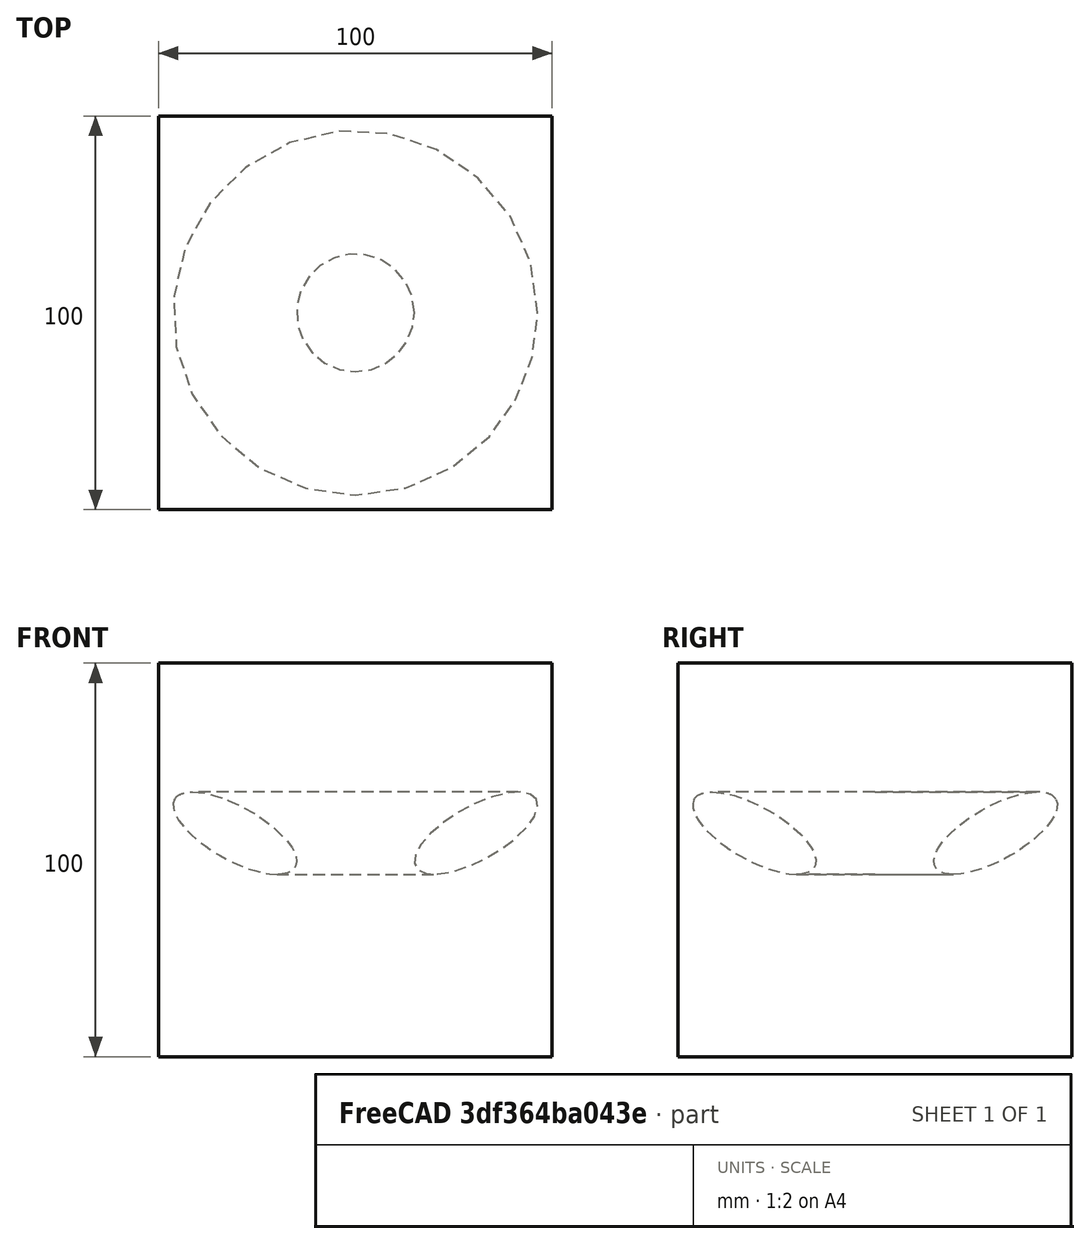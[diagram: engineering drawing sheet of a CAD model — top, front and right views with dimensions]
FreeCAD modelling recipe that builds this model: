
FCSTD DOCUMENT  (FreeCAD 0.21R33694 (Git))
Label: revolveSingleEdge
License: All rights reserved
LicenseURL: http://en.wikipedia.org/wiki/All_rights_reserved
objects: App::DocumentObjectGroupPython×1248, App::Part×2, Part::FeaturePython×1, Sketcher::SketchObject×1, Part::Revolution×1
note: 3 computed .brp shape members not serialized (recipe doc carries the construction recipe); baked Part::Feature solids carry a one-line shape summary decoded from their .brp

FEATURE [App::DocumentObjectGroupPython] HALFPI  # scripted group (container) (typed FeaturePython)
  name = HALFPI
  value = pi/2.
FEATURE [App::DocumentObjectGroupPython] PI  # scripted group (container) (typed FeaturePython)
  name = PI
  value = 1.*pi
FEATURE [App::DocumentObjectGroupPython] TWOPI  # scripted group (container) (typed FeaturePython)
  name = TWOPI
  value = 2.*pi
FEATURE [App::DocumentObjectGroupPython] Constants  # scripted group (container) (typed FeaturePython)
  Group = -> [HALFPI,PI,TWOPI]
FEATURE [App::DocumentObjectGroupPython] Variables  # scripted group (container) (typed FeaturePython)
FEATURE [App::DocumentObjectGroupPython] Quantities  # scripted group (container) (typed FeaturePython)
FEATURE [App::DocumentObjectGroupPython] Isotopes  # scripted group (container) (typed FeaturePython)
FEATURE [App::DocumentObjectGroupPython] Elements  # scripted group (container) (typed FeaturePython)
FEATURE [App::DocumentObjectGroupPython] G4Isotopes  # scripted group (container) (typed FeaturePython)
FEATURE [App::DocumentObjectGroupPython] H_element  # scripted group (container) (typed FeaturePython)
  Z = 1
  atom_value = 1.008
  formula = H
  name = H_element
FEATURE [App::DocumentObjectGroupPython] He_element  # scripted group (container) (typed FeaturePython)
  Z = 2
  atom_value = 4.0026
  formula = He
  name = He_element
FEATURE [App::DocumentObjectGroupPython] Li_element  # scripted group (container) (typed FeaturePython)
  Z = 3
  atom_value = 6.94
  formula = Li
  name = Li_element
FEATURE [App::DocumentObjectGroupPython] Be_element  # scripted group (container) (typed FeaturePython)
  Z = 4
  atom_value = 9.01218
  formula = Be
  name = Be_element
FEATURE [App::DocumentObjectGroupPython] B_element  # scripted group (container) (typed FeaturePython)
  Z = 5
  atom_value = 10.81
  formula = B
  name = B_element
FEATURE [App::DocumentObjectGroupPython] C_element  # scripted group (container) (typed FeaturePython)
  Z = 6
  atom_value = 12.011
  formula = C
  name = C_element
FEATURE [App::DocumentObjectGroupPython] N_element  # scripted group (container) (typed FeaturePython)
  Z = 7
  atom_value = 14.007
  formula = N
  name = N_element
FEATURE [App::DocumentObjectGroupPython] O_element  # scripted group (container) (typed FeaturePython)
  Z = 8
  atom_value = 15.999
  formula = O
  name = O_element
FEATURE [App::DocumentObjectGroupPython] F_element  # scripted group (container) (typed FeaturePython)
  Z = 9
  atom_value = 18.9984
  formula = F
  name = F_element
FEATURE [App::DocumentObjectGroupPython] Ne_element  # scripted group (container) (typed FeaturePython)
  Z = 10
  atom_value = 20.1797
  formula = Ne
  name = Ne_element
FEATURE [App::DocumentObjectGroupPython] Na_element  # scripted group (container) (typed FeaturePython)
  Z = 11
  atom_value = 22.9898
  formula = Na
  name = Na_element
FEATURE [App::DocumentObjectGroupPython] Mg_element  # scripted group (container) (typed FeaturePython)
  Z = 12
  atom_value = 24.305
  formula = Mg
  name = Mg_element
FEATURE [App::DocumentObjectGroupPython] Al_element  # scripted group (container) (typed FeaturePython)
  Z = 13
  atom_value = 26.9815
  formula = Al
  name = Al_element
FEATURE [App::DocumentObjectGroupPython] Si_element  # scripted group (container) (typed FeaturePython)
  Z = 14
  atom_value = 28.085
  formula = Si
  name = Si_element
FEATURE [App::DocumentObjectGroupPython] P_element  # scripted group (container) (typed FeaturePython)
  Z = 15
  atom_value = 30.9738
  formula = P
  name = P_element
FEATURE [App::DocumentObjectGroupPython] S_element  # scripted group (container) (typed FeaturePython)
  Z = 16
  atom_value = 32.06
  formula = S
  name = S_element
FEATURE [App::DocumentObjectGroupPython] Cl_element  # scripted group (container) (typed FeaturePython)
  Z = 17
  atom_value = 35.45
  formula = Cl
  name = Cl_element
FEATURE [App::DocumentObjectGroupPython] Ar_element  # scripted group (container) (typed FeaturePython)
  Z = 18
  atom_value = 39.95
  formula = Ar
  name = Ar_element
FEATURE [App::DocumentObjectGroupPython] K_element  # scripted group (container) (typed FeaturePython)
  Z = 19
  atom_value = 39.0983
  formula = K
  name = K_element
FEATURE [App::DocumentObjectGroupPython] Ca_element  # scripted group (container) (typed FeaturePython)
  Z = 20
  atom_value = 40.078
  formula = Ca
  name = Ca_element
FEATURE [App::DocumentObjectGroupPython] Sc_element  # scripted group (container) (typed FeaturePython)
  Z = 21
  atom_value = 44.9559
  formula = Sc
  name = Sc_element
FEATURE [App::DocumentObjectGroupPython] Ti_element  # scripted group (container) (typed FeaturePython)
  Z = 22
  atom_value = 47.867
  formula = Ti
  name = Ti_element
FEATURE [App::DocumentObjectGroupPython] V_element  # scripted group (container) (typed FeaturePython)
  Z = 23
  atom_value = 50.9415
  formula = V
  name = V_element
FEATURE [App::DocumentObjectGroupPython] Cr_element  # scripted group (container) (typed FeaturePython)
  Z = 24
  atom_value = 51.9961
  formula = Cr
  name = Cr_element
FEATURE [App::DocumentObjectGroupPython] Mn_element  # scripted group (container) (typed FeaturePython)
  Z = 25
  atom_value = 54.938
  formula = Mn
  name = Mn_element
FEATURE [App::DocumentObjectGroupPython] Fe_element  # scripted group (container) (typed FeaturePython)
  Z = 26
  atom_value = 55.845
  formula = Fe
  name = Fe_element
FEATURE [App::DocumentObjectGroupPython] Co_element  # scripted group (container) (typed FeaturePython)
  Z = 27
  atom_value = 58.9332
  formula = Co
  name = Co_element
FEATURE [App::DocumentObjectGroupPython] Ni_element  # scripted group (container) (typed FeaturePython)
  Z = 28
  atom_value = 58.6934
  formula = Ni
  name = Ni_element
FEATURE [App::DocumentObjectGroupPython] Cu_element  # scripted group (container) (typed FeaturePython)
  Z = 29
  atom_value = 63.546
  formula = Cu
  name = Cu_element
FEATURE [App::DocumentObjectGroupPython] Zn_element  # scripted group (container) (typed FeaturePython)
  Z = 30
  atom_value = 65.38
  formula = Zn
  name = Zn_element
FEATURE [App::DocumentObjectGroupPython] Ga_element  # scripted group (container) (typed FeaturePython)
  Z = 31
  atom_value = 69.723
  formula = Ga
  name = Ga_element
FEATURE [App::DocumentObjectGroupPython] Ge_element  # scripted group (container) (typed FeaturePython)
  Z = 32
  atom_value = 72.63
  formula = Ge
  name = Ge_element
FEATURE [App::DocumentObjectGroupPython] As_element  # scripted group (container) (typed FeaturePython)
  Z = 33
  atom_value = 74.9216
  formula = As
  name = As_element
FEATURE [App::DocumentObjectGroupPython] Se_element  # scripted group (container) (typed FeaturePython)
  Z = 34
  atom_value = 78.971
  formula = Se
  name = Se_element
FEATURE [App::DocumentObjectGroupPython] Br_element  # scripted group (container) (typed FeaturePython)
  Z = 35
  atom_value = 79.904
  formula = Br
  name = Br_element
FEATURE [App::DocumentObjectGroupPython] Kr_element  # scripted group (container) (typed FeaturePython)
  Z = 36
  atom_value = 83.798
  formula = Kr
  name = Kr_element
FEATURE [App::DocumentObjectGroupPython] Rb_element  # scripted group (container) (typed FeaturePython)
  Z = 37
  atom_value = 85.4678
  formula = Rb
  name = Rb_element
FEATURE [App::DocumentObjectGroupPython] Sr_element  # scripted group (container) (typed FeaturePython)
  Z = 38
  atom_value = 87.62
  formula = Sr
  name = Sr_element
FEATURE [App::DocumentObjectGroupPython] Y_element  # scripted group (container) (typed FeaturePython)
  Z = 39
  atom_value = 88.9058
  formula = Y
  name = Y_element
FEATURE [App::DocumentObjectGroupPython] Zr_element  # scripted group (container) (typed FeaturePython)
  Z = 40
  atom_value = 91.224
  formula = Zr
  name = Zr_element
FEATURE [App::DocumentObjectGroupPython] Nb_element  # scripted group (container) (typed FeaturePython)
  Z = 41
  atom_value = 92.9064
  formula = Nb
  name = Nb_element
FEATURE [App::DocumentObjectGroupPython] Mo_element  # scripted group (container) (typed FeaturePython)
  Z = 42
  atom_value = 95.95
  formula = Mo
  name = Mo_element
FEATURE [App::DocumentObjectGroupPython] Tc_element  # scripted group (container) (typed FeaturePython)
  Z = 43
  atom_value = 97
  formula = Tc
  name = Tc_element
FEATURE [App::DocumentObjectGroupPython] Ru_element  # scripted group (container) (typed FeaturePython)
  Z = 44
  atom_value = 101.07
  formula = Ru
  name = Ru_element
FEATURE [App::DocumentObjectGroupPython] Rh_element  # scripted group (container) (typed FeaturePython)
  Z = 45
  atom_value = 102.905
  formula = Rh
  name = Rh_element
FEATURE [App::DocumentObjectGroupPython] Pd_element  # scripted group (container) (typed FeaturePython)
  Z = 46
  atom_value = 106.42
  formula = Pd
  name = Pd_element
FEATURE [App::DocumentObjectGroupPython] Ag_element  # scripted group (container) (typed FeaturePython)
  Z = 47
  atom_value = 107.868
  formula = Ag
  name = Ag_element
FEATURE [App::DocumentObjectGroupPython] Cd_element  # scripted group (container) (typed FeaturePython)
  Z = 48
  atom_value = 112.414
  formula = Cd
  name = Cd_element
FEATURE [App::DocumentObjectGroupPython] In_element  # scripted group (container) (typed FeaturePython)
  Z = 49
  atom_value = 114.818
  formula = In
  name = In_element
FEATURE [App::DocumentObjectGroupPython] Sn_element  # scripted group (container) (typed FeaturePython)
  Z = 50
  atom_value = 118.71
  formula = Sn
  name = Sn_element
FEATURE [App::DocumentObjectGroupPython] Sb_element  # scripted group (container) (typed FeaturePython)
  Z = 51
  atom_value = 121.76
  formula = Sb
  name = Sb_element
FEATURE [App::DocumentObjectGroupPython] Te_element  # scripted group (container) (typed FeaturePython)
  Z = 52
  atom_value = 127.6
  formula = Te
  name = Te_element
FEATURE [App::DocumentObjectGroupPython] I_element  # scripted group (container) (typed FeaturePython)
  Z = 53
  atom_value = 126.904
  formula = I
  name = I_element
FEATURE [App::DocumentObjectGroupPython] Xe_element  # scripted group (container) (typed FeaturePython)
  Z = 54
  atom_value = 131.293
  formula = Xe
  name = Xe_element
FEATURE [App::DocumentObjectGroupPython] Cs_element  # scripted group (container) (typed FeaturePython)
  Z = 55
  atom_value = 132.905
  formula = Cs
  name = Cs_element
FEATURE [App::DocumentObjectGroupPython] Ba_element  # scripted group (container) (typed FeaturePython)
  Z = 56
  atom_value = 137.327
  formula = Ba
  name = Ba_element
FEATURE [App::DocumentObjectGroupPython] La_element  # scripted group (container) (typed FeaturePython)
  Z = 57
  atom_value = 138.905
  formula = La
  name = La_element
FEATURE [App::DocumentObjectGroupPython] Ce_element  # scripted group (container) (typed FeaturePython)
  Z = 58
  atom_value = 140.116
  formula = Ce
  name = Ce_element
FEATURE [App::DocumentObjectGroupPython] Pr_element  # scripted group (container) (typed FeaturePython)
  Z = 59
  atom_value = 140.908
  formula = Pr
  name = Pr_element
FEATURE [App::DocumentObjectGroupPython] Nd_element  # scripted group (container) (typed FeaturePython)
  Z = 60
  atom_value = 144.242
  formula = Nd
  name = Nd_element
FEATURE [App::DocumentObjectGroupPython] Pm_element  # scripted group (container) (typed FeaturePython)
  Z = 61
  atom_value = 145
  formula = Pm
  name = Pm_element
FEATURE [App::DocumentObjectGroupPython] Sm_element  # scripted group (container) (typed FeaturePython)
  Z = 62
  atom_value = 150.36
  formula = Sm
  name = Sm_element
FEATURE [App::DocumentObjectGroupPython] Eu_element  # scripted group (container) (typed FeaturePython)
  Z = 63
  atom_value = 151.964
  formula = Eu
  name = Eu_element
FEATURE [App::DocumentObjectGroupPython] Gd_element  # scripted group (container) (typed FeaturePython)
  Z = 64
  atom_value = 157.25
  formula = Gd
  name = Gd_element
FEATURE [App::DocumentObjectGroupPython] Tb_element  # scripted group (container) (typed FeaturePython)
  Z = 65
  atom_value = 158.925
  formula = Tb
  name = Tb_element
FEATURE [App::DocumentObjectGroupPython] Dy_element  # scripted group (container) (typed FeaturePython)
  Z = 66
  atom_value = 162.5
  formula = Dy
  name = Dy_element
FEATURE [App::DocumentObjectGroupPython] Ho_element  # scripted group (container) (typed FeaturePython)
  Z = 67
  atom_value = 164.93
  formula = Ho
  name = Ho_element
FEATURE [App::DocumentObjectGroupPython] Er_element  # scripted group (container) (typed FeaturePython)
  Z = 68
  atom_value = 167.259
  formula = Er
  name = Er_element
FEATURE [App::DocumentObjectGroupPython] Tm_element  # scripted group (container) (typed FeaturePython)
  Z = 69
  atom_value = 168.934
  formula = Tm
  name = Tm_element
FEATURE [App::DocumentObjectGroupPython] Yb_element  # scripted group (container) (typed FeaturePython)
  Z = 70
  atom_value = 173.045
  formula = Yb
  name = Yb_element
FEATURE [App::DocumentObjectGroupPython] Lu_element  # scripted group (container) (typed FeaturePython)
  Z = 71
  atom_value = 174.967
  formula = Lu
  name = Lu_element
FEATURE [App::DocumentObjectGroupPython] Hf_element  # scripted group (container) (typed FeaturePython)
  Z = 72
  atom_value = 178.49
  formula = Hf
  name = Hf_element
FEATURE [App::DocumentObjectGroupPython] Ta_element  # scripted group (container) (typed FeaturePython)
  Z = 73
  atom_value = 180.948
  formula = Ta
  name = Ta_element
FEATURE [App::DocumentObjectGroupPython] W_element  # scripted group (container) (typed FeaturePython)
  Z = 74
  atom_value = 183.84
  formula = W
  name = W_element
FEATURE [App::DocumentObjectGroupPython] Re_element  # scripted group (container) (typed FeaturePython)
  Z = 75
  atom_value = 186.207
  formula = Re
  name = Re_element
FEATURE [App::DocumentObjectGroupPython] Os_element  # scripted group (container) (typed FeaturePython)
  Z = 76
  atom_value = 190.23
  formula = Os
  name = Os_element
FEATURE [App::DocumentObjectGroupPython] Ir_element  # scripted group (container) (typed FeaturePython)
  Z = 77
  atom_value = 192.217
  formula = Ir
  name = Ir_element
FEATURE [App::DocumentObjectGroupPython] Pt_element  # scripted group (container) (typed FeaturePython)
  Z = 78
  atom_value = 195.084
  formula = Pt
  name = Pt_element
FEATURE [App::DocumentObjectGroupPython] Au_element  # scripted group (container) (typed FeaturePython)
  Z = 79
  atom_value = 196.967
  formula = Au
  name = Au_element
FEATURE [App::DocumentObjectGroupPython] Hg_element  # scripted group (container) (typed FeaturePython)
  Z = 80
  atom_value = 200.592
  formula = Hg
  name = Hg_element
FEATURE [App::DocumentObjectGroupPython] Tl_element  # scripted group (container) (typed FeaturePython)
  Z = 81
  atom_value = 204.38
  formula = Tl
  name = Tl_element
FEATURE [App::DocumentObjectGroupPython] Pb_element  # scripted group (container) (typed FeaturePython)
  Z = 82
  atom_value = 207.2
  formula = Pb
  name = Pb_element
FEATURE [App::DocumentObjectGroupPython] Bi_element  # scripted group (container) (typed FeaturePython)
  Z = 83
  atom_value = 208.98
  formula = Bi
  name = Bi_element
FEATURE [App::DocumentObjectGroupPython] Po_element  # scripted group (container) (typed FeaturePython)
  Z = 84
  atom_value = 209
  formula = Po
  name = Po_element
FEATURE [App::DocumentObjectGroupPython] At_element  # scripted group (container) (typed FeaturePython)
  Z = 85
  atom_value = 210
  formula = At
  name = At_element
FEATURE [App::DocumentObjectGroupPython] Rn_element  # scripted group (container) (typed FeaturePython)
  Z = 86
  atom_value = 222
  formula = Rn
  name = Rn_element
FEATURE [App::DocumentObjectGroupPython] Fr_element  # scripted group (container) (typed FeaturePython)
  Z = 87
  atom_value = 223
  formula = Fr
  name = Fr_element
FEATURE [App::DocumentObjectGroupPython] Ra_element  # scripted group (container) (typed FeaturePython)
  Z = 88
  atom_value = 226
  formula = Ra
  name = Ra_element
FEATURE [App::DocumentObjectGroupPython] Ac_element  # scripted group (container) (typed FeaturePython)
  Z = 89
  atom_value = 227
  formula = Ac
  name = Ac_element
FEATURE [App::DocumentObjectGroupPython] Th_element  # scripted group (container) (typed FeaturePython)
  Z = 90
  atom_value = 232.038
  formula = Th
  name = Th_element
FEATURE [App::DocumentObjectGroupPython] Pa_element  # scripted group (container) (typed FeaturePython)
  Z = 91
  atom_value = 231.036
  formula = Pa
  name = Pa_element
FEATURE [App::DocumentObjectGroupPython] U_element  # scripted group (container) (typed FeaturePython)
  Z = 92
  atom_value = 238.029
  formula = U
  name = U_element
FEATURE [App::DocumentObjectGroupPython] Np_element  # scripted group (container) (typed FeaturePython)
  Z = 93
  atom_value = 237
  formula = Np
  name = Np_element
FEATURE [App::DocumentObjectGroupPython] Pu_element  # scripted group (container) (typed FeaturePython)
  Z = 94
  atom_value = 244
  formula = Pu
  name = Pu_element
FEATURE [App::DocumentObjectGroupPython] Am_element  # scripted group (container) (typed FeaturePython)
  Z = 95
  atom_value = 243
  formula = Am
  name = Am_element
FEATURE [App::DocumentObjectGroupPython] Cm_element  # scripted group (container) (typed FeaturePython)
  Z = 96
  atom_value = 247
  formula = Cm
  name = Cm_element
FEATURE [App::DocumentObjectGroupPython] Bk_element  # scripted group (container) (typed FeaturePython)
  Z = 97
  atom_value = 247
  formula = Bk
  name = Bk_element
FEATURE [App::DocumentObjectGroupPython] Cf_element  # scripted group (container) (typed FeaturePython)
  Z = 98
  atom_value = 251
  formula = Cf
  name = Cf_element
FEATURE [App::DocumentObjectGroupPython] G4Elements  # scripted group (container) (typed FeaturePython)
  Group = -> [H_element,He_element,Li_element,Be_element,B_element,C_element,N_element,O_element,F_element,Ne_element,Na_element,Mg_element,Al_element,Si_element,P_element,S_element,Cl_element,Ar_element,K_element,Ca_element,Sc_element,Ti_element,V_element,Cr_element,Mn_element,Fe_element,Co_element,Ni_element,Cu_element,Zn_element,Ga_element,Ge_element,As_element,Se_element,Br_element,Kr_element,Rb_element,+61 more]
FEATURE [App::DocumentObjectGroupPython] H_element001  label="H_element : 0.101"  # scripted group (container) (typed FeaturePython)
  n = 0.101327
FEATURE [App::DocumentObjectGroupPython] C_element001  label="C_element : 0.775"  # scripted group (container) (typed FeaturePython)
  n = 0.7755
FEATURE [App::DocumentObjectGroupPython] N_element001  label="N_element : 0.035"  # scripted group (container) (typed FeaturePython)
  n = 0.035057
FEATURE [App::DocumentObjectGroupPython] O_element001  label="O_element : 0.052"  # scripted group (container) (typed FeaturePython)
  n = 0.0523159
FEATURE [App::DocumentObjectGroupPython] F_element001  label="F_element : 0.017"  # scripted group (container) (typed FeaturePython)
  n = 0.017422
FEATURE [App::DocumentObjectGroupPython] Ca_element001  label="Ca_element : 0.018"  # scripted group (container) (typed FeaturePython)
  n = 0.018378
FEATURE [App::DocumentObjectGroupPython] G4_A_150_TISSUE  label="G4_A-150_TISSUE"  # scripted group (container) (typed FeaturePython)
  Dunit = g/cm3
  Dvalue = 1.127
  Group = -> [H_element001,C_element001,N_element001,O_element001,F_element001,Ca_element001]
  conduct = 2
  density = 1
  expand = 3
  formula = G4_A-150_TISSUE
  name = G4_A-150_TISSUE
  specific = 4
FEATURE [App::DocumentObjectGroupPython] C_element002  label="C_element : 3"  # scripted group (container) (typed FeaturePython)
  n = 3
  ref = C_element
FEATURE [App::DocumentObjectGroupPython] H_element002  label="H_element : 6"  # scripted group (container) (typed FeaturePython)
  n = 6
  ref = H_element
FEATURE [App::DocumentObjectGroupPython] O_element002  label="O_element : 1"  # scripted group (container) (typed FeaturePython)
  n = 1
  ref = O_element
FEATURE [App::DocumentObjectGroupPython] G4_ACETONE  # scripted group (container) (typed FeaturePython)
  Dunit = g/cm3
  Dvalue = 0.7899
  Group = -> [C_element002,H_element002,O_element002]
  conduct = 2
  density = 1
  expand = 3
  formula = G4_ACETONE
  name = G4_ACETONE
  specific = 4
FEATURE [App::DocumentObjectGroupPython] C_element003  label="C_element : 2"  # scripted group (container) (typed FeaturePython)
  n = 2
  ref = C_element
FEATURE [App::DocumentObjectGroupPython] H_element003  label="H_element : 2"  # scripted group (container) (typed FeaturePython)
  n = 2
  ref = H_element
FEATURE [App::DocumentObjectGroupPython] G4_ACETYLENE  # scripted group (container) (typed FeaturePython)
  Dunit = g/cm3
  Dvalue = 0.0010967
  Group = -> [C_element003,H_element003]
  conduct = 2
  density = 1
  expand = 3
  formula = G4_ACETYLENE
  name = G4_ACETYLENE
  specific = 4
FEATURE [App::DocumentObjectGroupPython] C_element004  label="C_element : 5"  # scripted group (container) (typed FeaturePython)
  n = 5
  ref = C_element
FEATURE [App::DocumentObjectGroupPython] H_element004  label="H_element : 5"  # scripted group (container) (typed FeaturePython)
  n = 5
  ref = H_element
FEATURE [App::DocumentObjectGroupPython] N_element002  label="N_element : 5"  # scripted group (container) (typed FeaturePython)
  n = 5
  ref = N_element
FEATURE [App::DocumentObjectGroupPython] G4_ADENINE  # scripted group (container) (typed FeaturePython)
  Dunit = g/cm3
  Dvalue = 1.6
  Group = -> [C_element004,H_element004,N_element002]
  conduct = 2
  density = 1
  expand = 3
  formula = G4_ADENINE
  name = G4_ADENINE
  specific = 4
FEATURE [App::DocumentObjectGroupPython] H_element005  label="H_element : 0.114"  # scripted group (container) (typed FeaturePython)
  n = 0.114
FEATURE [App::DocumentObjectGroupPython] C_element005  label="C_element : 0.598"  # scripted group (container) (typed FeaturePython)
  n = 0.598
FEATURE [App::DocumentObjectGroupPython] N_element003  label="N_element : 0.007"  # scripted group (container) (typed FeaturePython)
  n = 0.007
FEATURE [App::DocumentObjectGroupPython] O_element003  label="O_element : 0.278"  # scripted group (container) (typed FeaturePython)
  n = 0.278
FEATURE [App::DocumentObjectGroupPython] Na_element001  label="Na_element : 0.001"  # scripted group (container) (typed FeaturePython)
  n = 0.001
FEATURE [App::DocumentObjectGroupPython] S_element001  label="S_element : 0.001"  # scripted group (container) (typed FeaturePython)
  n = 0.001
FEATURE [App::DocumentObjectGroupPython] Cl_element001  label="Cl_element : 0.001"  # scripted group (container) (typed FeaturePython)
  n = 0.001
FEATURE [App::DocumentObjectGroupPython] G4_ADIPOSE_TISSUE_ICRP  # scripted group (container) (typed FeaturePython)
  Dunit = g/cm3
  Dvalue = 0.95
  Group = -> [H_element005,C_element005,N_element003,O_element003,Na_element001,S_element001,Cl_element001]
  conduct = 2
  density = 1
  expand = 3
  formula = G4_ADIPOSE_TISSUE_ICRP
  name = G4_ADIPOSE_TISSUE_ICRP
  specific = 4
FEATURE [App::DocumentObjectGroupPython] C_element006  label="C_element : 0.000"  # scripted group (container) (typed FeaturePython)
  n = 0.000124
FEATURE [App::DocumentObjectGroupPython] N_element004  label="N_element : 0.755"  # scripted group (container) (typed FeaturePython)
  n = 0.755268
FEATURE [App::DocumentObjectGroupPython] O_element004  label="O_element : 0.232"  # scripted group (container) (typed FeaturePython)
  n = 0.231781
FEATURE [App::DocumentObjectGroupPython] Ar_element001  label="Ar_element : 0.013"  # scripted group (container) (typed FeaturePython)
  n = 0.012827
FEATURE [App::DocumentObjectGroupPython] G4_AIR  # scripted group (container) (typed FeaturePython)
  Dunit = g/cm3
  Dvalue = 0.00120479
  Group = -> [C_element006,N_element004,O_element004,Ar_element001]
  conduct = 2
  density = 1
  expand = 3
  formula = G4_AIR
  name = G4_AIR
  specific = 4
FEATURE [App::DocumentObjectGroupPython] C_element007  label="C_element : 006"  # scripted group (container) (typed FeaturePython)
  n = 3
  ref = C_element
FEATURE [App::DocumentObjectGroupPython] H_element006  label="H_element : 7"  # scripted group (container) (typed FeaturePython)
  n = 7
  ref = H_element
FEATURE [App::DocumentObjectGroupPython] N_element005  label="N_element : 1"  # scripted group (container) (typed FeaturePython)
  n = 1
  ref = N_element
FEATURE [App::DocumentObjectGroupPython] O_element005  label="O_element : 2"  # scripted group (container) (typed FeaturePython)
  n = 2
  ref = O_element
FEATURE [App::DocumentObjectGroupPython] G4_ALANINE  # scripted group (container) (typed FeaturePython)
  Dunit = g/cm3
  Dvalue = 1.42
  Group = -> [C_element007,H_element006,N_element005,O_element005]
  conduct = 2
  density = 1
  expand = 3
  formula = G4_ALANINE
  name = G4_ALANINE
  specific = 4
FEATURE [App::DocumentObjectGroupPython] Al_element001  label="Al_element : 2"  # scripted group (container) (typed FeaturePython)
  n = 2
  ref = Al_element
FEATURE [App::DocumentObjectGroupPython] O_element006  label="O_element : 3"  # scripted group (container) (typed FeaturePython)
  n = 3
  ref = O_element
FEATURE [App::DocumentObjectGroupPython] G4_ALUMINUM_OXIDE  # scripted group (container) (typed FeaturePython)
  Dunit = g/cm3
  Dvalue = 3.97
  Group = -> [Al_element001,O_element006]
  conduct = 2
  density = 1
  expand = 3
  formula = G4_ALUMINUM_OXIDE
  name = G4_ALUMINUM_OXIDE
  specific = 4
FEATURE [App::DocumentObjectGroupPython] H_element007  label="H_element : 0.106"  # scripted group (container) (typed FeaturePython)
  n = 0.10593
FEATURE [App::DocumentObjectGroupPython] C_element008  label="C_element : 0.789"  # scripted group (container) (typed FeaturePython)
  n = 0.788974
FEATURE [App::DocumentObjectGroupPython] O_element007  label="O_element : 0.105"  # scripted group (container) (typed FeaturePython)
  n = 0.105096
FEATURE [App::DocumentObjectGroupPython] G4_AMBER  # scripted group (container) (typed FeaturePython)
  Dunit = g/cm3
  Dvalue = 1.1
  Group = -> [H_element007,C_element008,O_element007]
  conduct = 2
  density = 1
  expand = 3
  formula = G4_AMBER
  name = G4_AMBER
  specific = 4
FEATURE [App::DocumentObjectGroupPython] N_element006  label="N_element : 006"  # scripted group (container) (typed FeaturePython)
  n = 1
  ref = N_element
FEATURE [App::DocumentObjectGroupPython] H_element008  label="H_element : 3"  # scripted group (container) (typed FeaturePython)
  n = 3
  ref = H_element
FEATURE [App::DocumentObjectGroupPython] G4_AMMONIA  # scripted group (container) (typed FeaturePython)
  Dunit = g/cm3
  Dvalue = 0.000826019
  Group = -> [N_element006,H_element008]
  conduct = 2
  density = 1
  expand = 3
  formula = G4_AMMONIA
  name = G4_AMMONIA
  specific = 4
FEATURE [App::DocumentObjectGroupPython] C_element009  label="C_element : 6"  # scripted group (container) (typed FeaturePython)
  n = 6
  ref = C_element
FEATURE [App::DocumentObjectGroupPython] H_element009  label="H_element : 008"  # scripted group (container) (typed FeaturePython)
  n = 7
  ref = H_element
FEATURE [App::DocumentObjectGroupPython] N_element007  label="N_element : 007"  # scripted group (container) (typed FeaturePython)
  n = 1
  ref = N_element
FEATURE [App::DocumentObjectGroupPython] G4_ANILINE  # scripted group (container) (typed FeaturePython)
  Dunit = g/cm3
  Dvalue = 1.0235
  Group = -> [C_element009,H_element009,N_element007]
  conduct = 2
  density = 1
  expand = 3
  formula = G4_ANILINE
  name = G4_ANILINE
  specific = 4
FEATURE [App::DocumentObjectGroupPython] C_element010  label="C_element : 14"  # scripted group (container) (typed FeaturePython)
  n = 14
  ref = C_element
FEATURE [App::DocumentObjectGroupPython] H_element010  label="H_element : 10"  # scripted group (container) (typed FeaturePython)
  n = 10
  ref = H_element
FEATURE [App::DocumentObjectGroupPython] G4_ANTHRACENE  # scripted group (container) (typed FeaturePython)
  Dunit = g/cm3
  Dvalue = 1.283
  Group = -> [C_element010,H_element010]
  conduct = 2
  density = 1
  expand = 3
  formula = G4_ANTHRACENE
  name = G4_ANTHRACENE
  specific = 4
FEATURE [App::DocumentObjectGroupPython] H_element011  label="H_element : 0.065"  # scripted group (container) (typed FeaturePython)
  n = 0.0654709
FEATURE [App::DocumentObjectGroupPython] C_element011  label="C_element : 0.537"  # scripted group (container) (typed FeaturePython)
  n = 0.536944
FEATURE [App::DocumentObjectGroupPython] N_element008  label="N_element : 0.021"  # scripted group (container) (typed FeaturePython)
  n = 0.0215
FEATURE [App::DocumentObjectGroupPython] O_element008  label="O_element : 0.032"  # scripted group (container) (typed FeaturePython)
  n = 0.032085
FEATURE [App::DocumentObjectGroupPython] F_element002  label="F_element : 0.167"  # scripted group (container) (typed FeaturePython)
  n = 0.167411
FEATURE [App::DocumentObjectGroupPython] Ca_element002  label="Ca_element : 0.177"  # scripted group (container) (typed FeaturePython)
  n = 0.176589
FEATURE [App::DocumentObjectGroupPython] G4_B_100_BONE  label="G4_B-100_BONE"  # scripted group (container) (typed FeaturePython)
  Dunit = g/cm3
  Dvalue = 1.45
  Group = -> [H_element011,C_element011,N_element008,O_element008,F_element002,Ca_element002]
  conduct = 2
  density = 1
  expand = 3
  formula = G4_B-100_BONE
  name = G4_B-100_BONE
  specific = 4
FEATURE [App::DocumentObjectGroupPython] H_element012  label="H_element : 0.057"  # scripted group (container) (typed FeaturePython)
  n = 0.057441
FEATURE [App::DocumentObjectGroupPython] C_element012  label="C_element : 0.790"  # scripted group (container) (typed FeaturePython)
  n = 0.774591
FEATURE [App::DocumentObjectGroupPython] O_element009  label="O_element : 0.168"  # scripted group (container) (typed FeaturePython)
  n = 0.167968
FEATURE [App::DocumentObjectGroupPython] G4_BAKELITE  # scripted group (container) (typed FeaturePython)
  Dunit = g/cm3
  Dvalue = 1.25
  Group = -> [H_element012,C_element012,O_element009]
  conduct = 2
  density = 1
  expand = 3
  formula = G4_BAKELITE
  name = G4_BAKELITE
  specific = 4
FEATURE [App::DocumentObjectGroupPython] Ba_element001  label="Ba_element : 1"  # scripted group (container) (typed FeaturePython)
  n = 1
  ref = Ba_element
FEATURE [App::DocumentObjectGroupPython] F_element003  label="F_element : 2"  # scripted group (container) (typed FeaturePython)
  n = 2
  ref = F_element
FEATURE [App::DocumentObjectGroupPython] G4_BARIUM_FLUORIDE  # scripted group (container) (typed FeaturePython)
  Dunit = g/cm3
  Dvalue = 4.89
  Group = -> [Ba_element001,F_element003]
  conduct = 2
  density = 1
  expand = 3
  formula = G4_BARIUM_FLUORIDE
  name = G4_BARIUM_FLUORIDE
  specific = 4
FEATURE [App::DocumentObjectGroupPython] Ba_element002  label="Ba_element : 002"  # scripted group (container) (typed FeaturePython)
  n = 1
  ref = Ba_element
FEATURE [App::DocumentObjectGroupPython] S_element002  label="S_element : 1"  # scripted group (container) (typed FeaturePython)
  n = 1
  ref = S_element
FEATURE [App::DocumentObjectGroupPython] O_element010  label="O_element : 4"  # scripted group (container) (typed FeaturePython)
  n = 4
  ref = O_element
FEATURE [App::DocumentObjectGroupPython] G4_BARIUM_SULFATE  # scripted group (container) (typed FeaturePython)
  Dunit = g/cm3
  Dvalue = 4.5
  Group = -> [Ba_element002,S_element002,O_element010]
  conduct = 2
  density = 1
  expand = 3
  formula = G4_BARIUM_SULFATE
  name = G4_BARIUM_SULFATE
  specific = 4
FEATURE [App::DocumentObjectGroupPython] C_element013  label="C_element : 007"  # scripted group (container) (typed FeaturePython)
  n = 6
  ref = C_element
FEATURE [App::DocumentObjectGroupPython] H_element013  label="H_element : 009"  # scripted group (container) (typed FeaturePython)
  n = 6
  ref = H_element
FEATURE [App::DocumentObjectGroupPython] G4_BENZENE  # scripted group (container) (typed FeaturePython)
  Dunit = g/cm3
  Dvalue = 0.87865
  Group = -> [C_element013,H_element013]
  conduct = 2
  density = 1
  expand = 3
  formula = G4_BENZENE
  name = G4_BENZENE
  specific = 4
FEATURE [App::DocumentObjectGroupPython] Be_element001  label="Be_element : 1"  # scripted group (container) (typed FeaturePython)
  n = 1
  ref = Be_element
FEATURE [App::DocumentObjectGroupPython] O_element011  label="O_element : 005"  # scripted group (container) (typed FeaturePython)
  n = 1
  ref = O_element
FEATURE [App::DocumentObjectGroupPython] G4_BERYLLIUM_OXIDE  # scripted group (container) (typed FeaturePython)
  Dunit = g/cm3
  Dvalue = 3.01
  Group = -> [Be_element001,O_element011]
  conduct = 2
  density = 1
  expand = 3
  formula = G4_BERYLLIUM_OXIDE
  name = G4_BERYLLIUM_OXIDE
  specific = 4
FEATURE [App::DocumentObjectGroupPython] Bi_element001  label="Bi_element : 4"  # scripted group (container) (typed FeaturePython)
  n = 4
  ref = Bi_element
FEATURE [App::DocumentObjectGroupPython] Ge_element001  label="Ge_element : 3"  # scripted group (container) (typed FeaturePython)
  n = 3
  ref = Ge_element
FEATURE [App::DocumentObjectGroupPython] O_element012  label="O_element : 12"  # scripted group (container) (typed FeaturePython)
  n = 12
  ref = O_element
FEATURE [App::DocumentObjectGroupPython] G4_BGO  # scripted group (container) (typed FeaturePython)
  Dunit = g/cm3
  Dvalue = 7.13
  Group = -> [Bi_element001,Ge_element001,O_element012]
  conduct = 2
  density = 1
  expand = 3
  formula = G4_BGO
  name = G4_BGO
  specific = 4
FEATURE [App::DocumentObjectGroupPython] H_element014  label="H_element : 0.102"  # scripted group (container) (typed FeaturePython)
  n = 0.102
FEATURE [App::DocumentObjectGroupPython] C_element014  label="C_element : 0.110"  # scripted group (container) (typed FeaturePython)
  n = 0.11
FEATURE [App::DocumentObjectGroupPython] N_element009  label="N_element : 0.033"  # scripted group (container) (typed FeaturePython)
  n = 0.033
FEATURE [App::DocumentObjectGroupPython] O_element013  label="O_element : 0.745"  # scripted group (container) (typed FeaturePython)
  n = 0.745
FEATURE [App::DocumentObjectGroupPython] Na_element002  label="Na_element : 0.002"  # scripted group (container) (typed FeaturePython)
  n = 0.001
FEATURE [App::DocumentObjectGroupPython] P_element001  label="P_element : 0.001"  # scripted group (container) (typed FeaturePython)
  n = 0.001
FEATURE [App::DocumentObjectGroupPython] S_element003  label="S_element : 0.002"  # scripted group (container) (typed FeaturePython)
  n = 0.002
FEATURE [App::DocumentObjectGroupPython] Cl_element002  label="Cl_element : 0.003"  # scripted group (container) (typed FeaturePython)
  n = 0.003
FEATURE [App::DocumentObjectGroupPython] K_element001  label="K_element : 0.002"  # scripted group (container) (typed FeaturePython)
  n = 0.002
FEATURE [App::DocumentObjectGroupPython] Fe_element001  label="Fe_element : 0.001"  # scripted group (container) (typed FeaturePython)
  n = 0.001
FEATURE [App::DocumentObjectGroupPython] G4_BLOOD_ICRP  # scripted group (container) (typed FeaturePython)
  Dunit = g/cm3
  Dvalue = 1.06
  Group = -> [H_element014,C_element014,N_element009,O_element013,Na_element002,P_element001,S_element003,Cl_element002,K_element001,Fe_element001]
  conduct = 2
  density = 1
  expand = 3
  formula = G4_BLOOD_ICRP
  name = G4_BLOOD_ICRP
  specific = 4
FEATURE [App::DocumentObjectGroupPython] H_element015  label="H_element : 0.064"  # scripted group (container) (typed FeaturePython)
  n = 0.064
FEATURE [App::DocumentObjectGroupPython] C_element015  label="C_element : 0.278"  # scripted group (container) (typed FeaturePython)
  n = 0.278
FEATURE [App::DocumentObjectGroupPython] N_element010  label="N_element : 0.027"  # scripted group (container) (typed FeaturePython)
  n = 0.027
FEATURE [App::DocumentObjectGroupPython] O_element014  label="O_element : 0.410"  # scripted group (container) (typed FeaturePython)
  n = 0.41
FEATURE [App::DocumentObjectGroupPython] Mg_element001  label="Mg_element : 0.002"  # scripted group (container) (typed FeaturePython)
  n = 0.002
FEATURE [App::DocumentObjectGroupPython] P_element002  label="P_element : 0.070"  # scripted group (container) (typed FeaturePython)
  n = 0.07
FEATURE [App::DocumentObjectGroupPython] S_element004  label="S_element : 0.003"  # scripted group (container) (typed FeaturePython)
  n = 0.002
FEATURE [App::DocumentObjectGroupPython] Ca_element003  label="Ca_element : 0.147"  # scripted group (container) (typed FeaturePython)
  n = 0.147
FEATURE [App::DocumentObjectGroupPython] G4_BONE_COMPACT_ICRU  # scripted group (container) (typed FeaturePython)
  Dunit = g/cm3
  Dvalue = 1.85
  Group = -> [H_element015,C_element015,N_element010,O_element014,Mg_element001,P_element002,S_element004,Ca_element003]
  conduct = 2
  density = 1
  expand = 3
  formula = G4_BONE_COMPACT_ICRU
  name = G4_BONE_COMPACT_ICRU
  specific = 4
FEATURE [App::DocumentObjectGroupPython] H_element016  label="H_element : 0.034"  # scripted group (container) (typed FeaturePython)
  n = 0.034
FEATURE [App::DocumentObjectGroupPython] C_element016  label="C_element : 0.155"  # scripted group (container) (typed FeaturePython)
  n = 0.155
FEATURE [App::DocumentObjectGroupPython] N_element011  label="N_element : 0.042"  # scripted group (container) (typed FeaturePython)
  n = 0.042
FEATURE [App::DocumentObjectGroupPython] O_element015  label="O_element : 0.435"  # scripted group (container) (typed FeaturePython)
  n = 0.435
FEATURE [App::DocumentObjectGroupPython] Na_element003  label="Na_element : 0.003"  # scripted group (container) (typed FeaturePython)
  n = 0.001
FEATURE [App::DocumentObjectGroupPython] Mg_element002  label="Mg_element : 0.003"  # scripted group (container) (typed FeaturePython)
  n = 0.002
FEATURE [App::DocumentObjectGroupPython] P_element003  label="P_element : 0.103"  # scripted group (container) (typed FeaturePython)
  n = 0.103
FEATURE [App::DocumentObjectGroupPython] S_element005  label="S_element : 0.004"  # scripted group (container) (typed FeaturePython)
  n = 0.003
FEATURE [App::DocumentObjectGroupPython] Ca_element004  label="Ca_element : 0.225"  # scripted group (container) (typed FeaturePython)
  n = 0.225
FEATURE [App::DocumentObjectGroupPython] G4_BONE_CORTICAL_ICRP  # scripted group (container) (typed FeaturePython)
  Dunit = g/cm3
  Dvalue = 1.92
  Group = -> [H_element016,C_element016,N_element011,O_element015,Na_element003,Mg_element002,P_element003,S_element005,Ca_element004]
  conduct = 2
  density = 1
  expand = 3
  formula = G4_BONE_CORTICAL_ICRP
  name = G4_BONE_CORTICAL_ICRP
  specific = 4
FEATURE [App::DocumentObjectGroupPython] B_element001  label="B_element : 4"  # scripted group (container) (typed FeaturePython)
  n = 4
  ref = B_element
FEATURE [App::DocumentObjectGroupPython] C_element017  label="C_element : 1"  # scripted group (container) (typed FeaturePython)
  n = 1
  ref = C_element
FEATURE [App::DocumentObjectGroupPython] G4_BORON_CARBIDE  # scripted group (container) (typed FeaturePython)
  Dunit = g/cm3
  Dvalue = 2.52
  Group = -> [B_element001,C_element017]
  conduct = 2
  density = 1
  expand = 3
  formula = G4_BORON_CARBIDE
  name = G4_BORON_CARBIDE
  specific = 4
FEATURE [App::DocumentObjectGroupPython] B_element002  label="B_element : 2"  # scripted group (container) (typed FeaturePython)
  n = 2
  ref = B_element
FEATURE [App::DocumentObjectGroupPython] O_element016  label="O_element : 006"  # scripted group (container) (typed FeaturePython)
  n = 3
  ref = O_element
FEATURE [App::DocumentObjectGroupPython] G4_BORON_OXIDE  # scripted group (container) (typed FeaturePython)
  Dunit = g/cm3
  Dvalue = 1.812
  Group = -> [B_element002,O_element016]
  conduct = 2
  density = 1
  expand = 3
  formula = G4_BORON_OXIDE
  name = G4_BORON_OXIDE
  specific = 4
FEATURE [App::DocumentObjectGroupPython] H_element017  label="H_element : 0.107"  # scripted group (container) (typed FeaturePython)
  n = 0.107
FEATURE [App::DocumentObjectGroupPython] C_element018  label="C_element : 0.145"  # scripted group (container) (typed FeaturePython)
  n = 0.145
FEATURE [App::DocumentObjectGroupPython] N_element012  label="N_element : 0.022"  # scripted group (container) (typed FeaturePython)
  n = 0.022
FEATURE [App::DocumentObjectGroupPython] O_element017  label="O_element : 0.712"  # scripted group (container) (typed FeaturePython)
  n = 0.712
FEATURE [App::DocumentObjectGroupPython] Na_element004  label="Na_element : 0.004"  # scripted group (container) (typed FeaturePython)
  n = 0.002
FEATURE [App::DocumentObjectGroupPython] P_element004  label="P_element : 0.004"  # scripted group (container) (typed FeaturePython)
  n = 0.004
FEATURE [App::DocumentObjectGroupPython] S_element006  label="S_element : 0.005"  # scripted group (container) (typed FeaturePython)
  n = 0.002
FEATURE [App::DocumentObjectGroupPython] Cl_element003  label="Cl_element : 0.004"  # scripted group (container) (typed FeaturePython)
  n = 0.003
FEATURE [App::DocumentObjectGroupPython] K_element002  label="K_element : 0.003"  # scripted group (container) (typed FeaturePython)
  n = 0.003
FEATURE [App::DocumentObjectGroupPython] G4_BRAIN_ICRP  # scripted group (container) (typed FeaturePython)
  Dunit = g/cm3
  Dvalue = 1.04
  Group = -> [H_element017,C_element018,N_element012,O_element017,Na_element004,P_element004,S_element006,Cl_element003,K_element002]
  conduct = 2
  density = 1
  expand = 3
  formula = G4_BRAIN_ICRP
  name = G4_BRAIN_ICRP
  specific = 4
FEATURE [App::DocumentObjectGroupPython] C_element019  label="C_element : 4"  # scripted group (container) (typed FeaturePython)
  n = 4
  ref = C_element
FEATURE [App::DocumentObjectGroupPython] H_element018  label="H_element : 010"  # scripted group (container) (typed FeaturePython)
  n = 10
  ref = H_element
FEATURE [App::DocumentObjectGroupPython] G4_BUTANE  # scripted group (container) (typed FeaturePython)
  Dunit = g/cm3
  Dvalue = 0.00249343
  Group = -> [C_element019,H_element018]
  conduct = 2
  density = 1
  expand = 3
  formula = G4_BUTANE
  name = G4_BUTANE
  specific = 4
FEATURE [App::DocumentObjectGroupPython] C_element020  label="C_element : 008"  # scripted group (container) (typed FeaturePython)
  n = 4
  ref = C_element
FEATURE [App::DocumentObjectGroupPython] H_element019  label="H_element : 011"  # scripted group (container) (typed FeaturePython)
  n = 10
  ref = H_element
FEATURE [App::DocumentObjectGroupPython] O_element018  label="O_element : 007"  # scripted group (container) (typed FeaturePython)
  n = 1
  ref = O_element
FEATURE [App::DocumentObjectGroupPython] G4_N_BUTYL_ALCOHOL  label="G4_N-BUTYL_ALCOHOL"  # scripted group (container) (typed FeaturePython)
  Dunit = g/cm3
  Dvalue = 0.8098
  Group = -> [C_element020,H_element019,O_element018]
  conduct = 2
  density = 1
  expand = 3
  formula = G4_N-BUTYL_ALCOHOL
  name = G4_N-BUTYL_ALCOHOL
  specific = 4
FEATURE [App::DocumentObjectGroupPython] H_element020  label="H_element : 0.025"  # scripted group (container) (typed FeaturePython)
  n = 0.02468
FEATURE [App::DocumentObjectGroupPython] C_element021  label="C_element : 0.502"  # scripted group (container) (typed FeaturePython)
  n = 0.501611
FEATURE [App::DocumentObjectGroupPython] O_element019  label="O_element : 0.005"  # scripted group (container) (typed FeaturePython)
  n = 0.004527
FEATURE [App::DocumentObjectGroupPython] F_element004  label="F_element : 0.465"  # scripted group (container) (typed FeaturePython)
  n = 0.465209
FEATURE [App::DocumentObjectGroupPython] Si_element001  label="Si_element : 0.004"  # scripted group (container) (typed FeaturePython)
  n = 0.003973
FEATURE [App::DocumentObjectGroupPython] G4_C_552  label="G4_C-552"  # scripted group (container) (typed FeaturePython)
  Dunit = g/cm3
  Dvalue = 1.76
  Group = -> [H_element020,C_element021,O_element019,F_element004,Si_element001]
  conduct = 2
  density = 1
  expand = 3
  formula = G4_C-552
  name = G4_C-552
  specific = 4
FEATURE [App::DocumentObjectGroupPython] Cd_element001  label="Cd_element : 1"  # scripted group (container) (typed FeaturePython)
  n = 1
  ref = Cd_element
FEATURE [App::DocumentObjectGroupPython] Te_element001  label="Te_element : 1"  # scripted group (container) (typed FeaturePython)
  n = 1
  ref = Te_element
FEATURE [App::DocumentObjectGroupPython] G4_CADMIUM_TELLURIDE  # scripted group (container) (typed FeaturePython)
  Dunit = g/cm3
  Dvalue = 6.2
  Group = -> [Cd_element001,Te_element001]
  conduct = 2
  density = 1
  expand = 3
  formula = G4_CADMIUM_TELLURIDE
  name = G4_CADMIUM_TELLURIDE
  specific = 4
FEATURE [App::DocumentObjectGroupPython] Cd_element002  label="Cd_element : 002"  # scripted group (container) (typed FeaturePython)
  n = 1
  ref = Cd_element
FEATURE [App::DocumentObjectGroupPython] W_element001  label="W_element : 1"  # scripted group (container) (typed FeaturePython)
  n = 1
  ref = W_element
FEATURE [App::DocumentObjectGroupPython] O_element020  label="O_element : 008"  # scripted group (container) (typed FeaturePython)
  n = 4
  ref = O_element
FEATURE [App::DocumentObjectGroupPython] G4_CADMIUM_TUNGSTATE  # scripted group (container) (typed FeaturePython)
  Dunit = g/cm3
  Dvalue = 7.9
  Group = -> [Cd_element002,W_element001,O_element020]
  conduct = 2
  density = 1
  expand = 3
  formula = G4_CADMIUM_TUNGSTATE
  name = G4_CADMIUM_TUNGSTATE
  specific = 4
FEATURE [App::DocumentObjectGroupPython] Ca_element005  label="Ca_element : 1"  # scripted group (container) (typed FeaturePython)
  n = 1
  ref = Ca_element
FEATURE [App::DocumentObjectGroupPython] C_element022  label="C_element : 009"  # scripted group (container) (typed FeaturePython)
  n = 1
  ref = C_element
FEATURE [App::DocumentObjectGroupPython] O_element021  label="O_element : 009"  # scripted group (container) (typed FeaturePython)
  n = 3
  ref = O_element
FEATURE [App::DocumentObjectGroupPython] G4_CALCIUM_CARBONATE  # scripted group (container) (typed FeaturePython)
  Dunit = g/cm3
  Dvalue = 2.8
  Group = -> [Ca_element005,C_element022,O_element021]
  conduct = 2
  density = 1
  expand = 3
  formula = G4_CALCIUM_CARBONATE
  name = G4_CALCIUM_CARBONATE
  specific = 4
FEATURE [App::DocumentObjectGroupPython] Ca_element006  label="Ca_element : 002"  # scripted group (container) (typed FeaturePython)
  n = 1
  ref = Ca_element
FEATURE [App::DocumentObjectGroupPython] F_element005  label="F_element : 003"  # scripted group (container) (typed FeaturePython)
  n = 2
  ref = F_element
FEATURE [App::DocumentObjectGroupPython] G4_CALCIUM_FLUORIDE  # scripted group (container) (typed FeaturePython)
  Dunit = g/cm3
  Dvalue = 3.18
  Group = -> [Ca_element006,F_element005]
  conduct = 2
  density = 1
  expand = 3
  formula = G4_CALCIUM_FLUORIDE
  name = G4_CALCIUM_FLUORIDE
  specific = 4
FEATURE [App::DocumentObjectGroupPython] Ca_element007  label="Ca_element : 003"  # scripted group (container) (typed FeaturePython)
  n = 1
  ref = Ca_element
FEATURE [App::DocumentObjectGroupPython] O_element022  label="O_element : 010"  # scripted group (container) (typed FeaturePython)
  n = 1
  ref = O_element
FEATURE [App::DocumentObjectGroupPython] G4_CALCIUM_OXIDE  # scripted group (container) (typed FeaturePython)
  Dunit = g/cm3
  Dvalue = 3.3
  Group = -> [Ca_element007,O_element022]
  conduct = 2
  density = 1
  expand = 3
  formula = G4_CALCIUM_OXIDE
  name = G4_CALCIUM_OXIDE
  specific = 4
FEATURE [App::DocumentObjectGroupPython] Ca_element008  label="Ca_element : 004"  # scripted group (container) (typed FeaturePython)
  n = 1
  ref = Ca_element
FEATURE [App::DocumentObjectGroupPython] S_element007  label="S_element : 002"  # scripted group (container) (typed FeaturePython)
  n = 1
  ref = S_element
FEATURE [App::DocumentObjectGroupPython] O_element023  label="O_element : 011"  # scripted group (container) (typed FeaturePython)
  n = 4
  ref = O_element
FEATURE [App::DocumentObjectGroupPython] G4_CALCIUM_SULFATE  # scripted group (container) (typed FeaturePython)
  Dunit = g/cm3
  Dvalue = 2.96
  Group = -> [Ca_element008,S_element007,O_element023]
  conduct = 2
  density = 1
  expand = 3
  formula = G4_CALCIUM_SULFATE
  name = G4_CALCIUM_SULFATE
  specific = 4
FEATURE [App::DocumentObjectGroupPython] Ca_element009  label="Ca_element : 005"  # scripted group (container) (typed FeaturePython)
  n = 1
  ref = Ca_element
FEATURE [App::DocumentObjectGroupPython] W_element002  label="W_element : 002"  # scripted group (container) (typed FeaturePython)
  n = 1
  ref = W_element
FEATURE [App::DocumentObjectGroupPython] O_element024  label="O_element : 012"  # scripted group (container) (typed FeaturePython)
  n = 4
  ref = O_element
FEATURE [App::DocumentObjectGroupPython] G4_CALCIUM_TUNGSTATE  # scripted group (container) (typed FeaturePython)
  Dunit = g/cm3
  Dvalue = 6.062
  Group = -> [Ca_element009,W_element002,O_element024]
  conduct = 2
  density = 1
  expand = 3
  formula = G4_CALCIUM_TUNGSTATE
  name = G4_CALCIUM_TUNGSTATE
  specific = 4
FEATURE [App::DocumentObjectGroupPython] C_element023  label="C_element : 010"  # scripted group (container) (typed FeaturePython)
  n = 1
  ref = C_element
FEATURE [App::DocumentObjectGroupPython] O_element025  label="O_element : 013"  # scripted group (container) (typed FeaturePython)
  n = 2
  ref = O_element
FEATURE [App::DocumentObjectGroupPython] G4_CARBON_DIOXIDE  # scripted group (container) (typed FeaturePython)
  Dunit = g/cm3
  Dvalue = 0.00184212
  Group = -> [C_element023,O_element025]
  conduct = 2
  density = 1
  expand = 3
  formula = G4_CARBON_DIOXIDE
  name = G4_CARBON_DIOXIDE
  specific = 4
FEATURE [App::DocumentObjectGroupPython] C_element024  label="C_element : 011"  # scripted group (container) (typed FeaturePython)
  n = 1
  ref = C_element
FEATURE [App::DocumentObjectGroupPython] Cl_element004  label="Cl_element : 4"  # scripted group (container) (typed FeaturePython)
  n = 4
  ref = Cl_element
FEATURE [App::DocumentObjectGroupPython] G4_CARBON_TETRACHLORIDE  # scripted group (container) (typed FeaturePython)
  Dunit = g/cm3
  Dvalue = 1.594
  Group = -> [C_element024,Cl_element004]
  conduct = 2
  density = 1
  expand = 3
  formula = G4_CARBON_TETRACHLORIDE
  name = G4_CARBON_TETRACHLORIDE
  specific = 4
FEATURE [App::DocumentObjectGroupPython] C_element025  label="C_element : 012"  # scripted group (container) (typed FeaturePython)
  n = 6
  ref = C_element
FEATURE [App::DocumentObjectGroupPython] H_element021  label="H_element : 012"  # scripted group (container) (typed FeaturePython)
  n = 10
  ref = H_element
FEATURE [App::DocumentObjectGroupPython] O_element026  label="O_element : 5"  # scripted group (container) (typed FeaturePython)
  n = 5
  ref = O_element
FEATURE [App::DocumentObjectGroupPython] G4_CELLULOSE_CELLOPHANE  # scripted group (container) (typed FeaturePython)
  Dunit = g/cm3
  Dvalue = 1.42
  Group = -> [C_element025,H_element021,O_element026]
  conduct = 2
  density = 1
  expand = 3
  formula = G4_CELLULOSE_CELLOPHANE
  name = G4_CELLULOSE_CELLOPHANE
  specific = 4
FEATURE [App::DocumentObjectGroupPython] H_element022  label="H_element : 0.067"  # scripted group (container) (typed FeaturePython)
  n = 0.067125
FEATURE [App::DocumentObjectGroupPython] C_element026  label="C_element : 0.545"  # scripted group (container) (typed FeaturePython)
  n = 0.545403
FEATURE [App::DocumentObjectGroupPython] O_element027  label="O_element : 0.387"  # scripted group (container) (typed FeaturePython)
  n = 0.387472
FEATURE [App::DocumentObjectGroupPython] G4_CELLULOSE_BUTYRATE  # scripted group (container) (typed FeaturePython)
  Dunit = g/cm3
  Dvalue = 1.2
  Group = -> [H_element022,C_element026,O_element027]
  conduct = 2
  density = 1
  expand = 3
  formula = G4_CELLULOSE_BUTYRATE
  name = G4_CELLULOSE_BUTYRATE
  specific = 4
FEATURE [App::DocumentObjectGroupPython] H_element023  label="H_element : 0.029"  # scripted group (container) (typed FeaturePython)
  n = 0.029216
FEATURE [App::DocumentObjectGroupPython] C_element027  label="C_element : 0.271"  # scripted group (container) (typed FeaturePython)
  n = 0.271296
FEATURE [App::DocumentObjectGroupPython] N_element013  label="N_element : 0.121"  # scripted group (container) (typed FeaturePython)
  n = 0.121276
FEATURE [App::DocumentObjectGroupPython] O_element028  label="O_element : 0.578"  # scripted group (container) (typed FeaturePython)
  n = 0.578212
FEATURE [App::DocumentObjectGroupPython] G4_CELLULOSE_NITRATE  # scripted group (container) (typed FeaturePython)
  Dunit = g/cm3
  Dvalue = 1.49
  Group = -> [H_element023,C_element027,N_element013,O_element028]
  conduct = 2
  density = 1
  expand = 3
  formula = G4_CELLULOSE_NITRATE
  name = G4_CELLULOSE_NITRATE
  specific = 4
FEATURE [App::DocumentObjectGroupPython] H_element024  label="H_element : 0.108"  # scripted group (container) (typed FeaturePython)
  n = 0.107596
FEATURE [App::DocumentObjectGroupPython] N_element014  label="N_element : 0.001"  # scripted group (container) (typed FeaturePython)
  n = 0.0008
FEATURE [App::DocumentObjectGroupPython] O_element029  label="O_element : 0.875"  # scripted group (container) (typed FeaturePython)
  n = 0.874976
FEATURE [App::DocumentObjectGroupPython] S_element008  label="S_element : 0.015"  # scripted group (container) (typed FeaturePython)
  n = 0.014627
FEATURE [App::DocumentObjectGroupPython] Ce_element001  label="Ce_element : 0.002"  # scripted group (container) (typed FeaturePython)
  n = 0.002001
FEATURE [App::DocumentObjectGroupPython] G4_CERIC_SULFATE  # scripted group (container) (typed FeaturePython)
  Dunit = g/cm3
  Dvalue = 1.03
  Group = -> [H_element024,N_element014,O_element029,S_element008,Ce_element001]
  conduct = 2
  density = 1
  expand = 3
  formula = G4_CERIC_SULFATE
  name = G4_CERIC_SULFATE
  specific = 4
FEATURE [App::DocumentObjectGroupPython] Cs_element001  label="Cs_element : 1"  # scripted group (container) (typed FeaturePython)
  n = 1
  ref = Cs_element
FEATURE [App::DocumentObjectGroupPython] F_element006  label="F_element : 1"  # scripted group (container) (typed FeaturePython)
  n = 1
  ref = F_element
FEATURE [App::DocumentObjectGroupPython] G4_CESIUM_FLUORIDE  # scripted group (container) (typed FeaturePython)
  Dunit = g/cm3
  Dvalue = 4.115
  Group = -> [Cs_element001,F_element006]
  conduct = 2
  density = 1
  expand = 3
  formula = G4_CESIUM_FLUORIDE
  name = G4_CESIUM_FLUORIDE
  specific = 4
FEATURE [App::DocumentObjectGroupPython] Cs_element002  label="Cs_element : 002"  # scripted group (container) (typed FeaturePython)
  n = 1
  ref = Cs_element
FEATURE [App::DocumentObjectGroupPython] I_element001  label="I_element : 1"  # scripted group (container) (typed FeaturePython)
  n = 1
  ref = I_element
FEATURE [App::DocumentObjectGroupPython] G4_CESIUM_IODIDE  # scripted group (container) (typed FeaturePython)
  Dunit = g/cm3
  Dvalue = 4.51
  Group = -> [Cs_element002,I_element001]
  conduct = 2
  density = 1
  expand = 3
  formula = G4_CESIUM_IODIDE
  name = G4_CESIUM_IODIDE
  specific = 4
FEATURE [App::DocumentObjectGroupPython] C_element028  label="C_element : 013"  # scripted group (container) (typed FeaturePython)
  n = 6
  ref = C_element
FEATURE [App::DocumentObjectGroupPython] H_element025  label="H_element : 013"  # scripted group (container) (typed FeaturePython)
  n = 5
  ref = H_element
FEATURE [App::DocumentObjectGroupPython] Cl_element005  label="Cl_element : 1"  # scripted group (container) (typed FeaturePython)
  n = 1
  ref = Cl_element
FEATURE [App::DocumentObjectGroupPython] G4_CHLOROBENZENE  # scripted group (container) (typed FeaturePython)
  Dunit = g/cm3
  Dvalue = 1.1058
  Group = -> [C_element028,H_element025,Cl_element005]
  conduct = 2
  density = 1
  expand = 3
  formula = G4_CHLOROBENZENE
  name = G4_CHLOROBENZENE
  specific = 4
FEATURE [App::DocumentObjectGroupPython] C_element029  label="C_element : 014"  # scripted group (container) (typed FeaturePython)
  n = 1
  ref = C_element
FEATURE [App::DocumentObjectGroupPython] H_element026  label="H_element : 1"  # scripted group (container) (typed FeaturePython)
  n = 1
  ref = H_element
FEATURE [App::DocumentObjectGroupPython] Cl_element006  label="Cl_element : 3"  # scripted group (container) (typed FeaturePython)
  n = 3
  ref = Cl_element
FEATURE [App::DocumentObjectGroupPython] G4_CHLOROFORM  # scripted group (container) (typed FeaturePython)
  Dunit = g/cm3
  Dvalue = 1.4832
  Group = -> [C_element029,H_element026,Cl_element006]
  conduct = 2
  density = 1
  expand = 3
  formula = G4_CHLOROFORM
  name = G4_CHLOROFORM
  specific = 4
FEATURE [App::DocumentObjectGroupPython] H_element027  label="H_element : 0.010"  # scripted group (container) (typed FeaturePython)
  n = 0.01
FEATURE [App::DocumentObjectGroupPython] C_element030  label="C_element : 0.001"  # scripted group (container) (typed FeaturePython)
  n = 0.001
FEATURE [App::DocumentObjectGroupPython] O_element030  label="O_element : 0.529"  # scripted group (container) (typed FeaturePython)
  n = 0.529107
FEATURE [App::DocumentObjectGroupPython] Na_element005  label="Na_element : 0.016"  # scripted group (container) (typed FeaturePython)
  n = 0.016
FEATURE [App::DocumentObjectGroupPython] Mg_element003  label="Mg_element : 0.004"  # scripted group (container) (typed FeaturePython)
  n = 0.002
FEATURE [App::DocumentObjectGroupPython] Al_element002  label="Al_element : 0.034"  # scripted group (container) (typed FeaturePython)
  n = 0.033872
FEATURE [App::DocumentObjectGroupPython] Si_element002  label="Si_element : 0.337"  # scripted group (container) (typed FeaturePython)
  n = 0.337021
FEATURE [App::DocumentObjectGroupPython] K_element003  label="K_element : 0.013"  # scripted group (container) (typed FeaturePython)
  n = 0.013
FEATURE [App::DocumentObjectGroupPython] Ca_element010  label="Ca_element : 0.044"  # scripted group (container) (typed FeaturePython)
  n = 0.044
FEATURE [App::DocumentObjectGroupPython] Fe_element002  label="Fe_element : 0.014"  # scripted group (container) (typed FeaturePython)
  n = 0.014
FEATURE [App::DocumentObjectGroupPython] G4_CONCRETE  # scripted group (container) (typed FeaturePython)
  Dunit = g/cm3
  Dvalue = 2.3
  Group = -> [H_element027,C_element030,O_element030,Na_element005,Mg_element003,Al_element002,Si_element002,K_element003,Ca_element010,Fe_element002]
  conduct = 2
  density = 1
  expand = 3
  formula = G4_CONCRETE
  name = G4_CONCRETE
  specific = 4
FEATURE [App::DocumentObjectGroupPython] C_element031  label="C_element : 015"  # scripted group (container) (typed FeaturePython)
  n = 6
  ref = C_element
FEATURE [App::DocumentObjectGroupPython] H_element028  label="H_element : 12"  # scripted group (container) (typed FeaturePython)
  n = 12
  ref = H_element
FEATURE [App::DocumentObjectGroupPython] G4_CYCLOHEXANE  # scripted group (container) (typed FeaturePython)
  Dunit = g/cm3
  Dvalue = 0.779
  Group = -> [C_element031,H_element028]
  conduct = 2
  density = 1
  expand = 3
  formula = G4_CYCLOHEXANE
  name = G4_CYCLOHEXANE
  specific = 4
FEATURE [App::DocumentObjectGroupPython] C_element032  label="C_element : 016"  # scripted group (container) (typed FeaturePython)
  n = 6
  ref = C_element
FEATURE [App::DocumentObjectGroupPython] H_element029  label="H_element : 4"  # scripted group (container) (typed FeaturePython)
  n = 4
  ref = H_element
FEATURE [App::DocumentObjectGroupPython] Cl_element007  label="Cl_element : 2"  # scripted group (container) (typed FeaturePython)
  n = 2
  ref = Cl_element
FEATURE [App::DocumentObjectGroupPython] G4_1_2_DICHLOROBENZENE  label="G4_1.2-DICHLOROBENZENE"  # scripted group (container) (typed FeaturePython)
  Dunit = g/cm3
  Dvalue = 1.3048
  Group = -> [C_element032,H_element029,Cl_element007]
  conduct = 2
  density = 1
  expand = 3
  formula = G4_1.2-DICHLOROBENZENE
  name = G4_1.2-DICHLOROBENZENE
  specific = 4
FEATURE [App::DocumentObjectGroupPython] C_element033  label="C_element : 017"  # scripted group (container) (typed FeaturePython)
  n = 4
  ref = C_element
FEATURE [App::DocumentObjectGroupPython] H_element030  label="H_element : 8"  # scripted group (container) (typed FeaturePython)
  n = 8
  ref = H_element
FEATURE [App::DocumentObjectGroupPython] O_element031  label="O_element : 014"  # scripted group (container) (typed FeaturePython)
  n = 1
  ref = O_element
FEATURE [App::DocumentObjectGroupPython] Cl_element008  label="Cl_element : 005"  # scripted group (container) (typed FeaturePython)
  n = 2
  ref = Cl_element
FEATURE [App::DocumentObjectGroupPython] G4_DICHLORODIETHYL_ETHER  # scripted group (container) (typed FeaturePython)
  Dunit = g/cm3
  Dvalue = 1.2199
  Group = -> [C_element033,H_element030,O_element031,Cl_element008]
  conduct = 2
  density = 1
  expand = 3
  formula = G4_DICHLORODIETHYL_ETHER
  name = G4_DICHLORODIETHYL_ETHER
  specific = 4
FEATURE [App::DocumentObjectGroupPython] C_element034  label="C_element : 018"  # scripted group (container) (typed FeaturePython)
  n = 2
  ref = C_element
FEATURE [App::DocumentObjectGroupPython] H_element031  label="H_element : 014"  # scripted group (container) (typed FeaturePython)
  n = 4
  ref = H_element
FEATURE [App::DocumentObjectGroupPython] Cl_element009  label="Cl_element : 006"  # scripted group (container) (typed FeaturePython)
  n = 2
  ref = Cl_element
FEATURE [App::DocumentObjectGroupPython] G4_1_2_DICHLOROETHANE  label="G4_1.2-DICHLOROETHANE"  # scripted group (container) (typed FeaturePython)
  Dunit = g/cm3
  Dvalue = 1.2351
  Group = -> [C_element034,H_element031,Cl_element009]
  conduct = 2
  density = 1
  expand = 3
  formula = G4_1.2-DICHLOROETHANE
  name = G4_1.2-DICHLOROETHANE
  specific = 4
FEATURE [App::DocumentObjectGroupPython] C_element035  label="C_element : 019"  # scripted group (container) (typed FeaturePython)
  n = 4
  ref = C_element
FEATURE [App::DocumentObjectGroupPython] H_element032  label="H_element : 015"  # scripted group (container) (typed FeaturePython)
  n = 10
  ref = H_element
FEATURE [App::DocumentObjectGroupPython] O_element032  label="O_element : 015"  # scripted group (container) (typed FeaturePython)
  n = 1
  ref = O_element
FEATURE [App::DocumentObjectGroupPython] G4_DIETHYL_ETHER  # scripted group (container) (typed FeaturePython)
  Dunit = g/cm3
  Dvalue = 0.71378
  Group = -> [C_element035,H_element032,O_element032]
  conduct = 2
  density = 1
  expand = 3
  formula = G4_DIETHYL_ETHER
  name = G4_DIETHYL_ETHER
  specific = 4
FEATURE [App::DocumentObjectGroupPython] C_element036  label="C_element : 020"  # scripted group (container) (typed FeaturePython)
  n = 3
  ref = C_element
FEATURE [App::DocumentObjectGroupPython] H_element033  label="H_element : 016"  # scripted group (container) (typed FeaturePython)
  n = 7
  ref = H_element
FEATURE [App::DocumentObjectGroupPython] N_element015  label="N_element : 008"  # scripted group (container) (typed FeaturePython)
  n = 1
  ref = N_element
FEATURE [App::DocumentObjectGroupPython] O_element033  label="O_element : 016"  # scripted group (container) (typed FeaturePython)
  n = 1
  ref = O_element
FEATURE [App::DocumentObjectGroupPython] G4_N_N_DIMETHYL_FORMAMIDE  label="G4_N.N-DIMETHYL_FORMAMIDE"  # scripted group (container) (typed FeaturePython)
  Dunit = g/cm3
  Dvalue = 0.9487
  Group = -> [C_element036,H_element033,N_element015,O_element033]
  conduct = 2
  density = 1
  expand = 3
  formula = G4_N.N-DIMETHYL_FORMAMIDE
  name = G4_N.N-DIMETHYL_FORMAMIDE
  specific = 4
FEATURE [App::DocumentObjectGroupPython] C_element037  label="C_element : 021"  # scripted group (container) (typed FeaturePython)
  n = 2
  ref = C_element
FEATURE [App::DocumentObjectGroupPython] H_element034  label="H_element : 017"  # scripted group (container) (typed FeaturePython)
  n = 6
  ref = H_element
FEATURE [App::DocumentObjectGroupPython] O_element034  label="O_element : 017"  # scripted group (container) (typed FeaturePython)
  n = 1
  ref = O_element
FEATURE [App::DocumentObjectGroupPython] S_element009  label="S_element : 003"  # scripted group (container) (typed FeaturePython)
  n = 1
  ref = S_element
FEATURE [App::DocumentObjectGroupPython] G4_DIMETHYL_SULFOXIDE  # scripted group (container) (typed FeaturePython)
  Dunit = g/cm3
  Dvalue = 1.1014
  Group = -> [C_element037,H_element034,O_element034,S_element009]
  conduct = 2
  density = 1
  expand = 3
  formula = G4_DIMETHYL_SULFOXIDE
  name = G4_DIMETHYL_SULFOXIDE
  specific = 4
FEATURE [App::DocumentObjectGroupPython] C_element038  label="C_element : 022"  # scripted group (container) (typed FeaturePython)
  n = 2
  ref = C_element
FEATURE [App::DocumentObjectGroupPython] H_element035  label="H_element : 018"  # scripted group (container) (typed FeaturePython)
  n = 6
  ref = H_element
FEATURE [App::DocumentObjectGroupPython] G4_ETHANE  # scripted group (container) (typed FeaturePython)
  Dunit = g/cm3
  Dvalue = 0.00125324
  Group = -> [C_element038,H_element035]
  conduct = 2
  density = 1
  expand = 3
  formula = G4_ETHANE
  name = G4_ETHANE
  specific = 4
FEATURE [App::DocumentObjectGroupPython] C_element039  label="C_element : 023"  # scripted group (container) (typed FeaturePython)
  n = 2
  ref = C_element
FEATURE [App::DocumentObjectGroupPython] H_element036  label="H_element : 019"  # scripted group (container) (typed FeaturePython)
  n = 6
  ref = H_element
FEATURE [App::DocumentObjectGroupPython] O_element035  label="O_element : 018"  # scripted group (container) (typed FeaturePython)
  n = 1
  ref = O_element
FEATURE [App::DocumentObjectGroupPython] G4_ETHYL_ALCOHOL  # scripted group (container) (typed FeaturePython)
  Dunit = g/cm3
  Dvalue = 0.7893
  Group = -> [C_element039,H_element036,O_element035]
  conduct = 2
  density = 1
  expand = 3
  formula = G4_ETHYL_ALCOHOL
  name = G4_ETHYL_ALCOHOL
  specific = 4
FEATURE [App::DocumentObjectGroupPython] H_element037  label="H_element : 0.090"  # scripted group (container) (typed FeaturePython)
  n = 0.090027
FEATURE [App::DocumentObjectGroupPython] C_element040  label="C_element : 0.585"  # scripted group (container) (typed FeaturePython)
  n = 0.585182
FEATURE [App::DocumentObjectGroupPython] O_element036  label="O_element : 0.325"  # scripted group (container) (typed FeaturePython)
  n = 0.324791
FEATURE [App::DocumentObjectGroupPython] G4_ETHYL_CELLULOSE  # scripted group (container) (typed FeaturePython)
  Dunit = g/cm3
  Dvalue = 1.13
  Group = -> [H_element037,C_element040,O_element036]
  conduct = 2
  density = 1
  expand = 3
  formula = G4_ETHYL_CELLULOSE
  name = G4_ETHYL_CELLULOSE
  specific = 4
FEATURE [App::DocumentObjectGroupPython] C_element041  label="C_element : 024"  # scripted group (container) (typed FeaturePython)
  n = 2
  ref = C_element
FEATURE [App::DocumentObjectGroupPython] H_element038  label="H_element : 020"  # scripted group (container) (typed FeaturePython)
  n = 4
  ref = H_element
FEATURE [App::DocumentObjectGroupPython] G4_ETHYLENE  # scripted group (container) (typed FeaturePython)
  Dunit = g/cm3
  Dvalue = 0.00117497
  Group = -> [C_element041,H_element038]
  conduct = 2
  density = 1
  expand = 3
  formula = G4_ETHYLENE
  name = G4_ETHYLENE
  specific = 4
FEATURE [App::DocumentObjectGroupPython] H_element039  label="H_element : 0.096"  # scripted group (container) (typed FeaturePython)
  n = 0.096
FEATURE [App::DocumentObjectGroupPython] C_element042  label="C_element : 0.195"  # scripted group (container) (typed FeaturePython)
  n = 0.195
FEATURE [App::DocumentObjectGroupPython] N_element016  label="N_element : 0.057"  # scripted group (container) (typed FeaturePython)
  n = 0.057
FEATURE [App::DocumentObjectGroupPython] O_element037  label="O_element : 0.646"  # scripted group (container) (typed FeaturePython)
  n = 0.646
FEATURE [App::DocumentObjectGroupPython] Na_element006  label="Na_element : 0.017"  # scripted group (container) (typed FeaturePython)
  n = 0.001
FEATURE [App::DocumentObjectGroupPython] P_element005  label="P_element : 0.104"  # scripted group (container) (typed FeaturePython)
  n = 0.001
FEATURE [App::DocumentObjectGroupPython] S_element010  label="S_element : 0.016"  # scripted group (container) (typed FeaturePython)
  n = 0.003
FEATURE [App::DocumentObjectGroupPython] Cl_element010  label="Cl_element : 0.005"  # scripted group (container) (typed FeaturePython)
  n = 0.001
FEATURE [App::DocumentObjectGroupPython] G4_EYE_LENS_ICRP  # scripted group (container) (typed FeaturePython)
  Dunit = g/cm3
  Dvalue = 1.07
  Group = -> [H_element039,C_element042,N_element016,O_element037,Na_element006,P_element005,S_element010,Cl_element010]
  conduct = 2
  density = 1
  expand = 3
  formula = G4_EYE_LENS_ICRP
  name = G4_EYE_LENS_ICRP
  specific = 4
FEATURE [App::DocumentObjectGroupPython] Fe_element003  label="Fe_element : 2"  # scripted group (container) (typed FeaturePython)
  n = 2
  ref = Fe_element
FEATURE [App::DocumentObjectGroupPython] O_element038  label="O_element : 019"  # scripted group (container) (typed FeaturePython)
  n = 3
  ref = O_element
FEATURE [App::DocumentObjectGroupPython] G4_FERRIC_OXIDE  # scripted group (container) (typed FeaturePython)
  Dunit = g/cm3
  Dvalue = 5.2
  Group = -> [Fe_element003,O_element038]
  conduct = 2
  density = 1
  expand = 3
  formula = G4_FERRIC_OXIDE
  name = G4_FERRIC_OXIDE
  specific = 4
FEATURE [App::DocumentObjectGroupPython] Fe_element004  label="Fe_element : 1"  # scripted group (container) (typed FeaturePython)
  n = 1
  ref = Fe_element
FEATURE [App::DocumentObjectGroupPython] B_element003  label="B_element : 1"  # scripted group (container) (typed FeaturePython)
  n = 1
  ref = B_element
FEATURE [App::DocumentObjectGroupPython] G4_FERROBORIDE  # scripted group (container) (typed FeaturePython)
  Dunit = g/cm3
  Dvalue = 7.15
  Group = -> [Fe_element004,B_element003]
  conduct = 2
  density = 1
  expand = 3
  formula = G4_FERROBORIDE
  name = G4_FERROBORIDE
  specific = 4
FEATURE [App::DocumentObjectGroupPython] Fe_element005  label="Fe_element : 003"  # scripted group (container) (typed FeaturePython)
  n = 1
  ref = Fe_element
FEATURE [App::DocumentObjectGroupPython] O_element039  label="O_element : 020"  # scripted group (container) (typed FeaturePython)
  n = 1
  ref = O_element
FEATURE [App::DocumentObjectGroupPython] G4_FERROUS_OXIDE  # scripted group (container) (typed FeaturePython)
  Dunit = g/cm3
  Dvalue = 5.7
  Group = -> [Fe_element005,O_element039]
  conduct = 2
  density = 1
  expand = 3
  formula = G4_FERROUS_OXIDE
  name = G4_FERROUS_OXIDE
  specific = 4
FEATURE [App::DocumentObjectGroupPython] H_element040  label="H_element : 0.115"  # scripted group (container) (typed FeaturePython)
  n = 0.108259
FEATURE [App::DocumentObjectGroupPython] N_element017  label="N_element : 0.000"  # scripted group (container) (typed FeaturePython)
  n = 2.7e-05
FEATURE [App::DocumentObjectGroupPython] O_element040  label="O_element : 0.879"  # scripted group (container) (typed FeaturePython)
  n = 0.878636
FEATURE [App::DocumentObjectGroupPython] Na_element007  label="Na_element : 0.000"  # scripted group (container) (typed FeaturePython)
  n = 2.2e-05
FEATURE [App::DocumentObjectGroupPython] S_element011  label="S_element : 0.013"  # scripted group (container) (typed FeaturePython)
  n = 0.012968
FEATURE [App::DocumentObjectGroupPython] Cl_element011  label="Cl_element : 0.000"  # scripted group (container) (typed FeaturePython)
  n = 3.4e-05
FEATURE [App::DocumentObjectGroupPython] Fe_element006  label="Fe_element : 0.000"  # scripted group (container) (typed FeaturePython)
  n = 5.4e-05
FEATURE [App::DocumentObjectGroupPython] G4_FERROUS_SULFATE  # scripted group (container) (typed FeaturePython)
  Dunit = g/cm3
  Dvalue = 1.024
  Group = -> [H_element040,N_element017,O_element040,Na_element007,S_element011,Cl_element011,Fe_element006]
  conduct = 2
  density = 1
  expand = 3
  formula = G4_FERROUS_SULFATE
  name = G4_FERROUS_SULFATE
  specific = 4
FEATURE [App::DocumentObjectGroupPython] C_element043  label="C_element : 0.099"  # scripted group (container) (typed FeaturePython)
  n = 0.099335
FEATURE [App::DocumentObjectGroupPython] F_element007  label="F_element : 0.314"  # scripted group (container) (typed FeaturePython)
  n = 0.314247
FEATURE [App::DocumentObjectGroupPython] Cl_element012  label="Cl_element : 0.586"  # scripted group (container) (typed FeaturePython)
  n = 0.586418
FEATURE [App::DocumentObjectGroupPython] G4_FREON_12  label="G4_FREON-12"  # scripted group (container) (typed FeaturePython)
  Dunit = g/cm3
  Dvalue = 1.12
  Group = -> [C_element043,F_element007,Cl_element012]
  conduct = 2
  density = 1
  expand = 3
  formula = G4_FREON-12
  name = G4_FREON-12
  specific = 4
FEATURE [App::DocumentObjectGroupPython] C_element044  label="C_element : 0.057"  # scripted group (container) (typed FeaturePython)
  n = 0.057245
FEATURE [App::DocumentObjectGroupPython] F_element008  label="F_element : 0.181"  # scripted group (container) (typed FeaturePython)
  n = 0.181096
FEATURE [App::DocumentObjectGroupPython] Br_element001  label="Br_element : 0.762"  # scripted group (container) (typed FeaturePython)
  n = 0.761659
FEATURE [App::DocumentObjectGroupPython] G4_FREON_12B2  label="G4_FREON-12B2"  # scripted group (container) (typed FeaturePython)
  Dunit = g/cm3
  Dvalue = 1.8
  Group = -> [C_element044,F_element008,Br_element001]
  conduct = 2
  density = 1
  expand = 3
  formula = G4_FREON-12B2
  name = G4_FREON-12B2
  specific = 4
FEATURE [App::DocumentObjectGroupPython] C_element045  label="C_element : 0.115"  # scripted group (container) (typed FeaturePython)
  n = 0.114983
FEATURE [App::DocumentObjectGroupPython] F_element009  label="F_element : 0.546"  # scripted group (container) (typed FeaturePython)
  n = 0.545621
FEATURE [App::DocumentObjectGroupPython] Cl_element013  label="Cl_element : 0.339"  # scripted group (container) (typed FeaturePython)
  n = 0.339396
FEATURE [App::DocumentObjectGroupPython] G4_FREON_13  label="G4_FREON-13"  # scripted group (container) (typed FeaturePython)
  Dunit = g/cm3
  Dvalue = 0.95
  Group = -> [C_element045,F_element009,Cl_element013]
  conduct = 2
  density = 1
  expand = 3
  formula = G4_FREON-13
  name = G4_FREON-13
  specific = 4
FEATURE [App::DocumentObjectGroupPython] C_element046  label="C_element : 025"  # scripted group (container) (typed FeaturePython)
  n = 1
  ref = C_element
FEATURE [App::DocumentObjectGroupPython] F_element010  label="F_element : 3"  # scripted group (container) (typed FeaturePython)
  n = 3
  ref = F_element
FEATURE [App::DocumentObjectGroupPython] Br_element002  label="Br_element : 1"  # scripted group (container) (typed FeaturePython)
  n = 1
  ref = Br_element
FEATURE [App::DocumentObjectGroupPython] G4_FREON_13B1  label="G4_FREON-13B1"  # scripted group (container) (typed FeaturePython)
  Dunit = g/cm3
  Dvalue = 1.5
  Group = -> [C_element046,F_element010,Br_element002]
  conduct = 2
  density = 1
  expand = 3
  formula = G4_FREON-13B1
  name = G4_FREON-13B1
  specific = 4
FEATURE [App::DocumentObjectGroupPython] C_element047  label="C_element : 0.061"  # scripted group (container) (typed FeaturePython)
  n = 0.061309
FEATURE [App::DocumentObjectGroupPython] F_element011  label="F_element : 0.291"  # scripted group (container) (typed FeaturePython)
  n = 0.290924
FEATURE [App::DocumentObjectGroupPython] I_element002  label="I_element : 0.648"  # scripted group (container) (typed FeaturePython)
  n = 0.647767
FEATURE [App::DocumentObjectGroupPython] G4_FREON_13I1  label="G4_FREON-13I1"  # scripted group (container) (typed FeaturePython)
  Dunit = g/cm3
  Dvalue = 1.8
  Group = -> [C_element047,F_element011,I_element002]
  conduct = 2
  density = 1
  expand = 3
  formula = G4_FREON-13I1
  name = G4_FREON-13I1
  specific = 4
FEATURE [App::DocumentObjectGroupPython] Gd_element001  label="Gd_element : 2"  # scripted group (container) (typed FeaturePython)
  n = 2
  ref = Gd_element
FEATURE [App::DocumentObjectGroupPython] O_element041  label="O_element : 021"  # scripted group (container) (typed FeaturePython)
  n = 2
  ref = O_element
FEATURE [App::DocumentObjectGroupPython] S_element012  label="S_element : 004"  # scripted group (container) (typed FeaturePython)
  n = 1
  ref = S_element
FEATURE [App::DocumentObjectGroupPython] G4_GADOLINIUM_OXYSULFIDE  # scripted group (container) (typed FeaturePython)
  Dunit = g/cm3
  Dvalue = 7.44
  Group = -> [Gd_element001,O_element041,S_element012]
  conduct = 2
  density = 1
  expand = 3
  formula = G4_GADOLINIUM_OXYSULFIDE
  name = G4_GADOLINIUM_OXYSULFIDE
  specific = 4
FEATURE [App::DocumentObjectGroupPython] Ga_element001  label="Ga_element : 1"  # scripted group (container) (typed FeaturePython)
  n = 1
  ref = Ga_element
FEATURE [App::DocumentObjectGroupPython] As_element001  label="As_element : 1"  # scripted group (container) (typed FeaturePython)
  n = 1
  ref = As_element
FEATURE [App::DocumentObjectGroupPython] G4_GALLIUM_ARSENIDE  # scripted group (container) (typed FeaturePython)
  Dunit = g/cm3
  Dvalue = 5.31
  Group = -> [Ga_element001,As_element001]
  conduct = 2
  density = 1
  expand = 3
  formula = G4_GALLIUM_ARSENIDE
  name = G4_GALLIUM_ARSENIDE
  specific = 4
FEATURE [App::DocumentObjectGroupPython] H_element041  label="H_element : 0.081"  # scripted group (container) (typed FeaturePython)
  n = 0.08118
FEATURE [App::DocumentObjectGroupPython] C_element048  label="C_element : 0.416"  # scripted group (container) (typed FeaturePython)
  n = 0.41606
FEATURE [App::DocumentObjectGroupPython] N_element018  label="N_element : 0.111"  # scripted group (container) (typed FeaturePython)
  n = 0.11124
FEATURE [App::DocumentObjectGroupPython] O_element042  label="O_element : 0.381"  # scripted group (container) (typed FeaturePython)
  n = 0.38064
FEATURE [App::DocumentObjectGroupPython] S_element013  label="S_element : 0.011"  # scripted group (container) (typed FeaturePython)
  n = 0.01088
FEATURE [App::DocumentObjectGroupPython] G4_GEL_PHOTO_EMULSION  # scripted group (container) (typed FeaturePython)
  Dunit = g/cm3
  Dvalue = 1.2914
  Group = -> [H_element041,C_element048,N_element018,O_element042,S_element013]
  conduct = 2
  density = 1
  expand = 3
  formula = G4_GEL_PHOTO_EMULSION
  name = G4_GEL_PHOTO_EMULSION
  specific = 4
FEATURE [App::DocumentObjectGroupPython] B_element004  label="B_element : 0.040"  # scripted group (container) (typed FeaturePython)
  n = 0.0400639
FEATURE [App::DocumentObjectGroupPython] O_element043  label="O_element : 0.540"  # scripted group (container) (typed FeaturePython)
  n = 0.539561
FEATURE [App::DocumentObjectGroupPython] Na_element008  label="Na_element : 0.028"  # scripted group (container) (typed FeaturePython)
  n = 0.0281909
FEATURE [App::DocumentObjectGroupPython] Al_element003  label="Al_element : 0.012"  # scripted group (container) (typed FeaturePython)
  n = 0.011644
FEATURE [App::DocumentObjectGroupPython] Si_element003  label="Si_element : 0.377"  # scripted group (container) (typed FeaturePython)
  n = 0.377219
FEATURE [App::DocumentObjectGroupPython] K_element004  label="K_element : 0.014"  # scripted group (container) (typed FeaturePython)
  n = 0.00332099
FEATURE [App::DocumentObjectGroupPython] G4_Pyrex_Glass  # scripted group (container) (typed FeaturePython)
  Dunit = g/cm3
  Dvalue = 2.23
  Group = -> [B_element004,O_element043,Na_element008,Al_element003,Si_element003,K_element004]
  conduct = 2
  density = 1
  expand = 3
  formula = G4_Pyrex_Glass
  name = G4_Pyrex_Glass
  specific = 4
FEATURE [App::DocumentObjectGroupPython] O_element044  label="O_element : 0.156"  # scripted group (container) (typed FeaturePython)
  n = 0.156453
FEATURE [App::DocumentObjectGroupPython] Si_element004  label="Si_element : 0.081"  # scripted group (container) (typed FeaturePython)
  n = 0.080866
FEATURE [App::DocumentObjectGroupPython] Ti_element001  label="Ti_element : 0.008"  # scripted group (container) (typed FeaturePython)
  n = 0.008092
FEATURE [App::DocumentObjectGroupPython] As_element002  label="As_element : 0.003"  # scripted group (container) (typed FeaturePython)
  n = 0.002651
FEATURE [App::DocumentObjectGroupPython] Pb_element001  label="Pb_element : 0.752"  # scripted group (container) (typed FeaturePython)
  n = 0.751938
FEATURE [App::DocumentObjectGroupPython] G4_GLASS_LEAD  # scripted group (container) (typed FeaturePython)
  Dunit = g/cm3
  Dvalue = 6.22
  Group = -> [O_element044,Si_element004,Ti_element001,As_element002,Pb_element001]
  conduct = 2
  density = 1
  expand = 3
  formula = G4_GLASS_LEAD
  name = G4_GLASS_LEAD
  specific = 4
FEATURE [App::DocumentObjectGroupPython] O_element045  label="O_element : 0.460"  # scripted group (container) (typed FeaturePython)
  n = 0.4598
FEATURE [App::DocumentObjectGroupPython] Na_element009  label="Na_element : 0.096"  # scripted group (container) (typed FeaturePython)
  n = 0.0964411
FEATURE [App::DocumentObjectGroupPython] Si_element005  label="Si_element : 0.378"  # scripted group (container) (typed FeaturePython)
  n = 0.336553
FEATURE [App::DocumentObjectGroupPython] Ca_element011  label="Ca_element : 0.107"  # scripted group (container) (typed FeaturePython)
  n = 0.107205
FEATURE [App::DocumentObjectGroupPython] G4_GLASS_PLATE  # scripted group (container) (typed FeaturePython)
  Dunit = g/cm3
  Dvalue = 2.4
  Group = -> [O_element045,Na_element009,Si_element005,Ca_element011]
  conduct = 2
  density = 1
  expand = 3
  formula = G4_GLASS_PLATE
  name = G4_GLASS_PLATE
  specific = 4
FEATURE [App::DocumentObjectGroupPython] C_element049  label="C_element : 026"  # scripted group (container) (typed FeaturePython)
  n = 5
  ref = C_element
FEATURE [App::DocumentObjectGroupPython] H_element042  label="H_element : 021"  # scripted group (container) (typed FeaturePython)
  n = 10
  ref = H_element
FEATURE [App::DocumentObjectGroupPython] N_element019  label="N_element : 2"  # scripted group (container) (typed FeaturePython)
  n = 2
  ref = N_element
FEATURE [App::DocumentObjectGroupPython] O_element046  label="O_element : 022"  # scripted group (container) (typed FeaturePython)
  n = 3
  ref = O_element
FEATURE [App::DocumentObjectGroupPython] G4_GLUTAMINE  # scripted group (container) (typed FeaturePython)
  Dunit = g/cm3
  Dvalue = 1.46
  Group = -> [C_element049,H_element042,N_element019,O_element046]
  conduct = 2
  density = 1
  expand = 3
  formula = G4_GLUTAMINE
  name = G4_GLUTAMINE
  specific = 4
FEATURE [App::DocumentObjectGroupPython] C_element050  label="C_element : 027"  # scripted group (container) (typed FeaturePython)
  n = 3
  ref = C_element
FEATURE [App::DocumentObjectGroupPython] H_element043  label="H_element : 022"  # scripted group (container) (typed FeaturePython)
  n = 8
  ref = H_element
FEATURE [App::DocumentObjectGroupPython] O_element047  label="O_element : 023"  # scripted group (container) (typed FeaturePython)
  n = 3
  ref = O_element
FEATURE [App::DocumentObjectGroupPython] G4_GLYCEROL  # scripted group (container) (typed FeaturePython)
  Dunit = g/cm3
  Dvalue = 1.2613
  Group = -> [C_element050,H_element043,O_element047]
  conduct = 2
  density = 1
  expand = 3
  formula = G4_GLYCEROL
  name = G4_GLYCEROL
  specific = 4
FEATURE [App::DocumentObjectGroupPython] C_element051  label="C_element : 028"  # scripted group (container) (typed FeaturePython)
  n = 5
  ref = C_element
FEATURE [App::DocumentObjectGroupPython] H_element044  label="H_element : 023"  # scripted group (container) (typed FeaturePython)
  n = 5
  ref = H_element
FEATURE [App::DocumentObjectGroupPython] N_element020  label="N_element : 009"  # scripted group (container) (typed FeaturePython)
  n = 5
  ref = N_element
FEATURE [App::DocumentObjectGroupPython] O_element048  label="O_element : 024"  # scripted group (container) (typed FeaturePython)
  n = 1
  ref = O_element
FEATURE [App::DocumentObjectGroupPython] G4_GUANINE  # scripted group (container) (typed FeaturePython)
  Dunit = g/cm3
  Dvalue = 2.2
  Group = -> [C_element051,H_element044,N_element020,O_element048]
  conduct = 2
  density = 1
  expand = 3
  formula = G4_GUANINE
  name = G4_GUANINE
  specific = 4
FEATURE [App::DocumentObjectGroupPython] Ca_element012  label="Ca_element : 006"  # scripted group (container) (typed FeaturePython)
  n = 1
  ref = Ca_element
FEATURE [App::DocumentObjectGroupPython] S_element014  label="S_element : 005"  # scripted group (container) (typed FeaturePython)
  n = 1
  ref = S_element
FEATURE [App::DocumentObjectGroupPython] O_element049  label="O_element : 6"  # scripted group (container) (typed FeaturePython)
  n = 6
  ref = O_element
FEATURE [App::DocumentObjectGroupPython] H_element045  label="H_element : 024"  # scripted group (container) (typed FeaturePython)
  n = 4
  ref = H_element
FEATURE [App::DocumentObjectGroupPython] G4_GYPSUM  # scripted group (container) (typed FeaturePython)
  Dunit = g/cm3
  Dvalue = 2.32
  Group = -> [Ca_element012,S_element014,O_element049,H_element045]
  conduct = 2
  density = 1
  expand = 3
  formula = G4_GYPSUM
  name = G4_GYPSUM
  specific = 4
FEATURE [App::DocumentObjectGroupPython] C_element052  label="C_element : 7"  # scripted group (container) (typed FeaturePython)
  n = 7
  ref = C_element
FEATURE [App::DocumentObjectGroupPython] H_element046  label="H_element : 16"  # scripted group (container) (typed FeaturePython)
  n = 16
  ref = H_element
FEATURE [App::DocumentObjectGroupPython] G4_N_HEPTANE  label="G4_N-HEPTANE"  # scripted group (container) (typed FeaturePython)
  Dunit = g/cm3
  Dvalue = 0.68376
  Group = -> [C_element052,H_element046]
  conduct = 2
  density = 1
  expand = 3
  formula = G4_N-HEPTANE
  name = G4_N-HEPTANE
  specific = 4
FEATURE [App::DocumentObjectGroupPython] C_element053  label="C_element : 029"  # scripted group (container) (typed FeaturePython)
  n = 6
  ref = C_element
FEATURE [App::DocumentObjectGroupPython] H_element047  label="H_element : 14"  # scripted group (container) (typed FeaturePython)
  n = 14
  ref = H_element
FEATURE [App::DocumentObjectGroupPython] G4_N_HEXANE  label="G4_N-HEXANE"  # scripted group (container) (typed FeaturePython)
  Dunit = g/cm3
  Dvalue = 0.6603
  Group = -> [C_element053,H_element047]
  conduct = 2
  density = 1
  expand = 3
  formula = G4_N-HEXANE
  name = G4_N-HEXANE
  specific = 4
FEATURE [App::DocumentObjectGroupPython] C_element054  label="C_element : 22"  # scripted group (container) (typed FeaturePython)
  n = 22
  ref = C_element
FEATURE [App::DocumentObjectGroupPython] H_element048  label="H_element : 025"  # scripted group (container) (typed FeaturePython)
  n = 10
  ref = H_element
FEATURE [App::DocumentObjectGroupPython] N_element021  label="N_element : 010"  # scripted group (container) (typed FeaturePython)
  n = 2
  ref = N_element
FEATURE [App::DocumentObjectGroupPython] O_element050  label="O_element : 025"  # scripted group (container) (typed FeaturePython)
  n = 5
  ref = O_element
FEATURE [App::DocumentObjectGroupPython] G4_KAPTON  # scripted group (container) (typed FeaturePython)
  Dunit = g/cm3
  Dvalue = 1.42
  Group = -> [C_element054,H_element048,N_element021,O_element050]
  conduct = 2
  density = 1
  expand = 3
  formula = G4_KAPTON
  name = G4_KAPTON
  specific = 4
FEATURE [App::DocumentObjectGroupPython] La_element001  label="La_element : 1"  # scripted group (container) (typed FeaturePython)
  n = 1
  ref = La_element
FEATURE [App::DocumentObjectGroupPython] Br_element003  label="Br_element : 002"  # scripted group (container) (typed FeaturePython)
  n = 1
  ref = Br_element
FEATURE [App::DocumentObjectGroupPython] O_element051  label="O_element : 026"  # scripted group (container) (typed FeaturePython)
  n = 1
  ref = O_element
FEATURE [App::DocumentObjectGroupPython] G4_LANTHANUM_OXYBROMIDE  # scripted group (container) (typed FeaturePython)
  Dunit = g/cm3
  Dvalue = 6.28
  Group = -> [La_element001,Br_element003,O_element051]
  conduct = 2
  density = 1
  expand = 3
  formula = G4_LANTHANUM_OXYBROMIDE
  name = G4_LANTHANUM_OXYBROMIDE
  specific = 4
FEATURE [App::DocumentObjectGroupPython] La_element002  label="La_element : 2"  # scripted group (container) (typed FeaturePython)
  n = 2
  ref = La_element
FEATURE [App::DocumentObjectGroupPython] O_element052  label="O_element : 027"  # scripted group (container) (typed FeaturePython)
  n = 2
  ref = O_element
FEATURE [App::DocumentObjectGroupPython] S_element015  label="S_element : 006"  # scripted group (container) (typed FeaturePython)
  n = 1
  ref = S_element
FEATURE [App::DocumentObjectGroupPython] G4_LANTHANUM_OXYSULFIDE  # scripted group (container) (typed FeaturePython)
  Dunit = g/cm3
  Dvalue = 5.86
  Group = -> [La_element002,O_element052,S_element015]
  conduct = 2
  density = 1
  expand = 3
  formula = G4_LANTHANUM_OXYSULFIDE
  name = G4_LANTHANUM_OXYSULFIDE
  specific = 4
FEATURE [App::DocumentObjectGroupPython] O_element053  label="O_element : 0.072"  # scripted group (container) (typed FeaturePython)
  n = 0.071682
FEATURE [App::DocumentObjectGroupPython] Pb_element002  label="Pb_element : 0.928"  # scripted group (container) (typed FeaturePython)
  n = 0.928318
FEATURE [App::DocumentObjectGroupPython] G4_LEAD_OXIDE  # scripted group (container) (typed FeaturePython)
  Dunit = g/cm3
  Dvalue = 9.53
  Group = -> [O_element053,Pb_element002]
  conduct = 2
  density = 1
  expand = 3
  formula = G4_LEAD_OXIDE
  name = G4_LEAD_OXIDE
  specific = 4
FEATURE [App::DocumentObjectGroupPython] Li_element001  label="Li_element : 1"  # scripted group (container) (typed FeaturePython)
  n = 1
  ref = Li_element
FEATURE [App::DocumentObjectGroupPython] N_element022  label="N_element : 011"  # scripted group (container) (typed FeaturePython)
  n = 1
  ref = N_element
FEATURE [App::DocumentObjectGroupPython] H_element049  label="H_element : 026"  # scripted group (container) (typed FeaturePython)
  n = 2
  ref = H_element
FEATURE [App::DocumentObjectGroupPython] G4_LITHIUM_AMIDE  # scripted group (container) (typed FeaturePython)
  Dunit = g/cm3
  Dvalue = 1.178
  Group = -> [Li_element001,N_element022,H_element049]
  conduct = 2
  density = 1
  expand = 3
  formula = G4_LITHIUM_AMIDE
  name = G4_LITHIUM_AMIDE
  specific = 4
FEATURE [App::DocumentObjectGroupPython] Li_element002  label="Li_element : 2"  # scripted group (container) (typed FeaturePython)
  n = 2
  ref = Li_element
FEATURE [App::DocumentObjectGroupPython] C_element055  label="C_element : 030"  # scripted group (container) (typed FeaturePython)
  n = 1
  ref = C_element
FEATURE [App::DocumentObjectGroupPython] O_element054  label="O_element : 028"  # scripted group (container) (typed FeaturePython)
  n = 3
  ref = O_element
FEATURE [App::DocumentObjectGroupPython] G4_LITHIUM_CARBONATE  # scripted group (container) (typed FeaturePython)
  Dunit = g/cm3
  Dvalue = 2.11
  Group = -> [Li_element002,C_element055,O_element054]
  conduct = 2
  density = 1
  expand = 3
  formula = G4_LITHIUM_CARBONATE
  name = G4_LITHIUM_CARBONATE
  specific = 4
FEATURE [App::DocumentObjectGroupPython] Li_element003  label="Li_element : 003"  # scripted group (container) (typed FeaturePython)
  n = 1
  ref = Li_element
FEATURE [App::DocumentObjectGroupPython] F_element012  label="F_element : 004"  # scripted group (container) (typed FeaturePython)
  n = 1
  ref = F_element
FEATURE [App::DocumentObjectGroupPython] G4_LITHIUM_FLUORIDE  # scripted group (container) (typed FeaturePython)
  Dunit = g/cm3
  Dvalue = 2.635
  Group = -> [Li_element003,F_element012]
  conduct = 2
  density = 1
  expand = 3
  formula = G4_LITHIUM_FLUORIDE
  name = G4_LITHIUM_FLUORIDE
  specific = 4
FEATURE [App::DocumentObjectGroupPython] Li_element004  label="Li_element : 004"  # scripted group (container) (typed FeaturePython)
  n = 1
  ref = Li_element
FEATURE [App::DocumentObjectGroupPython] H_element050  label="H_element : 027"  # scripted group (container) (typed FeaturePython)
  n = 1
  ref = H_element
FEATURE [App::DocumentObjectGroupPython] G4_LITHIUM_HYDRIDE  # scripted group (container) (typed FeaturePython)
  Dunit = g/cm3
  Dvalue = 0.82
  Group = -> [Li_element004,H_element050]
  conduct = 2
  density = 1
  expand = 3
  formula = G4_LITHIUM_HYDRIDE
  name = G4_LITHIUM_HYDRIDE
  specific = 4
FEATURE [App::DocumentObjectGroupPython] Li_element005  label="Li_element : 005"  # scripted group (container) (typed FeaturePython)
  n = 1
  ref = Li_element
FEATURE [App::DocumentObjectGroupPython] I_element003  label="I_element : 002"  # scripted group (container) (typed FeaturePython)
  n = 1
  ref = I_element
FEATURE [App::DocumentObjectGroupPython] G4_LITHIUM_IODIDE  # scripted group (container) (typed FeaturePython)
  Dunit = g/cm3
  Dvalue = 3.494
  Group = -> [Li_element005,I_element003]
  conduct = 2
  density = 1
  expand = 3
  formula = G4_LITHIUM_IODIDE
  name = G4_LITHIUM_IODIDE
  specific = 4
FEATURE [App::DocumentObjectGroupPython] Li_element006  label="Li_element : 006"  # scripted group (container) (typed FeaturePython)
  n = 2
  ref = Li_element
FEATURE [App::DocumentObjectGroupPython] O_element055  label="O_element : 029"  # scripted group (container) (typed FeaturePython)
  n = 1
  ref = O_element
FEATURE [App::DocumentObjectGroupPython] G4_LITHIUM_OXIDE  # scripted group (container) (typed FeaturePython)
  Dunit = g/cm3
  Dvalue = 2.013
  Group = -> [Li_element006,O_element055]
  conduct = 2
  density = 1
  expand = 3
  formula = G4_LITHIUM_OXIDE
  name = G4_LITHIUM_OXIDE
  specific = 4
FEATURE [App::DocumentObjectGroupPython] Li_element007  label="Li_element : 007"  # scripted group (container) (typed FeaturePython)
  n = 2
  ref = Li_element
FEATURE [App::DocumentObjectGroupPython] B_element005  label="B_element : 005"  # scripted group (container) (typed FeaturePython)
  n = 4
  ref = B_element
FEATURE [App::DocumentObjectGroupPython] O_element056  label="O_element : 7"  # scripted group (container) (typed FeaturePython)
  n = 7
  ref = O_element
FEATURE [App::DocumentObjectGroupPython] G4_LITHIUM_TETRABORATE  # scripted group (container) (typed FeaturePython)
  Dunit = g/cm3
  Dvalue = 2.44
  Group = -> [Li_element007,B_element005,O_element056]
  conduct = 2
  density = 1
  expand = 3
  formula = G4_LITHIUM_TETRABORATE
  name = G4_LITHIUM_TETRABORATE
  specific = 4
FEATURE [App::DocumentObjectGroupPython] H_element051  label="H_element : 0.105"  # scripted group (container) (typed FeaturePython)
  n = 0.105
FEATURE [App::DocumentObjectGroupPython] C_element056  label="C_element : 0.083"  # scripted group (container) (typed FeaturePython)
  n = 0.083
FEATURE [App::DocumentObjectGroupPython] N_element023  label="N_element : 0.023"  # scripted group (container) (typed FeaturePython)
  n = 0.023
FEATURE [App::DocumentObjectGroupPython] O_element057  label="O_element : 0.779"  # scripted group (container) (typed FeaturePython)
  n = 0.779
FEATURE [App::DocumentObjectGroupPython] Na_element010  label="Na_element : 0.097"  # scripted group (container) (typed FeaturePython)
  n = 0.002
FEATURE [App::DocumentObjectGroupPython] P_element006  label="P_element : 0.105"  # scripted group (container) (typed FeaturePython)
  n = 0.001
FEATURE [App::DocumentObjectGroupPython] S_element016  label="S_element : 0.017"  # scripted group (container) (typed FeaturePython)
  n = 0.002
FEATURE [App::DocumentObjectGroupPython] Cl_element014  label="Cl_element : 0.587"  # scripted group (container) (typed FeaturePython)
  n = 0.003
FEATURE [App::DocumentObjectGroupPython] K_element005  label="K_element : 0.015"  # scripted group (container) (typed FeaturePython)
  n = 0.002
FEATURE [App::DocumentObjectGroupPython] G4_LUNG_ICRP  # scripted group (container) (typed FeaturePython)
  Dunit = g/cm3
  Dvalue = 1.04
  Group = -> [H_element051,C_element056,N_element023,O_element057,Na_element010,P_element006,S_element016,Cl_element014,K_element005]
  conduct = 2
  density = 1
  expand = 3
  formula = G4_LUNG_ICRP
  name = G4_LUNG_ICRP
  specific = 4
FEATURE [App::DocumentObjectGroupPython] H_element052  label="H_element : 0.116"  # scripted group (container) (typed FeaturePython)
  n = 0.114318
FEATURE [App::DocumentObjectGroupPython] C_element057  label="C_element : 0.656"  # scripted group (container) (typed FeaturePython)
  n = 0.655824
FEATURE [App::DocumentObjectGroupPython] O_element058  label="O_element : 0.092"  # scripted group (container) (typed FeaturePython)
  n = 0.0921831
FEATURE [App::DocumentObjectGroupPython] Mg_element004  label="Mg_element : 0.135"  # scripted group (container) (typed FeaturePython)
  n = 0.134792
FEATURE [App::DocumentObjectGroupPython] Ca_element013  label="Ca_element : 0.003"  # scripted group (container) (typed FeaturePython)
  n = 0.002883
FEATURE [App::DocumentObjectGroupPython] G4_M3_WAX  # scripted group (container) (typed FeaturePython)
  Dunit = g/cm3
  Dvalue = 1.05
  Group = -> [H_element052,C_element057,O_element058,Mg_element004,Ca_element013]
  conduct = 2
  density = 1
  expand = 3
  formula = G4_M3_WAX
  name = G4_M3_WAX
  specific = 4
FEATURE [App::DocumentObjectGroupPython] Mg_element005  label="Mg_element : 1"  # scripted group (container) (typed FeaturePython)
  n = 1
  ref = Mg_element
FEATURE [App::DocumentObjectGroupPython] C_element058  label="C_element : 031"  # scripted group (container) (typed FeaturePython)
  n = 1
  ref = C_element
FEATURE [App::DocumentObjectGroupPython] O_element059  label="O_element : 030"  # scripted group (container) (typed FeaturePython)
  n = 3
  ref = O_element
FEATURE [App::DocumentObjectGroupPython] G4_MAGNESIUM_CARBONATE  # scripted group (container) (typed FeaturePython)
  Dunit = g/cm3
  Dvalue = 2.958
  Group = -> [Mg_element005,C_element058,O_element059]
  conduct = 2
  density = 1
  expand = 3
  formula = G4_MAGNESIUM_CARBONATE
  name = G4_MAGNESIUM_CARBONATE
  specific = 4
FEATURE [App::DocumentObjectGroupPython] Mg_element006  label="Mg_element : 002"  # scripted group (container) (typed FeaturePython)
  n = 1
  ref = Mg_element
FEATURE [App::DocumentObjectGroupPython] F_element013  label="F_element : 005"  # scripted group (container) (typed FeaturePython)
  n = 2
  ref = F_element
FEATURE [App::DocumentObjectGroupPython] G4_MAGNESIUM_FLUORIDE  # scripted group (container) (typed FeaturePython)
  Dunit = g/cm3
  Dvalue = 3
  Group = -> [Mg_element006,F_element013]
  conduct = 2
  density = 1
  expand = 3
  formula = G4_MAGNESIUM_FLUORIDE
  name = G4_MAGNESIUM_FLUORIDE
  specific = 4
FEATURE [App::DocumentObjectGroupPython] Mg_element007  label="Mg_element : 003"  # scripted group (container) (typed FeaturePython)
  n = 1
  ref = Mg_element
FEATURE [App::DocumentObjectGroupPython] O_element060  label="O_element : 031"  # scripted group (container) (typed FeaturePython)
  n = 1
  ref = O_element
FEATURE [App::DocumentObjectGroupPython] G4_MAGNESIUM_OXIDE  # scripted group (container) (typed FeaturePython)
  Dunit = g/cm3
  Dvalue = 3.58
  Group = -> [Mg_element007,O_element060]
  conduct = 2
  density = 1
  expand = 3
  formula = G4_MAGNESIUM_OXIDE
  name = G4_MAGNESIUM_OXIDE
  specific = 4
FEATURE [App::DocumentObjectGroupPython] Mg_element008  label="Mg_element : 004"  # scripted group (container) (typed FeaturePython)
  n = 1
  ref = Mg_element
FEATURE [App::DocumentObjectGroupPython] B_element006  label="B_element : 006"  # scripted group (container) (typed FeaturePython)
  n = 4
  ref = B_element
FEATURE [App::DocumentObjectGroupPython] O_element061  label="O_element : 032"  # scripted group (container) (typed FeaturePython)
  n = 7
  ref = O_element
FEATURE [App::DocumentObjectGroupPython] G4_MAGNESIUM_TETRABORATE  # scripted group (container) (typed FeaturePython)
  Dunit = g/cm3
  Dvalue = 2.53
  Group = -> [Mg_element008,B_element006,O_element061]
  conduct = 2
  density = 1
  expand = 3
  formula = G4_MAGNESIUM_TETRABORATE
  name = G4_MAGNESIUM_TETRABORATE
  specific = 4
FEATURE [App::DocumentObjectGroupPython] Hg_element001  label="Hg_element : 1"  # scripted group (container) (typed FeaturePython)
  n = 1
  ref = Hg_element
FEATURE [App::DocumentObjectGroupPython] I_element004  label="I_element : 2"  # scripted group (container) (typed FeaturePython)
  n = 2
  ref = I_element
FEATURE [App::DocumentObjectGroupPython] G4_MERCURIC_IODIDE  # scripted group (container) (typed FeaturePython)
  Dunit = g/cm3
  Dvalue = 6.36
  Group = -> [Hg_element001,I_element004]
  conduct = 2
  density = 1
  expand = 3
  formula = G4_MERCURIC_IODIDE
  name = G4_MERCURIC_IODIDE
  specific = 4
FEATURE [App::DocumentObjectGroupPython] C_element059  label="C_element : 032"  # scripted group (container) (typed FeaturePython)
  n = 1
  ref = C_element
FEATURE [App::DocumentObjectGroupPython] H_element053  label="H_element : 028"  # scripted group (container) (typed FeaturePython)
  n = 4
  ref = H_element
FEATURE [App::DocumentObjectGroupPython] G4_METHANE  # scripted group (container) (typed FeaturePython)
  Dunit = g/cm3
  Dvalue = 0.000667151
  Group = -> [C_element059,H_element053]
  conduct = 2
  density = 1
  expand = 3
  formula = G4_METHANE
  name = G4_METHANE
  specific = 4
FEATURE [App::DocumentObjectGroupPython] C_element060  label="C_element : 033"  # scripted group (container) (typed FeaturePython)
  n = 1
  ref = C_element
FEATURE [App::DocumentObjectGroupPython] H_element054  label="H_element : 029"  # scripted group (container) (typed FeaturePython)
  n = 4
  ref = H_element
FEATURE [App::DocumentObjectGroupPython] O_element062  label="O_element : 033"  # scripted group (container) (typed FeaturePython)
  n = 1
  ref = O_element
FEATURE [App::DocumentObjectGroupPython] G4_METHANOL  # scripted group (container) (typed FeaturePython)
  Dunit = g/cm3
  Dvalue = 0.7914
  Group = -> [C_element060,H_element054,O_element062]
  conduct = 2
  density = 1
  expand = 3
  formula = G4_METHANOL
  name = G4_METHANOL
  specific = 4
FEATURE [App::DocumentObjectGroupPython] H_element055  label="H_element : 0.134"  # scripted group (container) (typed FeaturePython)
  n = 0.13404
FEATURE [App::DocumentObjectGroupPython] C_element061  label="C_element : 0.778"  # scripted group (container) (typed FeaturePython)
  n = 0.77796
FEATURE [App::DocumentObjectGroupPython] O_element063  label="O_element : 0.035"  # scripted group (container) (typed FeaturePython)
  n = 0.03502
FEATURE [App::DocumentObjectGroupPython] Mg_element009  label="Mg_element : 0.039"  # scripted group (container) (typed FeaturePython)
  n = 0.038594
FEATURE [App::DocumentObjectGroupPython] Ti_element002  label="Ti_element : 0.014"  # scripted group (container) (typed FeaturePython)
  n = 0.014386
FEATURE [App::DocumentObjectGroupPython] G4_MIX_D_WAX  # scripted group (container) (typed FeaturePython)
  Dunit = g/cm3
  Dvalue = 0.99
  Group = -> [H_element055,C_element061,O_element063,Mg_element009,Ti_element002]
  conduct = 2
  density = 1
  expand = 3
  formula = G4_MIX_D_WAX
  name = G4_MIX_D_WAX
  specific = 4
FEATURE [App::DocumentObjectGroupPython] H_element056  label="H_element : 0.135"  # scripted group (container) (typed FeaturePython)
  n = 0.081192
FEATURE [App::DocumentObjectGroupPython] C_element062  label="C_element : 0.583"  # scripted group (container) (typed FeaturePython)
  n = 0.583442
FEATURE [App::DocumentObjectGroupPython] N_element024  label="N_element : 0.018"  # scripted group (container) (typed FeaturePython)
  n = 0.017798
FEATURE [App::DocumentObjectGroupPython] O_element064  label="O_element : 0.186"  # scripted group (container) (typed FeaturePython)
  n = 0.186381
FEATURE [App::DocumentObjectGroupPython] Mg_element010  label="Mg_element : 0.130"  # scripted group (container) (typed FeaturePython)
  n = 0.130287
FEATURE [App::DocumentObjectGroupPython] Cl_element015  label="Cl_element : 0.588"  # scripted group (container) (typed FeaturePython)
  n = 0.0009
FEATURE [App::DocumentObjectGroupPython] G4_MS20_TISSUE  # scripted group (container) (typed FeaturePython)
  Dunit = g/cm3
  Dvalue = 1
  Group = -> [H_element056,C_element062,N_element024,O_element064,Mg_element010,Cl_element015]
  conduct = 2
  density = 1
  expand = 3
  formula = G4_MS20_TISSUE
  name = G4_MS20_TISSUE
  specific = 4
FEATURE [App::DocumentObjectGroupPython] H_element057  label="H_element : 0.136"  # scripted group (container) (typed FeaturePython)
  n = 0.102
FEATURE [App::DocumentObjectGroupPython] C_element063  label="C_element : 0.143"  # scripted group (container) (typed FeaturePython)
  n = 0.143
FEATURE [App::DocumentObjectGroupPython] N_element025  label="N_element : 0.034"  # scripted group (container) (typed FeaturePython)
  n = 0.034
FEATURE [App::DocumentObjectGroupPython] O_element065  label="O_element : 0.710"  # scripted group (container) (typed FeaturePython)
  n = 0.71
FEATURE [App::DocumentObjectGroupPython] Na_element011  label="Na_element : 0.098"  # scripted group (container) (typed FeaturePython)
  n = 0.001
FEATURE [App::DocumentObjectGroupPython] P_element007  label="P_element : 0.002"  # scripted group (container) (typed FeaturePython)
  n = 0.002
FEATURE [App::DocumentObjectGroupPython] S_element017  label="S_element : 0.018"  # scripted group (container) (typed FeaturePython)
  n = 0.003
FEATURE [App::DocumentObjectGroupPython] Cl_element016  label="Cl_element : 0.589"  # scripted group (container) (typed FeaturePython)
  n = 0.001
FEATURE [App::DocumentObjectGroupPython] K_element006  label="K_element : 0.004"  # scripted group (container) (typed FeaturePython)
  n = 0.004
FEATURE [App::DocumentObjectGroupPython] G4_MUSCLE_SKELETAL_ICRP  # scripted group (container) (typed FeaturePython)
  Dunit = g/cm3
  Dvalue = 1.05
  Group = -> [H_element057,C_element063,N_element025,O_element065,Na_element011,P_element007,S_element017,Cl_element016,K_element006]
  conduct = 2
  density = 1
  expand = 3
  formula = G4_MUSCLE_SKELETAL_ICRP
  name = G4_MUSCLE_SKELETAL_ICRP
  specific = 4
FEATURE [App::DocumentObjectGroupPython] H_element058  label="H_element : 0.137"  # scripted group (container) (typed FeaturePython)
  n = 0.102102
FEATURE [App::DocumentObjectGroupPython] C_element064  label="C_element : 0.123"  # scripted group (container) (typed FeaturePython)
  n = 0.123123
FEATURE [App::DocumentObjectGroupPython] N_element026  label="N_element : 0.756"  # scripted group (container) (typed FeaturePython)
  n = 0.035035
FEATURE [App::DocumentObjectGroupPython] O_element066  label="O_element : 0.730"  # scripted group (container) (typed FeaturePython)
  n = 0.72973
FEATURE [App::DocumentObjectGroupPython] Na_element012  label="Na_element : 0.099"  # scripted group (container) (typed FeaturePython)
  n = 0.001001
FEATURE [App::DocumentObjectGroupPython] P_element008  label="P_element : 0.106"  # scripted group (container) (typed FeaturePython)
  n = 0.002002
FEATURE [App::DocumentObjectGroupPython] S_element018  label="S_element : 0.019"  # scripted group (container) (typed FeaturePython)
  n = 0.004004
FEATURE [App::DocumentObjectGroupPython] K_element007  label="K_element : 0.016"  # scripted group (container) (typed FeaturePython)
  n = 0.003003
FEATURE [App::DocumentObjectGroupPython] G4_MUSCLE_STRIATED_ICRU  # scripted group (container) (typed FeaturePython)
  Dunit = g/cm3
  Dvalue = 1.04
  Group = -> [H_element058,C_element064,N_element026,O_element066,Na_element012,P_element008,S_element018,K_element007]
  conduct = 2
  density = 1
  expand = 3
  formula = G4_MUSCLE_STRIATED_ICRU
  name = G4_MUSCLE_STRIATED_ICRU
  specific = 4
FEATURE [App::DocumentObjectGroupPython] H_element059  label="H_element : 0.098"  # scripted group (container) (typed FeaturePython)
  n = 0.0982341
FEATURE [App::DocumentObjectGroupPython] C_element065  label="C_element : 0.156"  # scripted group (container) (typed FeaturePython)
  n = 0.156214
FEATURE [App::DocumentObjectGroupPython] N_element027  label="N_element : 0.757"  # scripted group (container) (typed FeaturePython)
  n = 0.035451
FEATURE [App::DocumentObjectGroupPython] O_element067  label="O_element : 0.880"  # scripted group (container) (typed FeaturePython)
  n = 0.710101
FEATURE [App::DocumentObjectGroupPython] G4_MUSCLE_WITH_SUCROSE  # scripted group (container) (typed FeaturePython)
  Dunit = g/cm3
  Dvalue = 1.11
  Group = -> [H_element059,C_element065,N_element027,O_element067]
  conduct = 2
  density = 1
  expand = 3
  formula = G4_MUSCLE_WITH_SUCROSE
  name = G4_MUSCLE_WITH_SUCROSE
  specific = 4
FEATURE [App::DocumentObjectGroupPython] H_element060  label="H_element : 0.138"  # scripted group (container) (typed FeaturePython)
  n = 0.101969
FEATURE [App::DocumentObjectGroupPython] C_element066  label="C_element : 0.120"  # scripted group (container) (typed FeaturePython)
  n = 0.120058
FEATURE [App::DocumentObjectGroupPython] N_element028  label="N_element : 0.758"  # scripted group (container) (typed FeaturePython)
  n = 0.035451
FEATURE [App::DocumentObjectGroupPython] O_element068  label="O_element : 0.743"  # scripted group (container) (typed FeaturePython)
  n = 0.742522
FEATURE [App::DocumentObjectGroupPython] G4_MUSCLE_WITHOUT_SUCROSE  # scripted group (container) (typed FeaturePython)
  Dunit = g/cm3
  Dvalue = 1.07
  Group = -> [H_element060,C_element066,N_element028,O_element068]
  conduct = 2
  density = 1
  expand = 3
  formula = G4_MUSCLE_WITHOUT_SUCROSE
  name = G4_MUSCLE_WITHOUT_SUCROSE
  specific = 4
FEATURE [App::DocumentObjectGroupPython] C_element067  label="C_element : 10"  # scripted group (container) (typed FeaturePython)
  n = 10
  ref = C_element
FEATURE [App::DocumentObjectGroupPython] H_element061  label="H_element : 030"  # scripted group (container) (typed FeaturePython)
  n = 8
  ref = H_element
FEATURE [App::DocumentObjectGroupPython] G4_NAPHTHALENE  # scripted group (container) (typed FeaturePython)
  Dunit = g/cm3
  Dvalue = 1.145
  Group = -> [C_element067,H_element061]
  conduct = 2
  density = 1
  expand = 3
  formula = G4_NAPHTHALENE
  name = G4_NAPHTHALENE
  specific = 4
FEATURE [App::DocumentObjectGroupPython] C_element068  label="C_element : 034"  # scripted group (container) (typed FeaturePython)
  n = 6
  ref = C_element
FEATURE [App::DocumentObjectGroupPython] H_element062  label="H_element : 031"  # scripted group (container) (typed FeaturePython)
  n = 5
  ref = H_element
FEATURE [App::DocumentObjectGroupPython] N_element029  label="N_element : 012"  # scripted group (container) (typed FeaturePython)
  n = 1
  ref = N_element
FEATURE [App::DocumentObjectGroupPython] O_element069  label="O_element : 034"  # scripted group (container) (typed FeaturePython)
  n = 2
  ref = O_element
FEATURE [App::DocumentObjectGroupPython] G4_NITROBENZENE  # scripted group (container) (typed FeaturePython)
  Dunit = g/cm3
  Dvalue = 1.19867
  Group = -> [C_element068,H_element062,N_element029,O_element069]
  conduct = 2
  density = 1
  expand = 3
  formula = G4_NITROBENZENE
  name = G4_NITROBENZENE
  specific = 4
FEATURE [App::DocumentObjectGroupPython] N_element030  label="N_element : 013"  # scripted group (container) (typed FeaturePython)
  n = 2
  ref = N_element
FEATURE [App::DocumentObjectGroupPython] O_element070  label="O_element : 035"  # scripted group (container) (typed FeaturePython)
  n = 1
  ref = O_element
FEATURE [App::DocumentObjectGroupPython] G4_NITROUS_OXIDE  # scripted group (container) (typed FeaturePython)
  Dunit = g/cm3
  Dvalue = 0.00183094
  Group = -> [N_element030,O_element070]
  conduct = 2
  density = 1
  expand = 3
  formula = G4_NITROUS_OXIDE
  name = G4_NITROUS_OXIDE
  specific = 4
FEATURE [App::DocumentObjectGroupPython] H_element063  label="H_element : 0.104"  # scripted group (container) (typed FeaturePython)
  n = 0.103509
FEATURE [App::DocumentObjectGroupPython] C_element069  label="C_element : 0.648"  # scripted group (container) (typed FeaturePython)
  n = 0.648416
FEATURE [App::DocumentObjectGroupPython] N_element031  label="N_element : 0.100"  # scripted group (container) (typed FeaturePython)
  n = 0.0995361
FEATURE [App::DocumentObjectGroupPython] O_element071  label="O_element : 0.149"  # scripted group (container) (typed FeaturePython)
  n = 0.148539
FEATURE [App::DocumentObjectGroupPython] G4_NYLON_8062  label="G4_NYLON-8062"  # scripted group (container) (typed FeaturePython)
  Dunit = g/cm3
  Dvalue = 1.08
  Group = -> [H_element063,C_element069,N_element031,O_element071]
  conduct = 2
  density = 1
  expand = 3
  formula = G4_NYLON-8062
  name = G4_NYLON-8062
  specific = 4
FEATURE [App::DocumentObjectGroupPython] C_element070  label="C_element : 035"  # scripted group (container) (typed FeaturePython)
  n = 6
  ref = C_element
FEATURE [App::DocumentObjectGroupPython] H_element064  label="H_element : 11"  # scripted group (container) (typed FeaturePython)
  n = 11
  ref = H_element
FEATURE [App::DocumentObjectGroupPython] N_element032  label="N_element : 014"  # scripted group (container) (typed FeaturePython)
  n = 1
  ref = N_element
FEATURE [App::DocumentObjectGroupPython] O_element072  label="O_element : 036"  # scripted group (container) (typed FeaturePython)
  n = 1
  ref = O_element
FEATURE [App::DocumentObjectGroupPython] G4_NYLON_6_6  label="G4_NYLON-6-6"  # scripted group (container) (typed FeaturePython)
  Dunit = g/cm3
  Dvalue = 1.14
  Group = -> [C_element070,H_element064,N_element032,O_element072]
  conduct = 2
  density = 1
  expand = 3
  formula = G4_NYLON-6-6
  name = G4_NYLON-6-6
  specific = 4
FEATURE [App::DocumentObjectGroupPython] H_element065  label="H_element : 0.139"  # scripted group (container) (typed FeaturePython)
  n = 0.107062
FEATURE [App::DocumentObjectGroupPython] C_element071  label="C_element : 0.680"  # scripted group (container) (typed FeaturePython)
  n = 0.680449
FEATURE [App::DocumentObjectGroupPython] N_element033  label="N_element : 0.099"  # scripted group (container) (typed FeaturePython)
  n = 0.099189
FEATURE [App::DocumentObjectGroupPython] O_element073  label="O_element : 0.113"  # scripted group (container) (typed FeaturePython)
  n = 0.1133
FEATURE [App::DocumentObjectGroupPython] G4_NYLON_6_10  label="G4_NYLON-6-10"  # scripted group (container) (typed FeaturePython)
  Dunit = g/cm3
  Dvalue = 1.14
  Group = -> [H_element065,C_element071,N_element033,O_element073]
  conduct = 2
  density = 1
  expand = 3
  formula = G4_NYLON-6-10
  name = G4_NYLON-6-10
  specific = 4
FEATURE [App::DocumentObjectGroupPython] H_element066  label="H_element : 0.140"  # scripted group (container) (typed FeaturePython)
  n = 0.115476
FEATURE [App::DocumentObjectGroupPython] C_element072  label="C_element : 0.721"  # scripted group (container) (typed FeaturePython)
  n = 0.720818
FEATURE [App::DocumentObjectGroupPython] N_element034  label="N_element : 0.076"  # scripted group (container) (typed FeaturePython)
  n = 0.0764169
FEATURE [App::DocumentObjectGroupPython] O_element074  label="O_element : 0.087"  # scripted group (container) (typed FeaturePython)
  n = 0.0872889
FEATURE [App::DocumentObjectGroupPython] G4_NYLON_11_RILSAN  label="G4_NYLON-11_RILSAN"  # scripted group (container) (typed FeaturePython)
  Dunit = g/cm3
  Dvalue = 1.425
  Group = -> [H_element066,C_element072,N_element034,O_element074]
  conduct = 2
  density = 1
  expand = 3
  formula = G4_NYLON-11_RILSAN
  name = G4_NYLON-11_RILSAN
  specific = 4
FEATURE [App::DocumentObjectGroupPython] C_element073  label="C_element : 8"  # scripted group (container) (typed FeaturePython)
  n = 8
  ref = C_element
FEATURE [App::DocumentObjectGroupPython] H_element067  label="H_element : 18"  # scripted group (container) (typed FeaturePython)
  n = 18
  ref = H_element
FEATURE [App::DocumentObjectGroupPython] G4_OCTANE  # scripted group (container) (typed FeaturePython)
  Dunit = g/cm3
  Dvalue = 0.7026
  Group = -> [C_element073,H_element067]
  conduct = 2
  density = 1
  expand = 3
  formula = G4_OCTANE
  name = G4_OCTANE
  specific = 4
FEATURE [App::DocumentObjectGroupPython] C_element074  label="C_element : 25"  # scripted group (container) (typed FeaturePython)
  n = 25
  ref = C_element
FEATURE [App::DocumentObjectGroupPython] H_element068  label="H_element : 52"  # scripted group (container) (typed FeaturePython)
  n = 52
  ref = H_element
FEATURE [App::DocumentObjectGroupPython] G4_PARAFFIN  # scripted group (container) (typed FeaturePython)
  Dunit = g/cm3
  Dvalue = 0.93
  Group = -> [C_element074,H_element068]
  conduct = 2
  density = 1
  expand = 3
  formula = G4_PARAFFIN
  name = G4_PARAFFIN
  specific = 4
FEATURE [App::DocumentObjectGroupPython] C_element075  label="C_element : 036"  # scripted group (container) (typed FeaturePython)
  n = 5
  ref = C_element
FEATURE [App::DocumentObjectGroupPython] H_element069  label="H_element : 032"  # scripted group (container) (typed FeaturePython)
  n = 12
  ref = H_element
FEATURE [App::DocumentObjectGroupPython] G4_N_PENTANE  label="G4_N-PENTANE"  # scripted group (container) (typed FeaturePython)
  Dunit = g/cm3
  Dvalue = 0.6262
  Group = -> [C_element075,H_element069]
  conduct = 2
  density = 1
  expand = 3
  formula = G4_N-PENTANE
  name = G4_N-PENTANE
  specific = 4
FEATURE [App::DocumentObjectGroupPython] H_element070  label="H_element : 0.014"  # scripted group (container) (typed FeaturePython)
  n = 0.0141
FEATURE [App::DocumentObjectGroupPython] C_element076  label="C_element : 0.072"  # scripted group (container) (typed FeaturePython)
  n = 0.072261
FEATURE [App::DocumentObjectGroupPython] N_element035  label="N_element : 0.019"  # scripted group (container) (typed FeaturePython)
  n = 0.01932
FEATURE [App::DocumentObjectGroupPython] O_element075  label="O_element : 0.066"  # scripted group (container) (typed FeaturePython)
  n = 0.066101
FEATURE [App::DocumentObjectGroupPython] S_element019  label="S_element : 0.020"  # scripted group (container) (typed FeaturePython)
  n = 0.00189
FEATURE [App::DocumentObjectGroupPython] Br_element004  label="Br_element : 0.349"  # scripted group (container) (typed FeaturePython)
  n = 0.349103
FEATURE [App::DocumentObjectGroupPython] Ag_element001  label="Ag_element : 0.474"  # scripted group (container) (typed FeaturePython)
  n = 0.474105
FEATURE [App::DocumentObjectGroupPython] I_element005  label="I_element : 0.003"  # scripted group (container) (typed FeaturePython)
  n = 0.00312
FEATURE [App::DocumentObjectGroupPython] G4_PHOTO_EMULSION  # scripted group (container) (typed FeaturePython)
  Dunit = g/cm3
  Dvalue = 3.815
  Group = -> [H_element070,C_element076,N_element035,O_element075,S_element019,Br_element004,Ag_element001,I_element005]
  conduct = 2
  density = 1
  expand = 3
  formula = G4_PHOTO_EMULSION
  name = G4_PHOTO_EMULSION
  specific = 4
FEATURE [App::DocumentObjectGroupPython] C_element077  label="C_element : 9"  # scripted group (container) (typed FeaturePython)
  n = 9
  ref = C_element
FEATURE [App::DocumentObjectGroupPython] H_element071  label="H_element : 033"  # scripted group (container) (typed FeaturePython)
  n = 10
  ref = H_element
FEATURE [App::DocumentObjectGroupPython] G4_PLASTIC_SC_VINYLTOLUENE  # scripted group (container) (typed FeaturePython)
  Dunit = g/cm3
  Dvalue = 1.032
  Group = -> [C_element077,H_element071]
  conduct = 2
  density = 1
  expand = 3
  formula = G4_PLASTIC_SC_VINYLTOLUENE
  name = G4_PLASTIC_SC_VINYLTOLUENE
  specific = 4
FEATURE [App::DocumentObjectGroupPython] Pu_element001  label="Pu_element : 1"  # scripted group (container) (typed FeaturePython)
  n = 1
  ref = Pu_element
FEATURE [App::DocumentObjectGroupPython] O_element076  label="O_element : 037"  # scripted group (container) (typed FeaturePython)
  n = 2
  ref = O_element
FEATURE [App::DocumentObjectGroupPython] G4_PLUTONIUM_DIOXIDE  # scripted group (container) (typed FeaturePython)
  Dunit = g/cm3
  Dvalue = 11.46
  Group = -> [Pu_element001,O_element076]
  conduct = 2
  density = 1
  expand = 3
  formula = G4_PLUTONIUM_DIOXIDE
  name = G4_PLUTONIUM_DIOXIDE
  specific = 4
FEATURE [App::DocumentObjectGroupPython] C_element078  label="C_element : 037"  # scripted group (container) (typed FeaturePython)
  n = 3
  ref = C_element
FEATURE [App::DocumentObjectGroupPython] H_element072  label="H_element : 034"  # scripted group (container) (typed FeaturePython)
  n = 3
  ref = H_element
FEATURE [App::DocumentObjectGroupPython] N_element036  label="N_element : 015"  # scripted group (container) (typed FeaturePython)
  n = 1
  ref = N_element
FEATURE [App::DocumentObjectGroupPython] G4_POLYACRYLONITRILE  # scripted group (container) (typed FeaturePython)
  Dunit = g/cm3
  Dvalue = 1.17
  Group = -> [C_element078,H_element072,N_element036]
  conduct = 2
  density = 1
  expand = 3
  formula = G4_POLYACRYLONITRILE
  name = G4_POLYACRYLONITRILE
  specific = 4
FEATURE [App::DocumentObjectGroupPython] C_element079  label="C_element : 16"  # scripted group (container) (typed FeaturePython)
  n = 16
  ref = C_element
FEATURE [App::DocumentObjectGroupPython] H_element073  label="H_element : 035"  # scripted group (container) (typed FeaturePython)
  n = 14
  ref = H_element
FEATURE [App::DocumentObjectGroupPython] O_element077  label="O_element : 038"  # scripted group (container) (typed FeaturePython)
  n = 3
  ref = O_element
FEATURE [App::DocumentObjectGroupPython] G4_POLYCARBONATE  # scripted group (container) (typed FeaturePython)
  Dunit = g/cm3
  Dvalue = 1.2
  Group = -> [C_element079,H_element073,O_element077]
  conduct = 2
  density = 1
  expand = 3
  formula = G4_POLYCARBONATE
  name = G4_POLYCARBONATE
  specific = 4
FEATURE [App::DocumentObjectGroupPython] C_element080  label="C_element : 038"  # scripted group (container) (typed FeaturePython)
  n = 8
  ref = C_element
FEATURE [App::DocumentObjectGroupPython] H_element074  label="H_element : 036"  # scripted group (container) (typed FeaturePython)
  n = 7
  ref = H_element
FEATURE [App::DocumentObjectGroupPython] Cl_element017  label="Cl_element : 007"  # scripted group (container) (typed FeaturePython)
  n = 1
  ref = Cl_element
FEATURE [App::DocumentObjectGroupPython] G4_POLYCHLOROSTYRENE  # scripted group (container) (typed FeaturePython)
  Dunit = g/cm3
  Dvalue = 1.3
  Group = -> [C_element080,H_element074,Cl_element017]
  conduct = 2
  density = 1
  expand = 3
  formula = G4_POLYCHLOROSTYRENE
  name = G4_POLYCHLOROSTYRENE
  specific = 4
FEATURE [App::DocumentObjectGroupPython] C_element081  label="C_element : 039"  # scripted group (container) (typed FeaturePython)
  n = 1
  ref = C_element
FEATURE [App::DocumentObjectGroupPython] H_element075  label="H_element : 037"  # scripted group (container) (typed FeaturePython)
  n = 2
  ref = H_element
FEATURE [App::DocumentObjectGroupPython] G4_POLYETHYLENE  # scripted group (container) (typed FeaturePython)
  Dunit = g/cm3
  Dvalue = 0.94
  Group = -> [C_element081,H_element075]
  conduct = 2
  density = 1
  expand = 3
  formula = G4_POLYETHYLENE
  name = G4_POLYETHYLENE
  specific = 4
FEATURE [App::DocumentObjectGroupPython] C_element082  label="C_element : 040"  # scripted group (container) (typed FeaturePython)
  n = 10
  ref = C_element
FEATURE [App::DocumentObjectGroupPython] H_element076  label="H_element : 038"  # scripted group (container) (typed FeaturePython)
  n = 8
  ref = H_element
FEATURE [App::DocumentObjectGroupPython] O_element078  label="O_element : 039"  # scripted group (container) (typed FeaturePython)
  n = 4
  ref = O_element
FEATURE [App::DocumentObjectGroupPython] G4_MYLAR  # scripted group (container) (typed FeaturePython)
  Dunit = g/cm3
  Dvalue = 1.4
  Group = -> [C_element082,H_element076,O_element078]
  conduct = 2
  density = 1
  expand = 3
  formula = G4_MYLAR
  name = G4_MYLAR
  specific = 4
FEATURE [App::DocumentObjectGroupPython] C_element083  label="C_element : 041"  # scripted group (container) (typed FeaturePython)
  n = 5
  ref = C_element
FEATURE [App::DocumentObjectGroupPython] H_element077  label="H_element : 039"  # scripted group (container) (typed FeaturePython)
  n = 8
  ref = H_element
FEATURE [App::DocumentObjectGroupPython] O_element079  label="O_element : 040"  # scripted group (container) (typed FeaturePython)
  n = 2
  ref = O_element
FEATURE [App::DocumentObjectGroupPython] G4_PLEXIGLASS  # scripted group (container) (typed FeaturePython)
  Dunit = g/cm3
  Dvalue = 1.19
  Group = -> [C_element083,H_element077,O_element079]
  conduct = 2
  density = 1
  expand = 3
  formula = G4_PLEXIGLASS
  name = G4_PLEXIGLASS
  specific = 4
FEATURE [App::DocumentObjectGroupPython] C_element084  label="C_element : 042"  # scripted group (container) (typed FeaturePython)
  n = 1
  ref = C_element
FEATURE [App::DocumentObjectGroupPython] H_element078  label="H_element : 040"  # scripted group (container) (typed FeaturePython)
  n = 2
  ref = H_element
FEATURE [App::DocumentObjectGroupPython] O_element080  label="O_element : 041"  # scripted group (container) (typed FeaturePython)
  n = 1
  ref = O_element
FEATURE [App::DocumentObjectGroupPython] G4_POLYOXYMETHYLENE  # scripted group (container) (typed FeaturePython)
  Dunit = g/cm3
  Dvalue = 1.425
  Group = -> [C_element084,H_element078,O_element080]
  conduct = 2
  density = 1
  expand = 3
  formula = G4_POLYOXYMETHYLENE
  name = G4_POLYOXYMETHYLENE
  specific = 4
FEATURE [App::DocumentObjectGroupPython] C_element085  label="C_element : 043"  # scripted group (container) (typed FeaturePython)
  n = 2
  ref = C_element
FEATURE [App::DocumentObjectGroupPython] H_element079  label="H_element : 041"  # scripted group (container) (typed FeaturePython)
  n = 4
  ref = H_element
FEATURE [App::DocumentObjectGroupPython] G4_POLYPROPYLENE  # scripted group (container) (typed FeaturePython)
  Dunit = g/cm3
  Dvalue = 0.9
  Group = -> [C_element085,H_element079]
  conduct = 2
  density = 1
  expand = 3
  formula = G4_POLYPROPYLENE
  name = G4_POLYPROPYLENE
  specific = 4
FEATURE [App::DocumentObjectGroupPython] C_element086  label="C_element : 044"  # scripted group (container) (typed FeaturePython)
  n = 8
  ref = C_element
FEATURE [App::DocumentObjectGroupPython] H_element080  label="H_element : 042"  # scripted group (container) (typed FeaturePython)
  n = 8
  ref = H_element
FEATURE [App::DocumentObjectGroupPython] G4_POLYSTYRENE  # scripted group (container) (typed FeaturePython)
  Dunit = g/cm3
  Dvalue = 1.06
  Group = -> [C_element086,H_element080]
  conduct = 2
  density = 1
  expand = 3
  formula = G4_POLYSTYRENE
  name = G4_POLYSTYRENE
  specific = 4
FEATURE [App::DocumentObjectGroupPython] C_element087  label="C_element : 045"  # scripted group (container) (typed FeaturePython)
  n = 2
  ref = C_element
FEATURE [App::DocumentObjectGroupPython] F_element014  label="F_element : 4"  # scripted group (container) (typed FeaturePython)
  n = 4
  ref = F_element
FEATURE [App::DocumentObjectGroupPython] G4_TEFLON  # scripted group (container) (typed FeaturePython)
  Dunit = g/cm3
  Dvalue = 2.2
  Group = -> [C_element087,F_element014]
  conduct = 2
  density = 1
  expand = 3
  formula = G4_TEFLON
  name = G4_TEFLON
  specific = 4
FEATURE [App::DocumentObjectGroupPython] C_element088  label="C_element : 046"  # scripted group (container) (typed FeaturePython)
  n = 2
  ref = C_element
FEATURE [App::DocumentObjectGroupPython] F_element015  label="F_element : 006"  # scripted group (container) (typed FeaturePython)
  n = 3
  ref = F_element
FEATURE [App::DocumentObjectGroupPython] Cl_element018  label="Cl_element : 008"  # scripted group (container) (typed FeaturePython)
  n = 1
  ref = Cl_element
FEATURE [App::DocumentObjectGroupPython] G4_POLYTRIFLUOROCHLOROETHYLENE  # scripted group (container) (typed FeaturePython)
  Dunit = g/cm3
  Dvalue = 2.1
  Group = -> [C_element088,F_element015,Cl_element018]
  conduct = 2
  density = 1
  expand = 3
  formula = G4_POLYTRIFLUOROCHLOROETHYLENE
  name = G4_POLYTRIFLUOROCHLOROETHYLENE
  specific = 4
FEATURE [App::DocumentObjectGroupPython] C_element089  label="C_element : 047"  # scripted group (container) (typed FeaturePython)
  n = 4
  ref = C_element
FEATURE [App::DocumentObjectGroupPython] H_element081  label="H_element : 043"  # scripted group (container) (typed FeaturePython)
  n = 6
  ref = H_element
FEATURE [App::DocumentObjectGroupPython] O_element081  label="O_element : 042"  # scripted group (container) (typed FeaturePython)
  n = 2
  ref = O_element
FEATURE [App::DocumentObjectGroupPython] G4_POLYVINYL_ACETATE  # scripted group (container) (typed FeaturePython)
  Dunit = g/cm3
  Dvalue = 1.19
  Group = -> [C_element089,H_element081,O_element081]
  conduct = 2
  density = 1
  expand = 3
  formula = G4_POLYVINYL_ACETATE
  name = G4_POLYVINYL_ACETATE
  specific = 4
FEATURE [App::DocumentObjectGroupPython] C_element090  label="C_element : 048"  # scripted group (container) (typed FeaturePython)
  n = 2
  ref = C_element
FEATURE [App::DocumentObjectGroupPython] H_element082  label="H_element : 044"  # scripted group (container) (typed FeaturePython)
  n = 4
  ref = H_element
FEATURE [App::DocumentObjectGroupPython] O_element082  label="O_element : 043"  # scripted group (container) (typed FeaturePython)
  n = 1
  ref = O_element
FEATURE [App::DocumentObjectGroupPython] G4_POLYVINYL_ALCOHOL  # scripted group (container) (typed FeaturePython)
  Dunit = g/cm3
  Dvalue = 1.3
  Group = -> [C_element090,H_element082,O_element082]
  conduct = 2
  density = 1
  expand = 3
  formula = G4_POLYVINYL_ALCOHOL
  name = G4_POLYVINYL_ALCOHOL
  specific = 4
FEATURE [App::DocumentObjectGroupPython] C_element091  label="C_element : 049"  # scripted group (container) (typed FeaturePython)
  n = 8
  ref = C_element
FEATURE [App::DocumentObjectGroupPython] H_element083  label="H_element : 045"  # scripted group (container) (typed FeaturePython)
  n = 14
  ref = H_element
FEATURE [App::DocumentObjectGroupPython] O_element083  label="O_element : 044"  # scripted group (container) (typed FeaturePython)
  n = 2
  ref = O_element
FEATURE [App::DocumentObjectGroupPython] G4_POLYVINYL_BUTYRAL  # scripted group (container) (typed FeaturePython)
  Dunit = g/cm3
  Dvalue = 1.12
  Group = -> [C_element091,H_element083,O_element083]
  conduct = 2
  density = 1
  expand = 3
  formula = G4_POLYVINYL_BUTYRAL
  name = G4_POLYVINYL_BUTYRAL
  specific = 4
FEATURE [App::DocumentObjectGroupPython] C_element092  label="C_element : 050"  # scripted group (container) (typed FeaturePython)
  n = 2
  ref = C_element
FEATURE [App::DocumentObjectGroupPython] H_element084  label="H_element : 046"  # scripted group (container) (typed FeaturePython)
  n = 3
  ref = H_element
FEATURE [App::DocumentObjectGroupPython] Cl_element019  label="Cl_element : 009"  # scripted group (container) (typed FeaturePython)
  n = 1
  ref = Cl_element
FEATURE [App::DocumentObjectGroupPython] G4_POLYVINYL_CHLORIDE  # scripted group (container) (typed FeaturePython)
  Dunit = g/cm3
  Dvalue = 1.3
  Group = -> [C_element092,H_element084,Cl_element019]
  conduct = 2
  density = 1
  expand = 3
  formula = G4_POLYVINYL_CHLORIDE
  name = G4_POLYVINYL_CHLORIDE
  specific = 4
FEATURE [App::DocumentObjectGroupPython] C_element093  label="C_element : 051"  # scripted group (container) (typed FeaturePython)
  n = 2
  ref = C_element
FEATURE [App::DocumentObjectGroupPython] H_element085  label="H_element : 047"  # scripted group (container) (typed FeaturePython)
  n = 2
  ref = H_element
FEATURE [App::DocumentObjectGroupPython] Cl_element020  label="Cl_element : 010"  # scripted group (container) (typed FeaturePython)
  n = 2
  ref = Cl_element
FEATURE [App::DocumentObjectGroupPython] G4_POLYVINYLIDENE_CHLORIDE  # scripted group (container) (typed FeaturePython)
  Dunit = g/cm3
  Dvalue = 1.7
  Group = -> [C_element093,H_element085,Cl_element020]
  conduct = 2
  density = 1
  expand = 3
  formula = G4_POLYVINYLIDENE_CHLORIDE
  name = G4_POLYVINYLIDENE_CHLORIDE
  specific = 4
FEATURE [App::DocumentObjectGroupPython] C_element094  label="C_element : 052"  # scripted group (container) (typed FeaturePython)
  n = 2
  ref = C_element
FEATURE [App::DocumentObjectGroupPython] H_element086  label="H_element : 048"  # scripted group (container) (typed FeaturePython)
  n = 2
  ref = H_element
FEATURE [App::DocumentObjectGroupPython] F_element016  label="F_element : 007"  # scripted group (container) (typed FeaturePython)
  n = 2
  ref = F_element
FEATURE [App::DocumentObjectGroupPython] G4_POLYVINYLIDENE_FLUORIDE  # scripted group (container) (typed FeaturePython)
  Dunit = g/cm3
  Dvalue = 1.76
  Group = -> [C_element094,H_element086,F_element016]
  conduct = 2
  density = 1
  expand = 3
  formula = G4_POLYVINYLIDENE_FLUORIDE
  name = G4_POLYVINYLIDENE_FLUORIDE
  specific = 4
FEATURE [App::DocumentObjectGroupPython] C_element095  label="C_element : 053"  # scripted group (container) (typed FeaturePython)
  n = 6
  ref = C_element
FEATURE [App::DocumentObjectGroupPython] H_element087  label="H_element : 9"  # scripted group (container) (typed FeaturePython)
  n = 9
  ref = H_element
FEATURE [App::DocumentObjectGroupPython] N_element037  label="N_element : 016"  # scripted group (container) (typed FeaturePython)
  n = 1
  ref = N_element
FEATURE [App::DocumentObjectGroupPython] O_element084  label="O_element : 045"  # scripted group (container) (typed FeaturePython)
  n = 1
  ref = O_element
FEATURE [App::DocumentObjectGroupPython] G4_POLYVINYL_PYRROLIDONE  # scripted group (container) (typed FeaturePython)
  Dunit = g/cm3
  Dvalue = 1.25
  Group = -> [C_element095,H_element087,N_element037,O_element084]
  conduct = 2
  density = 1
  expand = 3
  formula = G4_POLYVINYL_PYRROLIDONE
  name = G4_POLYVINYL_PYRROLIDONE
  specific = 4
FEATURE [App::DocumentObjectGroupPython] K_element008  label="K_element : 1"  # scripted group (container) (typed FeaturePython)
  n = 1
  ref = K_element
FEATURE [App::DocumentObjectGroupPython] I_element006  label="I_element : 003"  # scripted group (container) (typed FeaturePython)
  n = 1
  ref = I_element
FEATURE [App::DocumentObjectGroupPython] G4_POTASSIUM_IODIDE  # scripted group (container) (typed FeaturePython)
  Dunit = g/cm3
  Dvalue = 3.13
  Group = -> [K_element008,I_element006]
  conduct = 2
  density = 1
  expand = 3
  formula = G4_POTASSIUM_IODIDE
  name = G4_POTASSIUM_IODIDE
  specific = 4
FEATURE [App::DocumentObjectGroupPython] K_element009  label="K_element : 2"  # scripted group (container) (typed FeaturePython)
  n = 2
  ref = K_element
FEATURE [App::DocumentObjectGroupPython] O_element085  label="O_element : 046"  # scripted group (container) (typed FeaturePython)
  n = 1
  ref = O_element
FEATURE [App::DocumentObjectGroupPython] G4_POTASSIUM_OXIDE  # scripted group (container) (typed FeaturePython)
  Dunit = g/cm3
  Dvalue = 2.32
  Group = -> [K_element009,O_element085]
  conduct = 2
  density = 1
  expand = 3
  formula = G4_POTASSIUM_OXIDE
  name = G4_POTASSIUM_OXIDE
  specific = 4
FEATURE [App::DocumentObjectGroupPython] C_element096  label="C_element : 054"  # scripted group (container) (typed FeaturePython)
  n = 3
  ref = C_element
FEATURE [App::DocumentObjectGroupPython] H_element088  label="H_element : 049"  # scripted group (container) (typed FeaturePython)
  n = 8
  ref = H_element
FEATURE [App::DocumentObjectGroupPython] G4_PROPANE  # scripted group (container) (typed FeaturePython)
  Dunit = g/cm3
  Dvalue = 0.00187939
  Group = -> [C_element096,H_element088]
  conduct = 2
  density = 1
  expand = 3
  formula = G4_PROPANE
  name = G4_PROPANE
  specific = 4
FEATURE [App::DocumentObjectGroupPython] C_element097  label="C_element : 055"  # scripted group (container) (typed FeaturePython)
  n = 3
  ref = C_element
FEATURE [App::DocumentObjectGroupPython] H_element089  label="H_element : 050"  # scripted group (container) (typed FeaturePython)
  n = 8
  ref = H_element
FEATURE [App::DocumentObjectGroupPython] G4_lPROPANE  # scripted group (container) (typed FeaturePython)
  Dunit = g/cm3
  Dvalue = 0.43
  Group = -> [C_element097,H_element089]
  conduct = 2
  density = 1
  expand = 3
  formula = G4_lPROPANE
  name = G4_lPROPANE
  specific = 4
FEATURE [App::DocumentObjectGroupPython] C_element098  label="C_element : 056"  # scripted group (container) (typed FeaturePython)
  n = 3
  ref = C_element
FEATURE [App::DocumentObjectGroupPython] H_element090  label="H_element : 051"  # scripted group (container) (typed FeaturePython)
  n = 8
  ref = H_element
FEATURE [App::DocumentObjectGroupPython] O_element086  label="O_element : 047"  # scripted group (container) (typed FeaturePython)
  n = 1
  ref = O_element
FEATURE [App::DocumentObjectGroupPython] G4_N_PROPYL_ALCOHOL  label="G4_N-PROPYL_ALCOHOL"  # scripted group (container) (typed FeaturePython)
  Dunit = g/cm3
  Dvalue = 0.8035
  Group = -> [C_element098,H_element090,O_element086]
  conduct = 2
  density = 1
  expand = 3
  formula = G4_N-PROPYL_ALCOHOL
  name = G4_N-PROPYL_ALCOHOL
  specific = 4
FEATURE [App::DocumentObjectGroupPython] C_element099  label="C_element : 057"  # scripted group (container) (typed FeaturePython)
  n = 5
  ref = C_element
FEATURE [App::DocumentObjectGroupPython] H_element091  label="H_element : 052"  # scripted group (container) (typed FeaturePython)
  n = 5
  ref = H_element
FEATURE [App::DocumentObjectGroupPython] N_element038  label="N_element : 017"  # scripted group (container) (typed FeaturePython)
  n = 1
  ref = N_element
FEATURE [App::DocumentObjectGroupPython] G4_PYRIDINE  # scripted group (container) (typed FeaturePython)
  Dunit = g/cm3
  Dvalue = 0.9819
  Group = -> [C_element099,H_element091,N_element038]
  conduct = 2
  density = 1
  expand = 3
  formula = G4_PYRIDINE
  name = G4_PYRIDINE
  specific = 4
FEATURE [App::DocumentObjectGroupPython] H_element092  label="H_element : 0.144"  # scripted group (container) (typed FeaturePython)
  n = 0.143711
FEATURE [App::DocumentObjectGroupPython] C_element100  label="C_element : 0.856"  # scripted group (container) (typed FeaturePython)
  n = 0.856289
FEATURE [App::DocumentObjectGroupPython] G4_RUBBER_BUTYL  # scripted group (container) (typed FeaturePython)
  Dunit = g/cm3
  Dvalue = 0.92
  Group = -> [H_element092,C_element100]
  conduct = 2
  density = 1
  expand = 3
  formula = G4_RUBBER_BUTYL
  name = G4_RUBBER_BUTYL
  specific = 4
FEATURE [App::DocumentObjectGroupPython] H_element093  label="H_element : 0.118"  # scripted group (container) (typed FeaturePython)
  n = 0.118371
FEATURE [App::DocumentObjectGroupPython] C_element101  label="C_element : 0.882"  # scripted group (container) (typed FeaturePython)
  n = 0.881629
FEATURE [App::DocumentObjectGroupPython] G4_RUBBER_NATURAL  # scripted group (container) (typed FeaturePython)
  Dunit = g/cm3
  Dvalue = 0.92
  Group = -> [H_element093,C_element101]
  conduct = 2
  density = 1
  expand = 3
  formula = G4_RUBBER_NATURAL
  name = G4_RUBBER_NATURAL
  specific = 4
FEATURE [App::DocumentObjectGroupPython] H_element094  label="H_element : 0.145"  # scripted group (container) (typed FeaturePython)
  n = 0.05692
FEATURE [App::DocumentObjectGroupPython] C_element102  label="C_element : 0.543"  # scripted group (container) (typed FeaturePython)
  n = 0.542646
FEATURE [App::DocumentObjectGroupPython] Cl_element021  label="Cl_element : 0.400"  # scripted group (container) (typed FeaturePython)
  n = 0.400434
FEATURE [App::DocumentObjectGroupPython] G4_RUBBER_NEOPRENE  # scripted group (container) (typed FeaturePython)
  Dunit = g/cm3
  Dvalue = 1.23
  Group = -> [H_element094,C_element102,Cl_element021]
  conduct = 2
  density = 1
  expand = 3
  formula = G4_RUBBER_NEOPRENE
  name = G4_RUBBER_NEOPRENE
  specific = 4
FEATURE [App::DocumentObjectGroupPython] Si_element006  label="Si_element : 1"  # scripted group (container) (typed FeaturePython)
  n = 1
  ref = Si_element
FEATURE [App::DocumentObjectGroupPython] O_element087  label="O_element : 048"  # scripted group (container) (typed FeaturePython)
  n = 2
  ref = O_element
FEATURE [App::DocumentObjectGroupPython] G4_SILICON_DIOXIDE  # scripted group (container) (typed FeaturePython)
  Dunit = g/cm3
  Dvalue = 2.32
  Group = -> [Si_element006,O_element087]
  conduct = 2
  density = 1
  expand = 3
  formula = G4_SILICON_DIOXIDE
  name = G4_SILICON_DIOXIDE
  specific = 4
FEATURE [App::DocumentObjectGroupPython] Ag_element002  label="Ag_element : 1"  # scripted group (container) (typed FeaturePython)
  n = 1
  ref = Ag_element
FEATURE [App::DocumentObjectGroupPython] Br_element005  label="Br_element : 003"  # scripted group (container) (typed FeaturePython)
  n = 1
  ref = Br_element
FEATURE [App::DocumentObjectGroupPython] G4_SILVER_BROMIDE  # scripted group (container) (typed FeaturePython)
  Dunit = g/cm3
  Dvalue = 6.473
  Group = -> [Ag_element002,Br_element005]
  conduct = 2
  density = 1
  expand = 3
  formula = G4_SILVER_BROMIDE
  name = G4_SILVER_BROMIDE
  specific = 4
FEATURE [App::DocumentObjectGroupPython] Ag_element003  label="Ag_element : 002"  # scripted group (container) (typed FeaturePython)
  n = 1
  ref = Ag_element
FEATURE [App::DocumentObjectGroupPython] Cl_element022  label="Cl_element : 011"  # scripted group (container) (typed FeaturePython)
  n = 1
  ref = Cl_element
FEATURE [App::DocumentObjectGroupPython] G4_SILVER_CHLORIDE  # scripted group (container) (typed FeaturePython)
  Dunit = g/cm3
  Dvalue = 5.56
  Group = -> [Ag_element003,Cl_element022]
  conduct = 2
  density = 1
  expand = 3
  formula = G4_SILVER_CHLORIDE
  name = G4_SILVER_CHLORIDE
  specific = 4
FEATURE [App::DocumentObjectGroupPython] Br_element006  label="Br_element : 0.423"  # scripted group (container) (typed FeaturePython)
  n = 0.422895
FEATURE [App::DocumentObjectGroupPython] Ag_element004  label="Ag_element : 0.574"  # scripted group (container) (typed FeaturePython)
  n = 0.573748
FEATURE [App::DocumentObjectGroupPython] I_element007  label="I_element : 0.649"  # scripted group (container) (typed FeaturePython)
  n = 0.003357
FEATURE [App::DocumentObjectGroupPython] G4_SILVER_HALIDES  # scripted group (container) (typed FeaturePython)
  Dunit = g/cm3
  Dvalue = 6.47
  Group = -> [Br_element006,Ag_element004,I_element007]
  conduct = 2
  density = 1
  expand = 3
  formula = G4_SILVER_HALIDES
  name = G4_SILVER_HALIDES
  specific = 4
FEATURE [App::DocumentObjectGroupPython] Ag_element005  label="Ag_element : 003"  # scripted group (container) (typed FeaturePython)
  n = 1
  ref = Ag_element
FEATURE [App::DocumentObjectGroupPython] I_element008  label="I_element : 004"  # scripted group (container) (typed FeaturePython)
  n = 1
  ref = I_element
FEATURE [App::DocumentObjectGroupPython] G4_SILVER_IODIDE  # scripted group (container) (typed FeaturePython)
  Dunit = g/cm3
  Dvalue = 6.01
  Group = -> [Ag_element005,I_element008]
  conduct = 2
  density = 1
  expand = 3
  formula = G4_SILVER_IODIDE
  name = G4_SILVER_IODIDE
  specific = 4
FEATURE [App::DocumentObjectGroupPython] H_element095  label="H_element : 0.100"  # scripted group (container) (typed FeaturePython)
  n = 0.1
FEATURE [App::DocumentObjectGroupPython] C_element103  label="C_element : 0.204"  # scripted group (container) (typed FeaturePython)
  n = 0.204
FEATURE [App::DocumentObjectGroupPython] N_element039  label="N_element : 0.759"  # scripted group (container) (typed FeaturePython)
  n = 0.042
FEATURE [App::DocumentObjectGroupPython] O_element088  label="O_element : 0.645"  # scripted group (container) (typed FeaturePython)
  n = 0.645
FEATURE [App::DocumentObjectGroupPython] Na_element013  label="Na_element : 0.100"  # scripted group (container) (typed FeaturePython)
  n = 0.002
FEATURE [App::DocumentObjectGroupPython] P_element009  label="P_element : 0.107"  # scripted group (container) (typed FeaturePython)
  n = 0.001
FEATURE [App::DocumentObjectGroupPython] S_element020  label="S_element : 0.021"  # scripted group (container) (typed FeaturePython)
  n = 0.002
FEATURE [App::DocumentObjectGroupPython] Cl_element023  label="Cl_element : 0.590"  # scripted group (container) (typed FeaturePython)
  n = 0.003
FEATURE [App::DocumentObjectGroupPython] K_element010  label="K_element : 0.001"  # scripted group (container) (typed FeaturePython)
  n = 0.001
FEATURE [App::DocumentObjectGroupPython] G4_SKIN_ICRP  # scripted group (container) (typed FeaturePython)
  Dunit = g/cm3
  Dvalue = 1.09
  Group = -> [H_element095,C_element103,N_element039,O_element088,Na_element013,P_element009,S_element020,Cl_element023,K_element010]
  conduct = 2
  density = 1
  expand = 3
  formula = G4_SKIN_ICRP
  name = G4_SKIN_ICRP
  specific = 4
FEATURE [App::DocumentObjectGroupPython] Na_element014  label="Na_element : 2"  # scripted group (container) (typed FeaturePython)
  n = 2
  ref = Na_element
FEATURE [App::DocumentObjectGroupPython] C_element104  label="C_element : 058"  # scripted group (container) (typed FeaturePython)
  n = 1
  ref = C_element
FEATURE [App::DocumentObjectGroupPython] O_element089  label="O_element : 049"  # scripted group (container) (typed FeaturePython)
  n = 3
  ref = O_element
FEATURE [App::DocumentObjectGroupPython] G4_SODIUM_CARBONATE  # scripted group (container) (typed FeaturePython)
  Dunit = g/cm3
  Dvalue = 2.532
  Group = -> [Na_element014,C_element104,O_element089]
  conduct = 2
  density = 1
  expand = 3
  formula = G4_SODIUM_CARBONATE
  name = G4_SODIUM_CARBONATE
  specific = 4
FEATURE [App::DocumentObjectGroupPython] Na_element015  label="Na_element : 1"  # scripted group (container) (typed FeaturePython)
  n = 1
  ref = Na_element
FEATURE [App::DocumentObjectGroupPython] I_element009  label="I_element : 005"  # scripted group (container) (typed FeaturePython)
  n = 1
  ref = I_element
FEATURE [App::DocumentObjectGroupPython] G4_SODIUM_IODIDE  # scripted group (container) (typed FeaturePython)
  Dunit = g/cm3
  Dvalue = 3.667
  Group = -> [Na_element015,I_element009]
  conduct = 2
  density = 1
  expand = 3
  formula = G4_SODIUM_IODIDE
  name = G4_SODIUM_IODIDE
  specific = 4
FEATURE [App::DocumentObjectGroupPython] Na_element016  label="Na_element : 003"  # scripted group (container) (typed FeaturePython)
  n = 2
  ref = Na_element
FEATURE [App::DocumentObjectGroupPython] O_element090  label="O_element : 050"  # scripted group (container) (typed FeaturePython)
  n = 1
  ref = O_element
FEATURE [App::DocumentObjectGroupPython] G4_SODIUM_MONOXIDE  # scripted group (container) (typed FeaturePython)
  Dunit = g/cm3
  Dvalue = 2.27
  Group = -> [Na_element016,O_element090]
  conduct = 2
  density = 1
  expand = 3
  formula = G4_SODIUM_MONOXIDE
  name = G4_SODIUM_MONOXIDE
  specific = 4
FEATURE [App::DocumentObjectGroupPython] Na_element017  label="Na_element : 004"  # scripted group (container) (typed FeaturePython)
  n = 1
  ref = Na_element
FEATURE [App::DocumentObjectGroupPython] N_element040  label="N_element : 018"  # scripted group (container) (typed FeaturePython)
  n = 1
  ref = N_element
FEATURE [App::DocumentObjectGroupPython] O_element091  label="O_element : 051"  # scripted group (container) (typed FeaturePython)
  n = 3
  ref = O_element
FEATURE [App::DocumentObjectGroupPython] G4_SODIUM_NITRATE  # scripted group (container) (typed FeaturePython)
  Dunit = g/cm3
  Dvalue = 2.261
  Group = -> [Na_element017,N_element040,O_element091]
  conduct = 2
  density = 1
  expand = 3
  formula = G4_SODIUM_NITRATE
  name = G4_SODIUM_NITRATE
  specific = 4
FEATURE [App::DocumentObjectGroupPython] C_element105  label="C_element : 059"  # scripted group (container) (typed FeaturePython)
  n = 14
  ref = C_element
FEATURE [App::DocumentObjectGroupPython] H_element096  label="H_element : 053"  # scripted group (container) (typed FeaturePython)
  n = 12
  ref = H_element
FEATURE [App::DocumentObjectGroupPython] G4_STILBENE  # scripted group (container) (typed FeaturePython)
  Dunit = g/cm3
  Dvalue = 0.9707
  Group = -> [C_element105,H_element096]
  conduct = 2
  density = 1
  expand = 3
  formula = G4_STILBENE
  name = G4_STILBENE
  specific = 4
FEATURE [App::DocumentObjectGroupPython] C_element106  label="C_element : 12"  # scripted group (container) (typed FeaturePython)
  n = 12
  ref = C_element
FEATURE [App::DocumentObjectGroupPython] H_element097  label="H_element : 22"  # scripted group (container) (typed FeaturePython)
  n = 22
  ref = H_element
FEATURE [App::DocumentObjectGroupPython] O_element092  label="O_element : 11"  # scripted group (container) (typed FeaturePython)
  n = 11
  ref = O_element
FEATURE [App::DocumentObjectGroupPython] G4_SUCROSE  # scripted group (container) (typed FeaturePython)
  Dunit = g/cm3
  Dvalue = 1.5805
  Group = -> [C_element106,H_element097,O_element092]
  conduct = 2
  density = 1
  expand = 3
  formula = G4_SUCROSE
  name = G4_SUCROSE
  specific = 4
FEATURE [App::DocumentObjectGroupPython] C_element107  label="C_element : 18"  # scripted group (container) (typed FeaturePython)
  n = 18
  ref = C_element
FEATURE [App::DocumentObjectGroupPython] H_element098  label="H_element : 054"  # scripted group (container) (typed FeaturePython)
  n = 14
  ref = H_element
FEATURE [App::DocumentObjectGroupPython] G4_TERPHENYL  # scripted group (container) (typed FeaturePython)
  Dunit = g/cm3
  Dvalue = 1.24
  Group = -> [C_element107,H_element098]
  conduct = 2
  density = 1
  expand = 3
  formula = G4_TERPHENYL
  name = G4_TERPHENYL
  specific = 4
FEATURE [App::DocumentObjectGroupPython] H_element099  label="H_element : 0.146"  # scripted group (container) (typed FeaturePython)
  n = 0.106
FEATURE [App::DocumentObjectGroupPython] C_element108  label="C_element : 0.883"  # scripted group (container) (typed FeaturePython)
  n = 0.099
FEATURE [App::DocumentObjectGroupPython] N_element041  label="N_element : 0.020"  # scripted group (container) (typed FeaturePython)
  n = 0.02
FEATURE [App::DocumentObjectGroupPython] O_element093  label="O_element : 0.766"  # scripted group (container) (typed FeaturePython)
  n = 0.766
FEATURE [App::DocumentObjectGroupPython] Na_element018  label="Na_element : 0.101"  # scripted group (container) (typed FeaturePython)
  n = 0.002
FEATURE [App::DocumentObjectGroupPython] P_element010  label="P_element : 0.108"  # scripted group (container) (typed FeaturePython)
  n = 0.001
FEATURE [App::DocumentObjectGroupPython] S_element021  label="S_element : 0.022"  # scripted group (container) (typed FeaturePython)
  n = 0.002
FEATURE [App::DocumentObjectGroupPython] Cl_element024  label="Cl_element : 0.002"  # scripted group (container) (typed FeaturePython)
  n = 0.002
FEATURE [App::DocumentObjectGroupPython] K_element011  label="K_element : 0.017"  # scripted group (container) (typed FeaturePython)
  n = 0.002
FEATURE [App::DocumentObjectGroupPython] G4_TESTIS_ICRP  # scripted group (container) (typed FeaturePython)
  Dunit = g/cm3
  Dvalue = 1.04
  Group = -> [H_element099,C_element108,N_element041,O_element093,Na_element018,P_element010,S_element021,Cl_element024,K_element011]
  conduct = 2
  density = 1
  expand = 3
  formula = G4_TESTIS_ICRP
  name = G4_TESTIS_ICRP
  specific = 4
FEATURE [App::DocumentObjectGroupPython] C_element109  label="C_element : 060"  # scripted group (container) (typed FeaturePython)
  n = 2
  ref = C_element
FEATURE [App::DocumentObjectGroupPython] Cl_element025  label="Cl_element : 012"  # scripted group (container) (typed FeaturePython)
  n = 4
  ref = Cl_element
FEATURE [App::DocumentObjectGroupPython] G4_TETRACHLOROETHYLENE  # scripted group (container) (typed FeaturePython)
  Dunit = g/cm3
  Dvalue = 1.625
  Group = -> [C_element109,Cl_element025]
  conduct = 2
  density = 1
  expand = 3
  formula = G4_TETRACHLOROETHYLENE
  name = G4_TETRACHLOROETHYLENE
  specific = 4
FEATURE [App::DocumentObjectGroupPython] Tl_element001  label="Tl_element : 1"  # scripted group (container) (typed FeaturePython)
  n = 1
  ref = Tl_element
FEATURE [App::DocumentObjectGroupPython] Cl_element026  label="Cl_element : 013"  # scripted group (container) (typed FeaturePython)
  n = 1
  ref = Cl_element
FEATURE [App::DocumentObjectGroupPython] G4_THALLIUM_CHLORIDE  # scripted group (container) (typed FeaturePython)
  Dunit = g/cm3
  Dvalue = 7.004
  Group = -> [Tl_element001,Cl_element026]
  conduct = 2
  density = 1
  expand = 3
  formula = G4_THALLIUM_CHLORIDE
  name = G4_THALLIUM_CHLORIDE
  specific = 4
FEATURE [App::DocumentObjectGroupPython] H_element100  label="H_element : 0.147"  # scripted group (container) (typed FeaturePython)
  n = 0.105
FEATURE [App::DocumentObjectGroupPython] C_element110  label="C_element : 0.256"  # scripted group (container) (typed FeaturePython)
  n = 0.256
FEATURE [App::DocumentObjectGroupPython] N_element042  label="N_element : 0.760"  # scripted group (container) (typed FeaturePython)
  n = 0.027
FEATURE [App::DocumentObjectGroupPython] O_element094  label="O_element : 0.602"  # scripted group (container) (typed FeaturePython)
  n = 0.602
FEATURE [App::DocumentObjectGroupPython] Na_element019  label="Na_element : 0.102"  # scripted group (container) (typed FeaturePython)
  n = 0.001
FEATURE [App::DocumentObjectGroupPython] P_element011  label="P_element : 0.109"  # scripted group (container) (typed FeaturePython)
  n = 0.002
FEATURE [App::DocumentObjectGroupPython] S_element022  label="S_element : 0.023"  # scripted group (container) (typed FeaturePython)
  n = 0.003
FEATURE [App::DocumentObjectGroupPython] Cl_element027  label="Cl_element : 0.591"  # scripted group (container) (typed FeaturePython)
  n = 0.002
FEATURE [App::DocumentObjectGroupPython] K_element012  label="K_element : 0.018"  # scripted group (container) (typed FeaturePython)
  n = 0.002
FEATURE [App::DocumentObjectGroupPython] G4_TISSUE_SOFT_ICRP  # scripted group (container) (typed FeaturePython)
  Dunit = g/cm3
  Dvalue = 1.03
  Group = -> [H_element100,C_element110,N_element042,O_element094,Na_element019,P_element011,S_element022,Cl_element027,K_element012]
  conduct = 2
  density = 1
  expand = 3
  formula = G4_TISSUE_SOFT_ICRP
  name = G4_TISSUE_SOFT_ICRP
  specific = 4
FEATURE [App::DocumentObjectGroupPython] H_element101  label="H_element : 0.148"  # scripted group (container) (typed FeaturePython)
  n = 0.101
FEATURE [App::DocumentObjectGroupPython] C_element111  label="C_element : 0.111"  # scripted group (container) (typed FeaturePython)
  n = 0.111
FEATURE [App::DocumentObjectGroupPython] N_element043  label="N_element : 0.026"  # scripted group (container) (typed FeaturePython)
  n = 0.026
FEATURE [App::DocumentObjectGroupPython] O_element095  label="O_element : 0.762"  # scripted group (container) (typed FeaturePython)
  n = 0.762
FEATURE [App::DocumentObjectGroupPython] G4_TISSUE_SOFT_ICRU_4  label="G4_TISSUE_SOFT_ICRU-4"  # scripted group (container) (typed FeaturePython)
  Dunit = g/cm3
  Dvalue = 1
  Group = -> [H_element101,C_element111,N_element043,O_element095]
  conduct = 2
  density = 1
  expand = 3
  formula = G4_TISSUE_SOFT_ICRU-4
  name = G4_TISSUE_SOFT_ICRU-4
  specific = 4
FEATURE [App::DocumentObjectGroupPython] H_element102  label="H_element : 0.149"  # scripted group (container) (typed FeaturePython)
  n = 0.101869
FEATURE [App::DocumentObjectGroupPython] C_element112  label="C_element : 0.456"  # scripted group (container) (typed FeaturePython)
  n = 0.456179
FEATURE [App::DocumentObjectGroupPython] N_element044  label="N_element : 0.761"  # scripted group (container) (typed FeaturePython)
  n = 0.035172
FEATURE [App::DocumentObjectGroupPython] O_element096  label="O_element : 0.407"  # scripted group (container) (typed FeaturePython)
  n = 0.40678
FEATURE [App::DocumentObjectGroupPython] G4_TISSUE_METHANE  label="G4_TISSUE-METHANE"  # scripted group (container) (typed FeaturePython)
  Dunit = g/cm3
  Dvalue = 0.00106409
  Group = -> [H_element102,C_element112,N_element044,O_element096]
  conduct = 2
  density = 1
  expand = 3
  formula = G4_TISSUE-METHANE
  name = G4_TISSUE-METHANE
  specific = 4
FEATURE [App::DocumentObjectGroupPython] H_element103  label="H_element : 0.103"  # scripted group (container) (typed FeaturePython)
  n = 0.102672
FEATURE [App::DocumentObjectGroupPython] C_element113  label="C_element : 0.569"  # scripted group (container) (typed FeaturePython)
  n = 0.56894
FEATURE [App::DocumentObjectGroupPython] N_element045  label="N_element : 0.762"  # scripted group (container) (typed FeaturePython)
  n = 0.035022
FEATURE [App::DocumentObjectGroupPython] O_element097  label="O_element : 0.293"  # scripted group (container) (typed FeaturePython)
  n = 0.293366
FEATURE [App::DocumentObjectGroupPython] G4_TISSUE_PROPANE  label="G4_TISSUE-PROPANE"  # scripted group (container) (typed FeaturePython)
  Dunit = g/cm3
  Dvalue = 0.00182628
  Group = -> [H_element103,C_element113,N_element045,O_element097]
  conduct = 2
  density = 1
  expand = 3
  formula = G4_TISSUE-PROPANE
  name = G4_TISSUE-PROPANE
  specific = 4
FEATURE [App::DocumentObjectGroupPython] Ti_element003  label="Ti_element : 1"  # scripted group (container) (typed FeaturePython)
  n = 1
  ref = Ti_element
FEATURE [App::DocumentObjectGroupPython] O_element098  label="O_element : 052"  # scripted group (container) (typed FeaturePython)
  n = 2
  ref = O_element
FEATURE [App::DocumentObjectGroupPython] G4_TITANIUM_DIOXIDE  # scripted group (container) (typed FeaturePython)
  Dunit = g/cm3
  Dvalue = 4.26
  Group = -> [Ti_element003,O_element098]
  conduct = 2
  density = 1
  expand = 3
  formula = G4_TITANIUM_DIOXIDE
  name = G4_TITANIUM_DIOXIDE
  specific = 4
FEATURE [App::DocumentObjectGroupPython] C_element114  label="C_element : 061"  # scripted group (container) (typed FeaturePython)
  n = 7
  ref = C_element
FEATURE [App::DocumentObjectGroupPython] H_element104  label="H_element : 055"  # scripted group (container) (typed FeaturePython)
  n = 8
  ref = H_element
FEATURE [App::DocumentObjectGroupPython] G4_TOLUENE  # scripted group (container) (typed FeaturePython)
  Dunit = g/cm3
  Dvalue = 0.8669
  Group = -> [C_element114,H_element104]
  conduct = 2
  density = 1
  expand = 3
  formula = G4_TOLUENE
  name = G4_TOLUENE
  specific = 4
FEATURE [App::DocumentObjectGroupPython] C_element115  label="C_element : 062"  # scripted group (container) (typed FeaturePython)
  n = 2
  ref = C_element
FEATURE [App::DocumentObjectGroupPython] H_element105  label="H_element : 056"  # scripted group (container) (typed FeaturePython)
  n = 1
  ref = H_element
FEATURE [App::DocumentObjectGroupPython] Cl_element028  label="Cl_element : 014"  # scripted group (container) (typed FeaturePython)
  n = 3
  ref = Cl_element
FEATURE [App::DocumentObjectGroupPython] G4_TRICHLOROETHYLENE  # scripted group (container) (typed FeaturePython)
  Dunit = g/cm3
  Dvalue = 1.46
  Group = -> [C_element115,H_element105,Cl_element028]
  conduct = 2
  density = 1
  expand = 3
  formula = G4_TRICHLOROETHYLENE
  name = G4_TRICHLOROETHYLENE
  specific = 4
FEATURE [App::DocumentObjectGroupPython] C_element116  label="C_element : 063"  # scripted group (container) (typed FeaturePython)
  n = 6
  ref = C_element
FEATURE [App::DocumentObjectGroupPython] H_element106  label="H_element : 15"  # scripted group (container) (typed FeaturePython)
  n = 15
  ref = H_element
FEATURE [App::DocumentObjectGroupPython] O_element099  label="O_element : 053"  # scripted group (container) (typed FeaturePython)
  n = 4
  ref = O_element
FEATURE [App::DocumentObjectGroupPython] P_element012  label="P_element : 1"  # scripted group (container) (typed FeaturePython)
  n = 1
  ref = P_element
FEATURE [App::DocumentObjectGroupPython] G4_TRIETHYL_PHOSPHATE  # scripted group (container) (typed FeaturePython)
  Dunit = g/cm3
  Dvalue = 1.07
  Group = -> [C_element116,H_element106,O_element099,P_element012]
  conduct = 2
  density = 1
  expand = 3
  formula = G4_TRIETHYL_PHOSPHATE
  name = G4_TRIETHYL_PHOSPHATE
  specific = 4
FEATURE [App::DocumentObjectGroupPython] W_element003  label="W_element : 003"  # scripted group (container) (typed FeaturePython)
  n = 1
  ref = W_element
FEATURE [App::DocumentObjectGroupPython] F_element017  label="F_element : 6"  # scripted group (container) (typed FeaturePython)
  n = 6
  ref = F_element
FEATURE [App::DocumentObjectGroupPython] G4_TUNGSTEN_HEXAFLUORIDE  # scripted group (container) (typed FeaturePython)
  Dunit = g/cm3
  Dvalue = 2.4
  Group = -> [W_element003,F_element017]
  conduct = 2
  density = 1
  expand = 3
  formula = G4_TUNGSTEN_HEXAFLUORIDE
  name = G4_TUNGSTEN_HEXAFLUORIDE
  specific = 4
FEATURE [App::DocumentObjectGroupPython] U_element001  label="U_element : 1"  # scripted group (container) (typed FeaturePython)
  n = 1
  ref = U_element
FEATURE [App::DocumentObjectGroupPython] C_element117  label="C_element : 064"  # scripted group (container) (typed FeaturePython)
  n = 2
  ref = C_element
FEATURE [App::DocumentObjectGroupPython] G4_URANIUM_DICARBIDE  # scripted group (container) (typed FeaturePython)
  Dunit = g/cm3
  Dvalue = 11.28
  Group = -> [U_element001,C_element117]
  conduct = 2
  density = 1
  expand = 3
  formula = G4_URANIUM_DICARBIDE
  name = G4_URANIUM_DICARBIDE
  specific = 4
FEATURE [App::DocumentObjectGroupPython] U_element002  label="U_element : 002"  # scripted group (container) (typed FeaturePython)
  n = 1
  ref = U_element
FEATURE [App::DocumentObjectGroupPython] C_element118  label="C_element : 065"  # scripted group (container) (typed FeaturePython)
  n = 1
  ref = C_element
FEATURE [App::DocumentObjectGroupPython] G4_URANIUM_MONOCARBIDE  # scripted group (container) (typed FeaturePython)
  Dunit = g/cm3
  Dvalue = 13.63
  Group = -> [U_element002,C_element118]
  conduct = 2
  density = 1
  expand = 3
  formula = G4_URANIUM_MONOCARBIDE
  name = G4_URANIUM_MONOCARBIDE
  specific = 4
FEATURE [App::DocumentObjectGroupPython] U_element003  label="U_element : 003"  # scripted group (container) (typed FeaturePython)
  n = 1
  ref = U_element
FEATURE [App::DocumentObjectGroupPython] O_element100  label="O_element : 054"  # scripted group (container) (typed FeaturePython)
  n = 2
  ref = O_element
FEATURE [App::DocumentObjectGroupPython] G4_URANIUM_OXIDE  # scripted group (container) (typed FeaturePython)
  Dunit = g/cm3
  Dvalue = 10.96
  Group = -> [U_element003,O_element100]
  conduct = 2
  density = 1
  expand = 3
  formula = G4_URANIUM_OXIDE
  name = G4_URANIUM_OXIDE
  specific = 4
FEATURE [App::DocumentObjectGroupPython] C_element119  label="C_element : 066"  # scripted group (container) (typed FeaturePython)
  n = 1
  ref = C_element
FEATURE [App::DocumentObjectGroupPython] H_element107  label="H_element : 057"  # scripted group (container) (typed FeaturePython)
  n = 4
  ref = H_element
FEATURE [App::DocumentObjectGroupPython] N_element046  label="N_element : 019"  # scripted group (container) (typed FeaturePython)
  n = 2
  ref = N_element
FEATURE [App::DocumentObjectGroupPython] O_element101  label="O_element : 055"  # scripted group (container) (typed FeaturePython)
  n = 1
  ref = O_element
FEATURE [App::DocumentObjectGroupPython] G4_UREA  # scripted group (container) (typed FeaturePython)
  Dunit = g/cm3
  Dvalue = 1.323
  Group = -> [C_element119,H_element107,N_element046,O_element101]
  conduct = 2
  density = 1
  expand = 3
  formula = G4_UREA
  name = G4_UREA
  specific = 4
FEATURE [App::DocumentObjectGroupPython] C_element120  label="C_element : 067"  # scripted group (container) (typed FeaturePython)
  n = 5
  ref = C_element
FEATURE [App::DocumentObjectGroupPython] H_element108  label="H_element : 058"  # scripted group (container) (typed FeaturePython)
  n = 11
  ref = H_element
FEATURE [App::DocumentObjectGroupPython] N_element047  label="N_element : 020"  # scripted group (container) (typed FeaturePython)
  n = 1
  ref = N_element
FEATURE [App::DocumentObjectGroupPython] O_element102  label="O_element : 056"  # scripted group (container) (typed FeaturePython)
  n = 2
  ref = O_element
FEATURE [App::DocumentObjectGroupPython] G4_VALINE  # scripted group (container) (typed FeaturePython)
  Dunit = g/cm3
  Dvalue = 1.23
  Group = -> [C_element120,H_element108,N_element047,O_element102]
  conduct = 2
  density = 1
  expand = 3
  formula = G4_VALINE
  name = G4_VALINE
  specific = 4
FEATURE [App::DocumentObjectGroupPython] H_element109  label="H_element : 0.009"  # scripted group (container) (typed FeaturePython)
  n = 0.009417
FEATURE [App::DocumentObjectGroupPython] C_element121  label="C_element : 0.281"  # scripted group (container) (typed FeaturePython)
  n = 0.280555
FEATURE [App::DocumentObjectGroupPython] F_element018  label="F_element : 0.710"  # scripted group (container) (typed FeaturePython)
  n = 0.710028
FEATURE [App::DocumentObjectGroupPython] G4_VITON  # scripted group (container) (typed FeaturePython)
  Dunit = g/cm3
  Dvalue = 1.8
  Group = -> [H_element109,C_element121,F_element018]
  conduct = 2
  density = 1
  expand = 3
  formula = G4_VITON
  name = G4_VITON
  specific = 4
FEATURE [App::DocumentObjectGroupPython] H_element110  label="H_element : 059"  # scripted group (container) (typed FeaturePython)
  n = 2
  ref = H_element
FEATURE [App::DocumentObjectGroupPython] O_element103  label="O_element : 057"  # scripted group (container) (typed FeaturePython)
  n = 1
  ref = O_element
FEATURE [App::DocumentObjectGroupPython] G4_WATER  # scripted group (container) (typed FeaturePython)
  Dunit = g/cm3
  Dvalue = 1
  Group = -> [H_element110,O_element103]
  conduct = 2
  density = 1
  expand = 3
  formula = G4_WATER
  name = G4_WATER
  specific = 4
FEATURE [App::DocumentObjectGroupPython] H_element111  label="H_element : 060"  # scripted group (container) (typed FeaturePython)
  n = 2
  ref = H_element
FEATURE [App::DocumentObjectGroupPython] O_element104  label="O_element : 058"  # scripted group (container) (typed FeaturePython)
  n = 1
  ref = O_element
FEATURE [App::DocumentObjectGroupPython] G4_WATER_VAPOR  # scripted group (container) (typed FeaturePython)
  Dunit = g/cm3
  Dvalue = 0.000756182
  Group = -> [H_element111,O_element104]
  conduct = 2
  density = 1
  expand = 3
  formula = G4_WATER_VAPOR
  name = G4_WATER_VAPOR
  specific = 4
FEATURE [App::DocumentObjectGroupPython] C_element122  label="C_element : 068"  # scripted group (container) (typed FeaturePython)
  n = 8
  ref = C_element
FEATURE [App::DocumentObjectGroupPython] H_element112  label="H_element : 061"  # scripted group (container) (typed FeaturePython)
  n = 10
  ref = H_element
FEATURE [App::DocumentObjectGroupPython] G4_XYLENE  # scripted group (container) (typed FeaturePython)
  Dunit = g/cm3
  Dvalue = 0.87
  Group = -> [C_element122,H_element112]
  conduct = 2
  density = 1
  expand = 3
  formula = G4_XYLENE
  name = G4_XYLENE
  specific = 4
FEATURE [App::DocumentObjectGroupPython] C_element123  label="C_element : 069"  # scripted group (container) (typed FeaturePython)
  n = 1
  ref = C_element
FEATURE [App::DocumentObjectGroupPython] G4_GRAPHITE  # scripted group (container) (typed FeaturePython)
  Dunit = g/cm3
  Dvalue = 2.21
  Group = -> [C_element123]
  conduct = 2
  density = 1
  expand = 3
  formula = G4_GRAPHITE
  name = G4_GRAPHITE
  specific = 4
FEATURE [App::DocumentObjectGroupPython] NIST  # scripted group (container) (typed FeaturePython)
  Group = -> [G4_A_150_TISSUE,G4_ACETONE,G4_ACETYLENE,G4_ADENINE,G4_ADIPOSE_TISSUE_ICRP,G4_AIR,G4_ALANINE,G4_ALUMINUM_OXIDE,G4_AMBER,G4_AMMONIA,G4_ANILINE,G4_ANTHRACENE,G4_B_100_BONE,G4_BAKELITE,G4_BARIUM_FLUORIDE,G4_BARIUM_SULFATE,G4_BENZENE,G4_BERYLLIUM_OXIDE,G4_BGO,G4_BLOOD_ICRP,G4_BONE_COMPACT_ICRU,G4_BONE_CORTICAL_ICRP,G4_BORON_CARBIDE,G4_BORON_OXIDE,G4_BRAIN_ICRP,G4_BUTANE,G4_N_BUTYL_ALCOHOL,G4_C_552,+152 more]
FEATURE [App::DocumentObjectGroupPython] H_element113  label="H_element : 062"  # scripted group (container) (typed FeaturePython)
  n = 1
  ref = H_element
FEATURE [App::DocumentObjectGroupPython] G4_H  # scripted group (container) (typed FeaturePython)
  Dunit = g/cm3
  Dvalue = 8.3748e-05
  Group = -> [H_element113]
  conduct = 2
  density = 1
  expand = 3
  formula = H
  name = G4_H
  specific = 4
FEATURE [App::DocumentObjectGroupPython] He_element001  label="He_element : 1"  # scripted group (container) (typed FeaturePython)
  n = 1
  ref = He_element
FEATURE [App::DocumentObjectGroupPython] G4_He  # scripted group (container) (typed FeaturePython)
  Dunit = g/cm3
  Dvalue = 0.000166322
  Group = -> [He_element001]
  conduct = 2
  density = 1
  expand = 3
  formula = He
  name = G4_He
  specific = 4
FEATURE [App::DocumentObjectGroupPython] Li_element008  label="Li_element : 008"  # scripted group (container) (typed FeaturePython)
  n = 1
  ref = Li_element
FEATURE [App::DocumentObjectGroupPython] G4_Li  # scripted group (container) (typed FeaturePython)
  Dunit = g/cm3
  Dvalue = 0.534
  Group = -> [Li_element008]
  conduct = 2
  density = 1
  expand = 3
  formula = Li
  name = G4_Li
  specific = 4
FEATURE [App::DocumentObjectGroupPython] Be_element002  label="Be_element : 002"  # scripted group (container) (typed FeaturePython)
  n = 1
  ref = Be_element
FEATURE [App::DocumentObjectGroupPython] G4_Be  # scripted group (container) (typed FeaturePython)
  Dunit = g/cm3
  Dvalue = 1.848
  Group = -> [Be_element002]
  conduct = 2
  density = 1
  expand = 3
  formula = Be
  name = G4_Be
  specific = 4
FEATURE [App::DocumentObjectGroupPython] B_element007  label="B_element : 007"  # scripted group (container) (typed FeaturePython)
  n = 1
  ref = B_element
FEATURE [App::DocumentObjectGroupPython] G4_B  # scripted group (container) (typed FeaturePython)
  Dunit = g/cm3
  Dvalue = 2.37
  Group = -> [B_element007]
  conduct = 2
  density = 1
  expand = 3
  formula = B
  name = G4_B
  specific = 4
FEATURE [App::DocumentObjectGroupPython] C_element124  label="C_element : 070"  # scripted group (container) (typed FeaturePython)
  n = 1
  ref = C_element
FEATURE [App::DocumentObjectGroupPython] G4_C  # scripted group (container) (typed FeaturePython)
  Dunit = g/cm3
  Dvalue = 2
  Group = -> [C_element124]
  conduct = 2
  density = 1
  expand = 3
  formula = C
  name = G4_C
  specific = 4
FEATURE [App::DocumentObjectGroupPython] N_element048  label="N_element : 021"  # scripted group (container) (typed FeaturePython)
  n = 1
  ref = N_element
FEATURE [App::DocumentObjectGroupPython] G4_N  # scripted group (container) (typed FeaturePython)
  Dunit = g/cm3
  Dvalue = 0.0011652
  Group = -> [N_element048]
  conduct = 2
  density = 1
  expand = 3
  formula = N
  name = G4_N
  specific = 4
FEATURE [App::DocumentObjectGroupPython] O_element105  label="O_element : 059"  # scripted group (container) (typed FeaturePython)
  n = 1
  ref = O_element
FEATURE [App::DocumentObjectGroupPython] G4_O  # scripted group (container) (typed FeaturePython)
  Dunit = g/cm3
  Dvalue = 0.00133151
  Group = -> [O_element105]
  conduct = 2
  density = 1
  expand = 3
  formula = O
  name = G4_O
  specific = 4
FEATURE [App::DocumentObjectGroupPython] F_element019  label="F_element : 008"  # scripted group (container) (typed FeaturePython)
  n = 1
  ref = F_element
FEATURE [App::DocumentObjectGroupPython] G4_F  # scripted group (container) (typed FeaturePython)
  Dunit = g/cm3
  Dvalue = 0.00158029
  Group = -> [F_element019]
  conduct = 2
  density = 1
  expand = 3
  formula = F
  name = G4_F
  specific = 4
FEATURE [App::DocumentObjectGroupPython] Ne_element001  label="Ne_element : 1"  # scripted group (container) (typed FeaturePython)
  n = 1
  ref = Ne_element
FEATURE [App::DocumentObjectGroupPython] G4_Ne  # scripted group (container) (typed FeaturePython)
  Dunit = g/cm3
  Dvalue = 0.000838505
  Group = -> [Ne_element001]
  conduct = 2
  density = 1
  expand = 3
  formula = Ne
  name = G4_Ne
  specific = 4
FEATURE [App::DocumentObjectGroupPython] Na_element020  label="Na_element : 005"  # scripted group (container) (typed FeaturePython)
  n = 1
  ref = Na_element
FEATURE [App::DocumentObjectGroupPython] G4_Na  # scripted group (container) (typed FeaturePython)
  Dunit = g/cm3
  Dvalue = 0.971
  Group = -> [Na_element020]
  conduct = 2
  density = 1
  expand = 3
  formula = Na
  name = G4_Na
  specific = 4
FEATURE [App::DocumentObjectGroupPython] Mg_element011  label="Mg_element : 005"  # scripted group (container) (typed FeaturePython)
  n = 1
  ref = Mg_element
FEATURE [App::DocumentObjectGroupPython] G4_Mg  # scripted group (container) (typed FeaturePython)
  Dunit = g/cm3
  Dvalue = 1.74
  Group = -> [Mg_element011]
  conduct = 2
  density = 1
  expand = 3
  formula = Mg
  name = G4_Mg
  specific = 4
FEATURE [App::DocumentObjectGroupPython] Al_element004  label="Al_element : 1"  # scripted group (container) (typed FeaturePython)
  n = 1
  ref = Al_element
FEATURE [App::DocumentObjectGroupPython] G4_Al  # scripted group (container) (typed FeaturePython)
  Dunit = g/cm3
  Dvalue = 2.699
  Group = -> [Al_element004]
  conduct = 2
  density = 1
  expand = 3
  formula = Al
  name = G4_Al
  specific = 4
FEATURE [App::DocumentObjectGroupPython] Si_element007  label="Si_element : 002"  # scripted group (container) (typed FeaturePython)
  n = 1
  ref = Si_element
FEATURE [App::DocumentObjectGroupPython] G4_Si  # scripted group (container) (typed FeaturePython)
  Dunit = g/cm3
  Dvalue = 2.33
  Group = -> [Si_element007]
  conduct = 2
  density = 1
  expand = 3
  formula = Si
  name = G4_Si
  specific = 4
FEATURE [App::DocumentObjectGroupPython] P_element013  label="P_element : 002"  # scripted group (container) (typed FeaturePython)
  n = 1
  ref = P_element
FEATURE [App::DocumentObjectGroupPython] G4_P  # scripted group (container) (typed FeaturePython)
  Dunit = g/cm3
  Dvalue = 2.2
  Group = -> [P_element013]
  conduct = 2
  density = 1
  expand = 3
  formula = P
  name = G4_P
  specific = 4
FEATURE [App::DocumentObjectGroupPython] S_element023  label="S_element : 007"  # scripted group (container) (typed FeaturePython)
  n = 1
  ref = S_element
FEATURE [App::DocumentObjectGroupPython] G4_S  # scripted group (container) (typed FeaturePython)
  Dunit = g/cm3
  Dvalue = 2
  Group = -> [S_element023]
  conduct = 2
  density = 1
  expand = 3
  formula = S
  name = G4_S
  specific = 4
FEATURE [App::DocumentObjectGroupPython] Cl_element029  label="Cl_element : 015"  # scripted group (container) (typed FeaturePython)
  n = 1
  ref = Cl_element
FEATURE [App::DocumentObjectGroupPython] G4_Cl  # scripted group (container) (typed FeaturePython)
  Dunit = g/cm3
  Dvalue = 0.00299473
  Group = -> [Cl_element029]
  conduct = 2
  density = 1
  expand = 3
  formula = Cl
  name = G4_Cl
  specific = 4
FEATURE [App::DocumentObjectGroupPython] Ar_element002  label="Ar_element : 1"  # scripted group (container) (typed FeaturePython)
  n = 1
  ref = Ar_element
FEATURE [App::DocumentObjectGroupPython] G4_Ar  # scripted group (container) (typed FeaturePython)
  Dunit = g/cm3
  Dvalue = 0.00166201
  Group = -> [Ar_element002]
  conduct = 2
  density = 1
  expand = 3
  formula = Ar
  name = G4_Ar
  specific = 4
FEATURE [App::DocumentObjectGroupPython] K_element013  label="K_element : 003"  # scripted group (container) (typed FeaturePython)
  n = 1
  ref = K_element
FEATURE [App::DocumentObjectGroupPython] G4_K  # scripted group (container) (typed FeaturePython)
  Dunit = g/cm3
  Dvalue = 0.862
  Group = -> [K_element013]
  conduct = 2
  density = 1
  expand = 3
  formula = K
  name = G4_K
  specific = 4
FEATURE [App::DocumentObjectGroupPython] Ca_element014  label="Ca_element : 007"  # scripted group (container) (typed FeaturePython)
  n = 1
  ref = Ca_element
FEATURE [App::DocumentObjectGroupPython] G4_Ca  # scripted group (container) (typed FeaturePython)
  Dunit = g/cm3
  Dvalue = 1.55
  Group = -> [Ca_element014]
  conduct = 2
  density = 1
  expand = 3
  formula = Ca
  name = G4_Ca
  specific = 4
FEATURE [App::DocumentObjectGroupPython] Sc_element001  label="Sc_element : 1"  # scripted group (container) (typed FeaturePython)
  n = 1
  ref = Sc_element
FEATURE [App::DocumentObjectGroupPython] G4_Sc  # scripted group (container) (typed FeaturePython)
  Dunit = g/cm3
  Dvalue = 2.989
  Group = -> [Sc_element001]
  conduct = 2
  density = 1
  expand = 3
  formula = Sc
  name = G4_Sc
  specific = 4
FEATURE [App::DocumentObjectGroupPython] Ti_element004  label="Ti_element : 002"  # scripted group (container) (typed FeaturePython)
  n = 1
  ref = Ti_element
FEATURE [App::DocumentObjectGroupPython] G4_Ti  # scripted group (container) (typed FeaturePython)
  Dunit = g/cm3
  Dvalue = 4.54
  Group = -> [Ti_element004]
  conduct = 2
  density = 1
  expand = 3
  formula = Ti
  name = G4_Ti
  specific = 4
FEATURE [App::DocumentObjectGroupPython] V_element001  label="V_element : 1"  # scripted group (container) (typed FeaturePython)
  n = 1
  ref = V_element
FEATURE [App::DocumentObjectGroupPython] G4_V  # scripted group (container) (typed FeaturePython)
  Dunit = g/cm3
  Dvalue = 6.11
  Group = -> [V_element001]
  conduct = 2
  density = 1
  expand = 3
  formula = V
  name = G4_V
  specific = 4
FEATURE [App::DocumentObjectGroupPython] Cr_element001  label="Cr_element : 1"  # scripted group (container) (typed FeaturePython)
  n = 1
  ref = Cr_element
FEATURE [App::DocumentObjectGroupPython] G4_Cr  # scripted group (container) (typed FeaturePython)
  Dunit = g/cm3
  Dvalue = 7.18
  Group = -> [Cr_element001]
  conduct = 2
  density = 1
  expand = 3
  formula = Cr
  name = G4_Cr
  specific = 4
FEATURE [App::DocumentObjectGroupPython] Mn_element001  label="Mn_element : 1"  # scripted group (container) (typed FeaturePython)
  n = 1
  ref = Mn_element
FEATURE [App::DocumentObjectGroupPython] G4_Mn  # scripted group (container) (typed FeaturePython)
  Dunit = g/cm3
  Dvalue = 7.44
  Group = -> [Mn_element001]
  conduct = 2
  density = 1
  expand = 3
  formula = Mn
  name = G4_Mn
  specific = 4
FEATURE [App::DocumentObjectGroupPython] Fe_element007  label="Fe_element : 004"  # scripted group (container) (typed FeaturePython)
  n = 1
  ref = Fe_element
FEATURE [App::DocumentObjectGroupPython] G4_Fe  # scripted group (container) (typed FeaturePython)
  Dunit = g/cm3
  Dvalue = 7.874
  Group = -> [Fe_element007]
  conduct = 2
  density = 1
  expand = 3
  formula = Fe
  name = G4_Fe
  specific = 4
FEATURE [App::DocumentObjectGroupPython] Co_element001  label="Co_element : 1"  # scripted group (container) (typed FeaturePython)
  n = 1
  ref = Co_element
FEATURE [App::DocumentObjectGroupPython] G4_Co  # scripted group (container) (typed FeaturePython)
  Dunit = g/cm3
  Dvalue = 8.9
  Group = -> [Co_element001]
  conduct = 2
  density = 1
  expand = 3
  formula = Co
  name = G4_Co
  specific = 4
FEATURE [App::DocumentObjectGroupPython] Ni_element001  label="Ni_element : 1"  # scripted group (container) (typed FeaturePython)
  n = 1
  ref = Ni_element
FEATURE [App::DocumentObjectGroupPython] G4_Ni  # scripted group (container) (typed FeaturePython)
  Dunit = g/cm3
  Dvalue = 8.902
  Group = -> [Ni_element001]
  conduct = 2
  density = 1
  expand = 3
  formula = Ni
  name = G4_Ni
  specific = 4
FEATURE [App::DocumentObjectGroupPython] Cu_element001  label="Cu_element : 1"  # scripted group (container) (typed FeaturePython)
  n = 1
  ref = Cu_element
FEATURE [App::DocumentObjectGroupPython] G4_Cu  # scripted group (container) (typed FeaturePython)
  Dunit = g/cm3
  Dvalue = 8.96
  Group = -> [Cu_element001]
  conduct = 2
  density = 1
  expand = 3
  formula = Cu
  name = G4_Cu
  specific = 4
FEATURE [App::DocumentObjectGroupPython] Zn_element001  label="Zn_element : 1"  # scripted group (container) (typed FeaturePython)
  n = 1
  ref = Zn_element
FEATURE [App::DocumentObjectGroupPython] G4_Zn  # scripted group (container) (typed FeaturePython)
  Dunit = g/cm3
  Dvalue = 7.133
  Group = -> [Zn_element001]
  conduct = 2
  density = 1
  expand = 3
  formula = Zn
  name = G4_Zn
  specific = 4
FEATURE [App::DocumentObjectGroupPython] Ga_element002  label="Ga_element : 002"  # scripted group (container) (typed FeaturePython)
  n = 1
  ref = Ga_element
FEATURE [App::DocumentObjectGroupPython] G4_Ga  # scripted group (container) (typed FeaturePython)
  Dunit = g/cm3
  Dvalue = 5.904
  Group = -> [Ga_element002]
  conduct = 2
  density = 1
  expand = 3
  formula = Ga
  name = G4_Ga
  specific = 4
FEATURE [App::DocumentObjectGroupPython] Ge_element002  label="Ge_element : 1"  # scripted group (container) (typed FeaturePython)
  n = 1
  ref = Ge_element
FEATURE [App::DocumentObjectGroupPython] G4_Ge  # scripted group (container) (typed FeaturePython)
  Dunit = g/cm3
  Dvalue = 5.323
  Group = -> [Ge_element002]
  conduct = 2
  density = 1
  expand = 3
  formula = Ge
  name = G4_Ge
  specific = 4
FEATURE [App::DocumentObjectGroupPython] As_element003  label="As_element : 002"  # scripted group (container) (typed FeaturePython)
  n = 1
  ref = As_element
FEATURE [App::DocumentObjectGroupPython] G4_As  # scripted group (container) (typed FeaturePython)
  Dunit = g/cm3
  Dvalue = 5.73
  Group = -> [As_element003]
  conduct = 2
  density = 1
  expand = 3
  formula = As
  name = G4_As
  specific = 4
FEATURE [App::DocumentObjectGroupPython] Se_element001  label="Se_element : 1"  # scripted group (container) (typed FeaturePython)
  n = 1
  ref = Se_element
FEATURE [App::DocumentObjectGroupPython] G4_Se  # scripted group (container) (typed FeaturePython)
  Dunit = g/cm3
  Dvalue = 4.5
  Group = -> [Se_element001]
  conduct = 2
  density = 1
  expand = 3
  formula = Se
  name = G4_Se
  specific = 4
FEATURE [App::DocumentObjectGroupPython] Br_element007  label="Br_element : 004"  # scripted group (container) (typed FeaturePython)
  n = 1
  ref = Br_element
FEATURE [App::DocumentObjectGroupPython] G4_Br  # scripted group (container) (typed FeaturePython)
  Dunit = g/cm3
  Dvalue = 0.0070721
  Group = -> [Br_element007]
  conduct = 2
  density = 1
  expand = 3
  formula = Br
  name = G4_Br
  specific = 4
FEATURE [App::DocumentObjectGroupPython] Kr_element001  label="Kr_element : 1"  # scripted group (container) (typed FeaturePython)
  n = 1
  ref = Kr_element
FEATURE [App::DocumentObjectGroupPython] G4_Kr  # scripted group (container) (typed FeaturePython)
  Dunit = g/cm3
  Dvalue = 0.00347832
  Group = -> [Kr_element001]
  conduct = 2
  density = 1
  expand = 3
  formula = Kr
  name = G4_Kr
  specific = 4
FEATURE [App::DocumentObjectGroupPython] Rb_element001  label="Rb_element : 1"  # scripted group (container) (typed FeaturePython)
  n = 1
  ref = Rb_element
FEATURE [App::DocumentObjectGroupPython] G4_Rb  # scripted group (container) (typed FeaturePython)
  Dunit = g/cm3
  Dvalue = 1.532
  Group = -> [Rb_element001]
  conduct = 2
  density = 1
  expand = 3
  formula = Rb
  name = G4_Rb
  specific = 4
FEATURE [App::DocumentObjectGroupPython] Sr_element001  label="Sr_element : 1"  # scripted group (container) (typed FeaturePython)
  n = 1
  ref = Sr_element
FEATURE [App::DocumentObjectGroupPython] G4_Sr  # scripted group (container) (typed FeaturePython)
  Dunit = g/cm3
  Dvalue = 2.54
  Group = -> [Sr_element001]
  conduct = 2
  density = 1
  expand = 3
  formula = Sr
  name = G4_Sr
  specific = 4
FEATURE [App::DocumentObjectGroupPython] Y_element001  label="Y_element : 1"  # scripted group (container) (typed FeaturePython)
  n = 1
  ref = Y_element
FEATURE [App::DocumentObjectGroupPython] G4_Y  # scripted group (container) (typed FeaturePython)
  Dunit = g/cm3
  Dvalue = 4.469
  Group = -> [Y_element001]
  conduct = 2
  density = 1
  expand = 3
  formula = Y
  name = G4_Y
  specific = 4
FEATURE [App::DocumentObjectGroupPython] Zr_element001  label="Zr_element : 1"  # scripted group (container) (typed FeaturePython)
  n = 1
  ref = Zr_element
FEATURE [App::DocumentObjectGroupPython] G4_Zr  # scripted group (container) (typed FeaturePython)
  Dunit = g/cm3
  Dvalue = 6.506
  Group = -> [Zr_element001]
  conduct = 2
  density = 1
  expand = 3
  formula = Zr
  name = G4_Zr
  specific = 4
FEATURE [App::DocumentObjectGroupPython] Nb_element001  label="Nb_element : 1"  # scripted group (container) (typed FeaturePython)
  n = 1
  ref = Nb_element
FEATURE [App::DocumentObjectGroupPython] G4_Nb  # scripted group (container) (typed FeaturePython)
  Dunit = g/cm3
  Dvalue = 8.57
  Group = -> [Nb_element001]
  conduct = 2
  density = 1
  expand = 3
  formula = Nb
  name = G4_Nb
  specific = 4
FEATURE [App::DocumentObjectGroupPython] Mo_element001  label="Mo_element : 1"  # scripted group (container) (typed FeaturePython)
  n = 1
  ref = Mo_element
FEATURE [App::DocumentObjectGroupPython] G4_Mo  # scripted group (container) (typed FeaturePython)
  Dunit = g/cm3
  Dvalue = 10.22
  Group = -> [Mo_element001]
  conduct = 2
  density = 1
  expand = 3
  formula = Mo
  name = G4_Mo
  specific = 4
FEATURE [App::DocumentObjectGroupPython] Tc_element001  label="Tc_element : 1"  # scripted group (container) (typed FeaturePython)
  n = 1
  ref = Tc_element
FEATURE [App::DocumentObjectGroupPython] G4_Tc  # scripted group (container) (typed FeaturePython)
  Dunit = g/cm3
  Dvalue = 11.5
  Group = -> [Tc_element001]
  conduct = 2
  density = 1
  expand = 3
  formula = Tc
  name = G4_Tc
  specific = 4
FEATURE [App::DocumentObjectGroupPython] Ru_element001  label="Ru_element : 1"  # scripted group (container) (typed FeaturePython)
  n = 1
  ref = Ru_element
FEATURE [App::DocumentObjectGroupPython] G4_Ru  # scripted group (container) (typed FeaturePython)
  Dunit = g/cm3
  Dvalue = 12.41
  Group = -> [Ru_element001]
  conduct = 2
  density = 1
  expand = 3
  formula = Ru
  name = G4_Ru
  specific = 4
FEATURE [App::DocumentObjectGroupPython] Rh_element001  label="Rh_element : 1"  # scripted group (container) (typed FeaturePython)
  n = 1
  ref = Rh_element
FEATURE [App::DocumentObjectGroupPython] G4_Rh  # scripted group (container) (typed FeaturePython)
  Dunit = g/cm3
  Dvalue = 12.41
  Group = -> [Rh_element001]
  conduct = 2
  density = 1
  expand = 3
  formula = Rh
  name = G4_Rh
  specific = 4
FEATURE [App::DocumentObjectGroupPython] Pd_element001  label="Pd_element : 1"  # scripted group (container) (typed FeaturePython)
  n = 1
  ref = Pd_element
FEATURE [App::DocumentObjectGroupPython] G4_Pd  # scripted group (container) (typed FeaturePython)
  Dunit = g/cm3
  Dvalue = 12.02
  Group = -> [Pd_element001]
  conduct = 2
  density = 1
  expand = 3
  formula = Pd
  name = G4_Pd
  specific = 4
FEATURE [App::DocumentObjectGroupPython] Ag_element006  label="Ag_element : 004"  # scripted group (container) (typed FeaturePython)
  n = 1
  ref = Ag_element
FEATURE [App::DocumentObjectGroupPython] G4_Ag  # scripted group (container) (typed FeaturePython)
  Dunit = g/cm3
  Dvalue = 10.5
  Group = -> [Ag_element006]
  conduct = 2
  density = 1
  expand = 3
  formula = Ag
  name = G4_Ag
  specific = 4
FEATURE [App::DocumentObjectGroupPython] Cd_element003  label="Cd_element : 003"  # scripted group (container) (typed FeaturePython)
  n = 1
  ref = Cd_element
FEATURE [App::DocumentObjectGroupPython] G4_Cd  # scripted group (container) (typed FeaturePython)
  Dunit = g/cm3
  Dvalue = 8.65
  Group = -> [Cd_element003]
  conduct = 2
  density = 1
  expand = 3
  formula = Cd
  name = G4_Cd
  specific = 4
FEATURE [App::DocumentObjectGroupPython] In_element001  label="In_element : 1"  # scripted group (container) (typed FeaturePython)
  n = 1
  ref = In_element
FEATURE [App::DocumentObjectGroupPython] G4_In  # scripted group (container) (typed FeaturePython)
  Dunit = g/cm3
  Dvalue = 7.31
  Group = -> [In_element001]
  conduct = 2
  density = 1
  expand = 3
  formula = In
  name = G4_In
  specific = 4
FEATURE [App::DocumentObjectGroupPython] Sn_element001  label="Sn_element : 1"  # scripted group (container) (typed FeaturePython)
  n = 1
  ref = Sn_element
FEATURE [App::DocumentObjectGroupPython] G4_Sn  # scripted group (container) (typed FeaturePython)
  Dunit = g/cm3
  Dvalue = 7.31
  Group = -> [Sn_element001]
  conduct = 2
  density = 1
  expand = 3
  formula = Sn
  name = G4_Sn
  specific = 4
FEATURE [App::DocumentObjectGroupPython] Sb_element001  label="Sb_element : 1"  # scripted group (container) (typed FeaturePython)
  n = 1
  ref = Sb_element
FEATURE [App::DocumentObjectGroupPython] G4_Sb  # scripted group (container) (typed FeaturePython)
  Dunit = g/cm3
  Dvalue = 6.691
  Group = -> [Sb_element001]
  conduct = 2
  density = 1
  expand = 3
  formula = Sb
  name = G4_Sb
  specific = 4
FEATURE [App::DocumentObjectGroupPython] Te_element002  label="Te_element : 002"  # scripted group (container) (typed FeaturePython)
  n = 1
  ref = Te_element
FEATURE [App::DocumentObjectGroupPython] G4_Te  # scripted group (container) (typed FeaturePython)
  Dunit = g/cm3
  Dvalue = 6.24
  Group = -> [Te_element002]
  conduct = 2
  density = 1
  expand = 3
  formula = Te
  name = G4_Te
  specific = 4
FEATURE [App::DocumentObjectGroupPython] I_element010  label="I_element : 006"  # scripted group (container) (typed FeaturePython)
  n = 1
  ref = I_element
FEATURE [App::DocumentObjectGroupPython] G4_I  # scripted group (container) (typed FeaturePython)
  Dunit = g/cm3
  Dvalue = 4.93
  Group = -> [I_element010]
  conduct = 2
  density = 1
  expand = 3
  formula = I
  name = G4_I
  specific = 4
FEATURE [App::DocumentObjectGroupPython] Xe_element001  label="Xe_element : 1"  # scripted group (container) (typed FeaturePython)
  n = 1
  ref = Xe_element
FEATURE [App::DocumentObjectGroupPython] G4_Xe  # scripted group (container) (typed FeaturePython)
  Dunit = g/cm3
  Dvalue = 0.00548536
  Group = -> [Xe_element001]
  conduct = 2
  density = 1
  expand = 3
  formula = Xe
  name = G4_Xe
  specific = 4
FEATURE [App::DocumentObjectGroupPython] Cs_element003  label="Cs_element : 003"  # scripted group (container) (typed FeaturePython)
  n = 1
  ref = Cs_element
FEATURE [App::DocumentObjectGroupPython] G4_Cs  # scripted group (container) (typed FeaturePython)
  Dunit = g/cm3
  Dvalue = 1.873
  Group = -> [Cs_element003]
  conduct = 2
  density = 1
  expand = 3
  formula = Cs
  name = G4_Cs
  specific = 4
FEATURE [App::DocumentObjectGroupPython] Ba_element003  label="Ba_element : 003"  # scripted group (container) (typed FeaturePython)
  n = 1
  ref = Ba_element
FEATURE [App::DocumentObjectGroupPython] G4_Ba  # scripted group (container) (typed FeaturePython)
  Dunit = g/cm3
  Dvalue = 3.5
  Group = -> [Ba_element003]
  conduct = 2
  density = 1
  expand = 3
  formula = Ba
  name = G4_Ba
  specific = 4
FEATURE [App::DocumentObjectGroupPython] La_element003  label="La_element : 003"  # scripted group (container) (typed FeaturePython)
  n = 1
  ref = La_element
FEATURE [App::DocumentObjectGroupPython] G4_La  # scripted group (container) (typed FeaturePython)
  Dunit = g/cm3
  Dvalue = 6.154
  Group = -> [La_element003]
  conduct = 2
  density = 1
  expand = 3
  formula = La
  name = G4_La
  specific = 4
FEATURE [App::DocumentObjectGroupPython] Ce_element002  label="Ce_element : 1"  # scripted group (container) (typed FeaturePython)
  n = 1
  ref = Ce_element
FEATURE [App::DocumentObjectGroupPython] G4_Ce  # scripted group (container) (typed FeaturePython)
  Dunit = g/cm3
  Dvalue = 6.657
  Group = -> [Ce_element002]
  conduct = 2
  density = 1
  expand = 3
  formula = Ce
  name = G4_Ce
  specific = 4
FEATURE [App::DocumentObjectGroupPython] Pr_element001  label="Pr_element : 1"  # scripted group (container) (typed FeaturePython)
  n = 1
  ref = Pr_element
FEATURE [App::DocumentObjectGroupPython] G4_Pr  # scripted group (container) (typed FeaturePython)
  Dunit = g/cm3
  Dvalue = 6.71
  Group = -> [Pr_element001]
  conduct = 2
  density = 1
  expand = 3
  formula = Pr
  name = G4_Pr
  specific = 4
FEATURE [App::DocumentObjectGroupPython] Nd_element001  label="Nd_element : 1"  # scripted group (container) (typed FeaturePython)
  n = 1
  ref = Nd_element
FEATURE [App::DocumentObjectGroupPython] G4_Nd  # scripted group (container) (typed FeaturePython)
  Dunit = g/cm3
  Dvalue = 6.9
  Group = -> [Nd_element001]
  conduct = 2
  density = 1
  expand = 3
  formula = Nd
  name = G4_Nd
  specific = 4
FEATURE [App::DocumentObjectGroupPython] Pm_element001  label="Pm_element : 1"  # scripted group (container) (typed FeaturePython)
  n = 1
  ref = Pm_element
FEATURE [App::DocumentObjectGroupPython] G4_Pm  # scripted group (container) (typed FeaturePython)
  Dunit = g/cm3
  Dvalue = 7.22
  Group = -> [Pm_element001]
  conduct = 2
  density = 1
  expand = 3
  formula = Pm
  name = G4_Pm
  specific = 4
FEATURE [App::DocumentObjectGroupPython] Sm_element001  label="Sm_element : 1"  # scripted group (container) (typed FeaturePython)
  n = 1
  ref = Sm_element
FEATURE [App::DocumentObjectGroupPython] G4_Sm  # scripted group (container) (typed FeaturePython)
  Dunit = g/cm3
  Dvalue = 7.46
  Group = -> [Sm_element001]
  conduct = 2
  density = 1
  expand = 3
  formula = Sm
  name = G4_Sm
  specific = 4
FEATURE [App::DocumentObjectGroupPython] Eu_element001  label="Eu_element : 1"  # scripted group (container) (typed FeaturePython)
  n = 1
  ref = Eu_element
FEATURE [App::DocumentObjectGroupPython] G4_Eu  # scripted group (container) (typed FeaturePython)
  Dunit = g/cm3
  Dvalue = 5.243
  Group = -> [Eu_element001]
  conduct = 2
  density = 1
  expand = 3
  formula = Eu
  name = G4_Eu
  specific = 4
FEATURE [App::DocumentObjectGroupPython] Gd_element002  label="Gd_element : 1"  # scripted group (container) (typed FeaturePython)
  n = 1
  ref = Gd_element
FEATURE [App::DocumentObjectGroupPython] G4_Gd  # scripted group (container) (typed FeaturePython)
  Dunit = g/cm3
  Dvalue = 7.9004
  Group = -> [Gd_element002]
  conduct = 2
  density = 1
  expand = 3
  formula = Gd
  name = G4_Gd
  specific = 4
FEATURE [App::DocumentObjectGroupPython] Tb_element001  label="Tb_element : 1"  # scripted group (container) (typed FeaturePython)
  n = 1
  ref = Tb_element
FEATURE [App::DocumentObjectGroupPython] G4_Tb  # scripted group (container) (typed FeaturePython)
  Dunit = g/cm3
  Dvalue = 8.229
  Group = -> [Tb_element001]
  conduct = 2
  density = 1
  expand = 3
  formula = Tb
  name = G4_Tb
  specific = 4
FEATURE [App::DocumentObjectGroupPython] Dy_element001  label="Dy_element : 1"  # scripted group (container) (typed FeaturePython)
  n = 1
  ref = Dy_element
FEATURE [App::DocumentObjectGroupPython] G4_Dy  # scripted group (container) (typed FeaturePython)
  Dunit = g/cm3
  Dvalue = 8.55
  Group = -> [Dy_element001]
  conduct = 2
  density = 1
  expand = 3
  formula = Dy
  name = G4_Dy
  specific = 4
FEATURE [App::DocumentObjectGroupPython] Ho_element001  label="Ho_element : 1"  # scripted group (container) (typed FeaturePython)
  n = 1
  ref = Ho_element
FEATURE [App::DocumentObjectGroupPython] G4_Ho  # scripted group (container) (typed FeaturePython)
  Dunit = g/cm3
  Dvalue = 8.795
  Group = -> [Ho_element001]
  conduct = 2
  density = 1
  expand = 3
  formula = Ho
  name = G4_Ho
  specific = 4
FEATURE [App::DocumentObjectGroupPython] Er_element001  label="Er_element : 1"  # scripted group (container) (typed FeaturePython)
  n = 1
  ref = Er_element
FEATURE [App::DocumentObjectGroupPython] G4_Er  # scripted group (container) (typed FeaturePython)
  Dunit = g/cm3
  Dvalue = 9.066
  Group = -> [Er_element001]
  conduct = 2
  density = 1
  expand = 3
  formula = Er
  name = G4_Er
  specific = 4
FEATURE [App::DocumentObjectGroupPython] Tm_element001  label="Tm_element : 1"  # scripted group (container) (typed FeaturePython)
  n = 1
  ref = Tm_element
FEATURE [App::DocumentObjectGroupPython] G4_Tm  # scripted group (container) (typed FeaturePython)
  Dunit = g/cm3
  Dvalue = 9.321
  Group = -> [Tm_element001]
  conduct = 2
  density = 1
  expand = 3
  formula = Tm
  name = G4_Tm
  specific = 4
FEATURE [App::DocumentObjectGroupPython] Yb_element001  label="Yb_element : 1"  # scripted group (container) (typed FeaturePython)
  n = 1
  ref = Yb_element
FEATURE [App::DocumentObjectGroupPython] G4_Yb  # scripted group (container) (typed FeaturePython)
  Dunit = g/cm3
  Dvalue = 6.73
  Group = -> [Yb_element001]
  conduct = 2
  density = 1
  expand = 3
  formula = Yb
  name = G4_Yb
  specific = 4
FEATURE [App::DocumentObjectGroupPython] Lu_element001  label="Lu_element : 1"  # scripted group (container) (typed FeaturePython)
  n = 1
  ref = Lu_element
FEATURE [App::DocumentObjectGroupPython] G4_Lu  # scripted group (container) (typed FeaturePython)
  Dunit = g/cm3
  Dvalue = 9.84
  Group = -> [Lu_element001]
  conduct = 2
  density = 1
  expand = 3
  formula = Lu
  name = G4_Lu
  specific = 4
FEATURE [App::DocumentObjectGroupPython] Hf_element001  label="Hf_element : 1"  # scripted group (container) (typed FeaturePython)
  n = 1
  ref = Hf_element
FEATURE [App::DocumentObjectGroupPython] G4_Hf  # scripted group (container) (typed FeaturePython)
  Dunit = g/cm3
  Dvalue = 13.31
  Group = -> [Hf_element001]
  conduct = 2
  density = 1
  expand = 3
  formula = Hf
  name = G4_Hf
  specific = 4
FEATURE [App::DocumentObjectGroupPython] Ta_element001  label="Ta_element : 1"  # scripted group (container) (typed FeaturePython)
  n = 1
  ref = Ta_element
FEATURE [App::DocumentObjectGroupPython] G4_Ta  # scripted group (container) (typed FeaturePython)
  Dunit = g/cm3
  Dvalue = 16.654
  Group = -> [Ta_element001]
  conduct = 2
  density = 1
  expand = 3
  formula = Ta
  name = G4_Ta
  specific = 4
FEATURE [App::DocumentObjectGroupPython] W_element004  label="W_element : 004"  # scripted group (container) (typed FeaturePython)
  n = 1
  ref = W_element
FEATURE [App::DocumentObjectGroupPython] G4_W  # scripted group (container) (typed FeaturePython)
  Dunit = g/cm3
  Dvalue = 19.3
  Group = -> [W_element004]
  conduct = 2
  density = 1
  expand = 3
  formula = W
  name = G4_W
  specific = 4
FEATURE [App::DocumentObjectGroupPython] Re_element001  label="Re_element : 1"  # scripted group (container) (typed FeaturePython)
  n = 1
  ref = Re_element
FEATURE [App::DocumentObjectGroupPython] G4_Re  # scripted group (container) (typed FeaturePython)
  Dunit = g/cm3
  Dvalue = 21.02
  Group = -> [Re_element001]
  conduct = 2
  density = 1
  expand = 3
  formula = Re
  name = G4_Re
  specific = 4
FEATURE [App::DocumentObjectGroupPython] Os_element001  label="Os_element : 1"  # scripted group (container) (typed FeaturePython)
  n = 1
  ref = Os_element
FEATURE [App::DocumentObjectGroupPython] G4_Os  # scripted group (container) (typed FeaturePython)
  Dunit = g/cm3
  Dvalue = 22.57
  Group = -> [Os_element001]
  conduct = 2
  density = 1
  expand = 3
  formula = Os
  name = G4_Os
  specific = 4
FEATURE [App::DocumentObjectGroupPython] Ir_element001  label="Ir_element : 1"  # scripted group (container) (typed FeaturePython)
  n = 1
  ref = Ir_element
FEATURE [App::DocumentObjectGroupPython] G4_Ir  # scripted group (container) (typed FeaturePython)
  Dunit = g/cm3
  Dvalue = 22.42
  Group = -> [Ir_element001]
  conduct = 2
  density = 1
  expand = 3
  formula = Ir
  name = G4_Ir
  specific = 4
FEATURE [App::DocumentObjectGroupPython] Pt_element001  label="Pt_element : 1"  # scripted group (container) (typed FeaturePython)
  n = 1
  ref = Pt_element
FEATURE [App::DocumentObjectGroupPython] G4_Pt  # scripted group (container) (typed FeaturePython)
  Dunit = g/cm3
  Dvalue = 21.45
  Group = -> [Pt_element001]
  conduct = 2
  density = 1
  expand = 3
  formula = Pt
  name = G4_Pt
  specific = 4
FEATURE [App::DocumentObjectGroupPython] Au_element001  label="Au_element : 1"  # scripted group (container) (typed FeaturePython)
  n = 1
  ref = Au_element
FEATURE [App::DocumentObjectGroupPython] G4_Au  # scripted group (container) (typed FeaturePython)
  Dunit = g/cm3
  Dvalue = 19.32
  Group = -> [Au_element001]
  conduct = 2
  density = 1
  expand = 3
  formula = Au
  name = G4_Au
  specific = 4
FEATURE [App::DocumentObjectGroupPython] Hg_element002  label="Hg_element : 002"  # scripted group (container) (typed FeaturePython)
  n = 1
  ref = Hg_element
FEATURE [App::DocumentObjectGroupPython] G4_Hg  # scripted group (container) (typed FeaturePython)
  Dunit = g/cm3
  Dvalue = 13.546
  Group = -> [Hg_element002]
  conduct = 2
  density = 1
  expand = 3
  formula = Hg
  name = G4_Hg
  specific = 4
FEATURE [App::DocumentObjectGroupPython] Tl_element002  label="Tl_element : 002"  # scripted group (container) (typed FeaturePython)
  n = 1
  ref = Tl_element
FEATURE [App::DocumentObjectGroupPython] G4_Tl  # scripted group (container) (typed FeaturePython)
  Dunit = g/cm3
  Dvalue = 11.72
  Group = -> [Tl_element002]
  conduct = 2
  density = 1
  expand = 3
  formula = Tl
  name = G4_Tl
  specific = 4
FEATURE [App::DocumentObjectGroupPython] Pb_element003  label="Pb_element : 1"  # scripted group (container) (typed FeaturePython)
  n = 1
  ref = Pb_element
FEATURE [App::DocumentObjectGroupPython] G4_Pb  # scripted group (container) (typed FeaturePython)
  Dunit = g/cm3
  Dvalue = 11.35
  Group = -> [Pb_element003]
  conduct = 2
  density = 1
  expand = 3
  formula = Pb
  name = G4_Pb
  specific = 4
FEATURE [App::DocumentObjectGroupPython] Bi_element002  label="Bi_element : 1"  # scripted group (container) (typed FeaturePython)
  n = 1
  ref = Bi_element
FEATURE [App::DocumentObjectGroupPython] G4_Bi  # scripted group (container) (typed FeaturePython)
  Dunit = g/cm3
  Dvalue = 9.747
  Group = -> [Bi_element002]
  conduct = 2
  density = 1
  expand = 3
  formula = Bi
  name = G4_Bi
  specific = 4
FEATURE [App::DocumentObjectGroupPython] Po_element001  label="Po_element : 1"  # scripted group (container) (typed FeaturePython)
  n = 1
  ref = Po_element
FEATURE [App::DocumentObjectGroupPython] G4_Po  # scripted group (container) (typed FeaturePython)
  Dunit = g/cm3
  Dvalue = 9.32
  Group = -> [Po_element001]
  conduct = 2
  density = 1
  expand = 3
  formula = Po
  name = G4_Po
  specific = 4
FEATURE [App::DocumentObjectGroupPython] At_element001  label="At_element : 1"  # scripted group (container) (typed FeaturePython)
  n = 1
  ref = At_element
FEATURE [App::DocumentObjectGroupPython] G4_At  # scripted group (container) (typed FeaturePython)
  Dunit = g/cm3
  Dvalue = 9.32
  Group = -> [At_element001]
  conduct = 2
  density = 1
  expand = 3
  formula = At
  name = G4_At
  specific = 4
FEATURE [App::DocumentObjectGroupPython] Rn_element001  label="Rn_element : 1"  # scripted group (container) (typed FeaturePython)
  n = 1
  ref = Rn_element
FEATURE [App::DocumentObjectGroupPython] G4_Rn  # scripted group (container) (typed FeaturePython)
  Dunit = g/cm3
  Dvalue = 0.00900662
  Group = -> [Rn_element001]
  conduct = 2
  density = 1
  expand = 3
  formula = Rn
  name = G4_Rn
  specific = 4
FEATURE [App::DocumentObjectGroupPython] Fr_element001  label="Fr_element : 1"  # scripted group (container) (typed FeaturePython)
  n = 1
  ref = Fr_element
FEATURE [App::DocumentObjectGroupPython] G4_Fr  # scripted group (container) (typed FeaturePython)
  Dunit = g/cm3
  Dvalue = 1
  Group = -> [Fr_element001]
  conduct = 2
  density = 1
  expand = 3
  formula = Fr
  name = G4_Fr
  specific = 4
FEATURE [App::DocumentObjectGroupPython] Ra_element001  label="Ra_element : 1"  # scripted group (container) (typed FeaturePython)
  n = 1
  ref = Ra_element
FEATURE [App::DocumentObjectGroupPython] G4_Ra  # scripted group (container) (typed FeaturePython)
  Dunit = g/cm3
  Dvalue = 5
  Group = -> [Ra_element001]
  conduct = 2
  density = 1
  expand = 3
  formula = Ra
  name = G4_Ra
  specific = 4
FEATURE [App::DocumentObjectGroupPython] Ac_element001  label="Ac_element : 1"  # scripted group (container) (typed FeaturePython)
  n = 1
  ref = Ac_element
FEATURE [App::DocumentObjectGroupPython] G4_Ac  # scripted group (container) (typed FeaturePython)
  Dunit = g/cm3
  Dvalue = 10.07
  Group = -> [Ac_element001]
  conduct = 2
  density = 1
  expand = 3
  formula = Ac
  name = G4_Ac
  specific = 4
FEATURE [App::DocumentObjectGroupPython] Th_element001  label="Th_element : 1"  # scripted group (container) (typed FeaturePython)
  n = 1
  ref = Th_element
FEATURE [App::DocumentObjectGroupPython] G4_Th  # scripted group (container) (typed FeaturePython)
  Dunit = g/cm3
  Dvalue = 11.72
  Group = -> [Th_element001]
  conduct = 2
  density = 1
  expand = 3
  formula = Th
  name = G4_Th
  specific = 4
FEATURE [App::DocumentObjectGroupPython] Pa_element001  label="Pa_element : 1"  # scripted group (container) (typed FeaturePython)
  n = 1
  ref = Pa_element
FEATURE [App::DocumentObjectGroupPython] G4_Pa  # scripted group (container) (typed FeaturePython)
  Dunit = g/cm3
  Dvalue = 15.37
  Group = -> [Pa_element001]
  conduct = 2
  density = 1
  expand = 3
  formula = Pa
  name = G4_Pa
  specific = 4
FEATURE [App::DocumentObjectGroupPython] U_element004  label="U_element : 004"  # scripted group (container) (typed FeaturePython)
  n = 1
  ref = U_element
FEATURE [App::DocumentObjectGroupPython] G4_U  # scripted group (container) (typed FeaturePython)
  Dunit = g/cm3
  Dvalue = 18.95
  Group = -> [U_element004]
  conduct = 2
  density = 1
  expand = 3
  formula = U
  name = G4_U
  specific = 4
FEATURE [App::DocumentObjectGroupPython] Np_element001  label="Np_element : 1"  # scripted group (container) (typed FeaturePython)
  n = 1
  ref = Np_element
FEATURE [App::DocumentObjectGroupPython] G4_Np  # scripted group (container) (typed FeaturePython)
  Dunit = g/cm3
  Dvalue = 20.25
  Group = -> [Np_element001]
  conduct = 2
  density = 1
  expand = 3
  formula = Np
  name = G4_Np
  specific = 4
FEATURE [App::DocumentObjectGroupPython] Pu_element002  label="Pu_element : 002"  # scripted group (container) (typed FeaturePython)
  n = 1
  ref = Pu_element
FEATURE [App::DocumentObjectGroupPython] G4_Pu  # scripted group (container) (typed FeaturePython)
  Dunit = g/cm3
  Dvalue = 19.84
  Group = -> [Pu_element002]
  conduct = 2
  density = 1
  expand = 3
  formula = Pu
  name = G4_Pu
  specific = 4
FEATURE [App::DocumentObjectGroupPython] Am_element001  label="Am_element : 1"  # scripted group (container) (typed FeaturePython)
  n = 1
  ref = Am_element
FEATURE [App::DocumentObjectGroupPython] G4_Am  # scripted group (container) (typed FeaturePython)
  Dunit = g/cm3
  Dvalue = 13.67
  Group = -> [Am_element001]
  conduct = 2
  density = 1
  expand = 3
  formula = Am
  name = G4_Am
  specific = 4
FEATURE [App::DocumentObjectGroupPython] Cm_element001  label="Cm_element : 1"  # scripted group (container) (typed FeaturePython)
  n = 1
  ref = Cm_element
FEATURE [App::DocumentObjectGroupPython] G4_Cm  # scripted group (container) (typed FeaturePython)
  Dunit = g/cm3
  Dvalue = 13.51
  Group = -> [Cm_element001]
  conduct = 2
  density = 1
  expand = 3
  formula = Cm
  name = G4_Cm
  specific = 4
FEATURE [App::DocumentObjectGroupPython] Bk_element001  label="Bk_element : 1"  # scripted group (container) (typed FeaturePython)
  n = 1
  ref = Bk_element
FEATURE [App::DocumentObjectGroupPython] G4_Bk  # scripted group (container) (typed FeaturePython)
  Dunit = g/cm3
  Dvalue = 14
  Group = -> [Bk_element001]
  conduct = 2
  density = 1
  expand = 3
  formula = Bk
  name = G4_Bk
  specific = 4
FEATURE [App::DocumentObjectGroupPython] Cf_element001  label="Cf_element : 1"  # scripted group (container) (typed FeaturePython)
  n = 1
  ref = Cf_element
FEATURE [App::DocumentObjectGroupPython] G4_Cf  # scripted group (container) (typed FeaturePython)
  Dunit = g/cm3
  Dvalue = 10
  Group = -> [Cf_element001]
  conduct = 2
  density = 1
  expand = 3
  formula = Cf
  name = G4_Cf
  specific = 4
FEATURE [App::DocumentObjectGroupPython] Element  # scripted group (container) (typed FeaturePython)
  Group = -> [G4_H,G4_He,G4_Li,G4_Be,G4_B,G4_C,G4_N,G4_O,G4_F,G4_Ne,G4_Na,G4_Mg,G4_Al,G4_Si,G4_P,G4_S,G4_Cl,G4_Ar,G4_K,G4_Ca,G4_Sc,G4_Ti,G4_V,G4_Cr,G4_Mn,G4_Fe,G4_Co,G4_Ni,G4_Cu,G4_Zn,G4_Ga,G4_Ge,G4_As,G4_Se,G4_Br,G4_Kr,G4_Rb,G4_Sr,G4_Y,G4_Zr,G4_Nb,G4_Mo,G4_Tc,G4_Ru,G4_Rh,G4_Pd,G4_Ag,G4_Cd,G4_In,G4_Sn,G4_Sb,G4_Te,G4_I,G4_Xe,G4_Cs,G4_Ba,G4_La,G4_Ce,G4_Pr,G4_Nd,G4_Pm,G4_Sm,G4_Eu,G4_Gd,G4_Tb,G4_Dy,G4_Ho,G4_Er,+30 more]
FEATURE [App::DocumentObjectGroupPython] H_element114  label="H_element : 063"  # scripted group (container) (typed FeaturePython)
  n = 2
  ref = H_element
FEATURE [App::DocumentObjectGroupPython] G4_lH2  # scripted group (container) (typed FeaturePython)
  Dunit = g/cm3
  Dvalue = 0.0708
  Group = -> [H_element114]
  conduct = 2
  density = 1
  expand = 3
  formula = G4_lH2
  name = G4_lH2
  specific = 4
FEATURE [App::DocumentObjectGroupPython] N_element049  label="N_element : 022"  # scripted group (container) (typed FeaturePython)
  n = 2
  ref = N_element
FEATURE [App::DocumentObjectGroupPython] G4_lN2  # scripted group (container) (typed FeaturePython)
  Dunit = g/cm3
  Dvalue = 0.807
  Group = -> [N_element049]
  conduct = 2
  density = 1
  expand = 3
  formula = G4_lN2
  name = G4_lN2
  specific = 4
FEATURE [App::DocumentObjectGroupPython] O_element106  label="O_element : 060"  # scripted group (container) (typed FeaturePython)
  n = 2
  ref = O_element
FEATURE [App::DocumentObjectGroupPython] G4_lO2  # scripted group (container) (typed FeaturePython)
  Dunit = g/cm3
  Dvalue = 1.141
  Group = -> [O_element106]
  conduct = 2
  density = 1
  expand = 3
  formula = G4_lO2
  name = G4_lO2
  specific = 4
FEATURE [App::DocumentObjectGroupPython] Ar  label="Ar : 1"  # scripted group (container) (typed FeaturePython)
  n = 1
  ref = Ar
FEATURE [App::DocumentObjectGroupPython] G4_lAr  # scripted group (container) (typed FeaturePython)
  Dunit = g/cm3
  Dvalue = 1.396
  Group = -> [Ar]
  conduct = 2
  density = 1
  expand = 3
  formula = G4_lAr
  name = G4_lAr
  specific = 4
FEATURE [App::DocumentObjectGroupPython] Br  label="Br : 1"  # scripted group (container) (typed FeaturePython)
  n = 1
  ref = Br
FEATURE [App::DocumentObjectGroupPython] G4_lBr  # scripted group (container) (typed FeaturePython)
  Dunit = g/cm3
  Dvalue = 3.1028
  Group = -> [Br]
  conduct = 2
  density = 1
  expand = 3
  formula = G4_lBr
  name = G4_lBr
  specific = 4
FEATURE [App::DocumentObjectGroupPython] Kr  label="Kr : 1"  # scripted group (container) (typed FeaturePython)
  n = 1
  ref = Kr
FEATURE [App::DocumentObjectGroupPython] G4_lKr  # scripted group (container) (typed FeaturePython)
  Dunit = g/cm3
  Dvalue = 2.418
  Group = -> [Kr]
  conduct = 2
  density = 1
  expand = 3
  formula = G4_lKr
  name = G4_lKr
  specific = 4
FEATURE [App::DocumentObjectGroupPython] Xe  label="Xe : 1"  # scripted group (container) (typed FeaturePython)
  n = 1
  ref = Xe
FEATURE [App::DocumentObjectGroupPython] G4_lXe  # scripted group (container) (typed FeaturePython)
  Dunit = g/cm3
  Dvalue = 2.953
  Group = -> [Xe]
  conduct = 2
  density = 1
  expand = 3
  formula = G4_lXe
  name = G4_lXe
  specific = 4
FEATURE [App::DocumentObjectGroupPython] O_element107  label="O_element : 061"  # scripted group (container) (typed FeaturePython)
  n = 4
  ref = O_element
FEATURE [App::DocumentObjectGroupPython] Pb_element004  label="Pb_element : 002"  # scripted group (container) (typed FeaturePython)
  n = 1
  ref = Pb_element
FEATURE [App::DocumentObjectGroupPython] W_element005  label="W_element : 005"  # scripted group (container) (typed FeaturePython)
  n = 1
  ref = W_element
FEATURE [App::DocumentObjectGroupPython] G4_PbWO4  # scripted group (container) (typed FeaturePython)
  Dunit = g/cm3
  Dvalue = 8.28
  Group = -> [O_element107,Pb_element004,W_element005]
  conduct = 2
  density = 1
  expand = 3
  formula = G4_PbWO4
  name = G4_PbWO4
  specific = 4
FEATURE [App::DocumentObjectGroupPython] alactic  label="alactic : 1"  # scripted group (container) (typed FeaturePython)
  n = 1
  ref = alactic
FEATURE [App::DocumentObjectGroupPython] G4_Galactic  # scripted group (container) (typed FeaturePython)
  Dunit = g/cm3
  Dvalue = 0
  Group = -> [alactic]
  conduct = 2
  density = 1
  expand = 3
  formula = G4_Galactic
  name = G4_Galactic
  specific = 4
FEATURE [App::DocumentObjectGroupPython] RAPHITE_POROUS  label="RAPHITE_POROUS : 1"  # scripted group (container) (typed FeaturePython)
  n = 1
  ref = RAPHITE_POROUS
FEATURE [App::DocumentObjectGroupPython] G4_GRAPHITE_POROUS  # scripted group (container) (typed FeaturePython)
  Dunit = g/cm3
  Dvalue = 1.7
  Group = -> [RAPHITE_POROUS]
  conduct = 2
  density = 1
  expand = 3
  formula = G4_GRAPHITE_POROUS
  name = G4_GRAPHITE_POROUS
  specific = 4
FEATURE [App::DocumentObjectGroupPython] H_element115  label="H_element : 0.150"  # scripted group (container) (typed FeaturePython)
  n = 0.080538
FEATURE [App::DocumentObjectGroupPython] C_element125  label="C_element : 0.600"  # scripted group (container) (typed FeaturePython)
  n = 0.599848
FEATURE [App::DocumentObjectGroupPython] O_element108  label="O_element : 0.320"  # scripted group (container) (typed FeaturePython)
  n = 0.319614
FEATURE [App::DocumentObjectGroupPython] G4_LUCITE  # scripted group (container) (typed FeaturePython)
  Dunit = g/cm3
  Dvalue = 1.19
  Group = -> [H_element115,C_element125,O_element108]
  conduct = 2
  density = 1
  expand = 3
  formula = G4_LUCITE
  name = G4_LUCITE
  specific = 4
FEATURE [App::DocumentObjectGroupPython] Cu_element002  label="Cu_element : 62"  # scripted group (container) (typed FeaturePython)
  n = 62
  ref = Cu_element
FEATURE [App::DocumentObjectGroupPython] Zn_element002  label="Zn_element : 35"  # scripted group (container) (typed FeaturePython)
  n = 35
  ref = Zn_element
FEATURE [App::DocumentObjectGroupPython] Pb_element005  label="Pb_element : 3"  # scripted group (container) (typed FeaturePython)
  n = 3
  ref = Pb_element
FEATURE [App::DocumentObjectGroupPython] G4_BRASS  # scripted group (container) (typed FeaturePython)
  Dunit = g/cm3
  Dvalue = 8.52
  Group = -> [Cu_element002,Zn_element002,Pb_element005]
  conduct = 2
  density = 1
  expand = 3
  formula = G4_BRASS
  name = G4_BRASS
  specific = 4
FEATURE [App::DocumentObjectGroupPython] Cu_element003  label="Cu_element : 89"  # scripted group (container) (typed FeaturePython)
  n = 89
  ref = Cu_element
FEATURE [App::DocumentObjectGroupPython] Zn_element003  label="Zn_element : 9"  # scripted group (container) (typed FeaturePython)
  n = 9
  ref = Zn_element
FEATURE [App::DocumentObjectGroupPython] Pb_element006  label="Pb_element : 2"  # scripted group (container) (typed FeaturePython)
  n = 2
  ref = Pb_element
FEATURE [App::DocumentObjectGroupPython] G4_BRONZE  # scripted group (container) (typed FeaturePython)
  Dunit = g/cm3
  Dvalue = 8.82
  Group = -> [Cu_element003,Zn_element003,Pb_element006]
  conduct = 2
  density = 1
  expand = 3
  formula = G4_BRONZE
  name = G4_BRONZE
  specific = 4
FEATURE [App::DocumentObjectGroupPython] Fe_element008  label="Fe_element : 74"  # scripted group (container) (typed FeaturePython)
  n = 74
  ref = Fe_element
FEATURE [App::DocumentObjectGroupPython] Cr_element002  label="Cr_element : 18"  # scripted group (container) (typed FeaturePython)
  n = 18
  ref = Cr_element
FEATURE [App::DocumentObjectGroupPython] Ni_element002  label="Ni_element : 8"  # scripted group (container) (typed FeaturePython)
  n = 8
  ref = Ni_element
FEATURE [App::DocumentObjectGroupPython] G4_STAINLESS_STEEL  label="G4_STAINLESS-STEEL"  # scripted group (container) (typed FeaturePython)
  Dunit = g/cm3
  Dvalue = 8
  Group = -> [Fe_element008,Cr_element002,Ni_element002]
  conduct = 2
  density = 1
  expand = 3
  formula = G4_STAINLESS-STEEL
  name = G4_STAINLESS-STEEL
  specific = 4
FEATURE [App::DocumentObjectGroupPython] H_element116  label="H_element : 064"  # scripted group (container) (typed FeaturePython)
  n = 18
  ref = H_element
FEATURE [App::DocumentObjectGroupPython] C_element126  label="C_element : 071"  # scripted group (container) (typed FeaturePython)
  n = 12
  ref = C_element
FEATURE [App::DocumentObjectGroupPython] O_element109  label="O_element : 062"  # scripted group (container) (typed FeaturePython)
  n = 7
  ref = O_element
FEATURE [App::DocumentObjectGroupPython] G4_CR39  # scripted group (container) (typed FeaturePython)
  Dunit = g/cm3
  Dvalue = 1.32
  Group = -> [H_element116,C_element126,O_element109]
  conduct = 2
  density = 1
  expand = 3
  formula = G4_CR39
  name = G4_CR39
  specific = 4
FEATURE [App::DocumentObjectGroupPython] H_element117  label="H_element : 38"  # scripted group (container) (typed FeaturePython)
  n = 38
  ref = H_element
FEATURE [App::DocumentObjectGroupPython] C_element127  label="C_element : 072"  # scripted group (container) (typed FeaturePython)
  n = 18
  ref = C_element
FEATURE [App::DocumentObjectGroupPython] O_element110  label="O_element : 063"  # scripted group (container) (typed FeaturePython)
  n = 1
  ref = O_element
FEATURE [App::DocumentObjectGroupPython] G4_OCTADECANOL  # scripted group (container) (typed FeaturePython)
  Dunit = g/cm3
  Dvalue = 0.812
  Group = -> [H_element117,C_element127,O_element110]
  conduct = 2
  density = 1
  expand = 3
  formula = G4_OCTADECANOL
  name = G4_OCTADECANOL
  specific = 4
FEATURE [App::DocumentObjectGroupPython] HEP  # scripted group (container) (typed FeaturePython)
  Group = -> [G4_lH2,G4_lN2,G4_lO2,G4_lAr,G4_lBr,G4_lKr,G4_lXe,G4_PbWO4,G4_Galactic,G4_GRAPHITE_POROUS,G4_LUCITE,G4_BRASS,G4_BRONZE,G4_STAINLESS_STEEL,G4_CR39,G4_OCTADECANOL]
FEATURE [App::DocumentObjectGroupPython] C_element128  label="C_element : 073"  # scripted group (container) (typed FeaturePython)
  n = 14
  ref = C_element
FEATURE [App::DocumentObjectGroupPython] H_element118  label="H_element : 065"  # scripted group (container) (typed FeaturePython)
  n = 10
  ref = H_element
FEATURE [App::DocumentObjectGroupPython] O_element111  label="O_element : 064"  # scripted group (container) (typed FeaturePython)
  n = 2
  ref = O_element
FEATURE [App::DocumentObjectGroupPython] N_element050  label="N_element : 023"  # scripted group (container) (typed FeaturePython)
  n = 2
  ref = N_element
FEATURE [App::DocumentObjectGroupPython] G4_KEVLAR  # scripted group (container) (typed FeaturePython)
  Dunit = g/cm3
  Dvalue = 1.44
  Group = -> [C_element128,H_element118,O_element111,N_element050]
  conduct = 2
  density = 1
  expand = 3
  formula = G4_KEVLAR
  name = G4_KEVLAR
  specific = 4
FEATURE [App::DocumentObjectGroupPython] C_element129  label="C_element : 074"  # scripted group (container) (typed FeaturePython)
  n = 10
  ref = C_element
FEATURE [App::DocumentObjectGroupPython] H_element119  label="H_element : 066"  # scripted group (container) (typed FeaturePython)
  n = 8
  ref = H_element
FEATURE [App::DocumentObjectGroupPython] O_element112  label="O_element : 065"  # scripted group (container) (typed FeaturePython)
  n = 4
  ref = O_element
FEATURE [App::DocumentObjectGroupPython] G4_DACRON  # scripted group (container) (typed FeaturePython)
  Dunit = g/cm3
  Dvalue = 1.4
  Group = -> [C_element129,H_element119,O_element112]
  conduct = 2
  density = 1
  expand = 3
  formula = G4_DACRON
  name = G4_DACRON
  specific = 4
FEATURE [App::DocumentObjectGroupPython] C_element130  label="C_element : 075"  # scripted group (container) (typed FeaturePython)
  n = 4
  ref = C_element
FEATURE [App::DocumentObjectGroupPython] H_element120  label="H_element : 067"  # scripted group (container) (typed FeaturePython)
  n = 5
  ref = H_element
FEATURE [App::DocumentObjectGroupPython] Cl_element030  label="Cl_element : 016"  # scripted group (container) (typed FeaturePython)
  n = 1
  ref = Cl_element
FEATURE [App::DocumentObjectGroupPython] G4_NEOPRENE  # scripted group (container) (typed FeaturePython)
  Dunit = g/cm3
  Dvalue = 1.23
  Group = -> [C_element130,H_element120,Cl_element030]
  conduct = 2
  density = 1
  expand = 3
  formula = G4_NEOPRENE
  name = G4_NEOPRENE
  specific = 4
FEATURE [App::DocumentObjectGroupPython] Space  # scripted group (container) (typed FeaturePython)
  Group = -> [G4_KEVLAR,G4_DACRON,G4_NEOPRENE]
FEATURE [App::DocumentObjectGroupPython] H_element121  label="H_element : 068"  # scripted group (container) (typed FeaturePython)
  n = 5
  ref = H_element
FEATURE [App::DocumentObjectGroupPython] C_element131  label="C_element : 076"  # scripted group (container) (typed FeaturePython)
  n = 4
  ref = C_element
FEATURE [App::DocumentObjectGroupPython] N_element051  label="N_element : 3"  # scripted group (container) (typed FeaturePython)
  n = 3
  ref = N_element
FEATURE [App::DocumentObjectGroupPython] O_element113  label="O_element : 066"  # scripted group (container) (typed FeaturePython)
  n = 1
  ref = O_element
FEATURE [App::DocumentObjectGroupPython] G4_CYTOSINE  # scripted group (container) (typed FeaturePython)
  Dunit = g/cm3
  Dvalue = 1.55
  Group = -> [H_element121,C_element131,N_element051,O_element113]
  conduct = 2
  density = 1
  expand = 3
  formula = G4_CYTOSINE
  name = G4_CYTOSINE
  specific = 4
FEATURE [App::DocumentObjectGroupPython] H_element122  label="H_element : 069"  # scripted group (container) (typed FeaturePython)
  n = 6
  ref = H_element
FEATURE [App::DocumentObjectGroupPython] C_element132  label="C_element : 077"  # scripted group (container) (typed FeaturePython)
  n = 5
  ref = C_element
FEATURE [App::DocumentObjectGroupPython] N_element052  label="N_element : 024"  # scripted group (container) (typed FeaturePython)
  n = 2
  ref = N_element
FEATURE [App::DocumentObjectGroupPython] O_element114  label="O_element : 067"  # scripted group (container) (typed FeaturePython)
  n = 2
  ref = O_element
FEATURE [App::DocumentObjectGroupPython] G4_THYMINE  # scripted group (container) (typed FeaturePython)
  Dunit = g/cm3
  Dvalue = 1.23
  Group = -> [H_element122,C_element132,N_element052,O_element114]
  conduct = 2
  density = 1
  expand = 3
  formula = G4_THYMINE
  name = G4_THYMINE
  specific = 4
FEATURE [App::DocumentObjectGroupPython] H_element123  label="H_element : 070"  # scripted group (container) (typed FeaturePython)
  n = 4
  ref = H_element
FEATURE [App::DocumentObjectGroupPython] C_element133  label="C_element : 078"  # scripted group (container) (typed FeaturePython)
  n = 4
  ref = C_element
FEATURE [App::DocumentObjectGroupPython] N_element053  label="N_element : 025"  # scripted group (container) (typed FeaturePython)
  n = 2
  ref = N_element
FEATURE [App::DocumentObjectGroupPython] O_element115  label="O_element : 068"  # scripted group (container) (typed FeaturePython)
  n = 2
  ref = O_element
FEATURE [App::DocumentObjectGroupPython] G4_URACIL  # scripted group (container) (typed FeaturePython)
  Dunit = g/cm3
  Dvalue = 1.32
  Group = -> [H_element123,C_element133,N_element053,O_element115]
  conduct = 2
  density = 1
  expand = 3
  formula = G4_URACIL
  name = G4_URACIL
  specific = 4
FEATURE [App::DocumentObjectGroupPython] H_element124  label="H_element : 071"  # scripted group (container) (typed FeaturePython)
  n = 4
  ref = H_element
FEATURE [App::DocumentObjectGroupPython] C_element134  label="C_element : 079"  # scripted group (container) (typed FeaturePython)
  n = 5
  ref = C_element
FEATURE [App::DocumentObjectGroupPython] N_element054  label="N_element : 026"  # scripted group (container) (typed FeaturePython)
  n = 5
  ref = N_element
FEATURE [App::DocumentObjectGroupPython] G4_DNA_ADENINE  # scripted group (container) (typed FeaturePython)
  Dunit = g/cm3
  Dvalue = 1
  Group = -> [H_element124,C_element134,N_element054]
  conduct = 2
  density = 1
  expand = 3
  formula = G4_DNA_ADENINE
  name = G4_DNA_ADENINE
  specific = 4
FEATURE [App::DocumentObjectGroupPython] H_element125  label="H_element : 072"  # scripted group (container) (typed FeaturePython)
  n = 4
  ref = H_element
FEATURE [App::DocumentObjectGroupPython] C_element135  label="C_element : 080"  # scripted group (container) (typed FeaturePython)
  n = 5
  ref = C_element
FEATURE [App::DocumentObjectGroupPython] N_element055  label="N_element : 027"  # scripted group (container) (typed FeaturePython)
  n = 5
  ref = N_element
FEATURE [App::DocumentObjectGroupPython] O_element116  label="O_element : 069"  # scripted group (container) (typed FeaturePython)
  n = 1
  ref = O_element
FEATURE [App::DocumentObjectGroupPython] G4_DNA_GUANINE  # scripted group (container) (typed FeaturePython)
  Dunit = g/cm3
  Dvalue = 1
  Group = -> [H_element125,C_element135,N_element055,O_element116]
  conduct = 2
  density = 1
  expand = 3
  formula = G4_DNA_GUANINE
  name = G4_DNA_GUANINE
  specific = 4
FEATURE [App::DocumentObjectGroupPython] H_element126  label="H_element : 073"  # scripted group (container) (typed FeaturePython)
  n = 4
  ref = H_element
FEATURE [App::DocumentObjectGroupPython] C_element136  label="C_element : 081"  # scripted group (container) (typed FeaturePython)
  n = 4
  ref = C_element
FEATURE [App::DocumentObjectGroupPython] N_element056  label="N_element : 028"  # scripted group (container) (typed FeaturePython)
  n = 3
  ref = N_element
FEATURE [App::DocumentObjectGroupPython] O_element117  label="O_element : 070"  # scripted group (container) (typed FeaturePython)
  n = 1
  ref = O_element
FEATURE [App::DocumentObjectGroupPython] G4_DNA_CYTOSINE  # scripted group (container) (typed FeaturePython)
  Dunit = g/cm3
  Dvalue = 1
  Group = -> [H_element126,C_element136,N_element056,O_element117]
  conduct = 2
  density = 1
  expand = 3
  formula = G4_DNA_CYTOSINE
  name = G4_DNA_CYTOSINE
  specific = 4
FEATURE [App::DocumentObjectGroupPython] H_element127  label="H_element : 074"  # scripted group (container) (typed FeaturePython)
  n = 5
  ref = H_element
FEATURE [App::DocumentObjectGroupPython] C_element137  label="C_element : 082"  # scripted group (container) (typed FeaturePython)
  n = 5
  ref = C_element
FEATURE [App::DocumentObjectGroupPython] N_element057  label="N_element : 029"  # scripted group (container) (typed FeaturePython)
  n = 2
  ref = N_element
FEATURE [App::DocumentObjectGroupPython] O_element118  label="O_element : 071"  # scripted group (container) (typed FeaturePython)
  n = 2
  ref = O_element
FEATURE [App::DocumentObjectGroupPython] G4_DNA_THYMINE  # scripted group (container) (typed FeaturePython)
  Dunit = g/cm3
  Dvalue = 1
  Group = -> [H_element127,C_element137,N_element057,O_element118]
  conduct = 2
  density = 1
  expand = 3
  formula = G4_DNA_THYMINE
  name = G4_DNA_THYMINE
  specific = 4
FEATURE [App::DocumentObjectGroupPython] H_element128  label="H_element : 075"  # scripted group (container) (typed FeaturePython)
  n = 3
  ref = H_element
FEATURE [App::DocumentObjectGroupPython] C_element138  label="C_element : 083"  # scripted group (container) (typed FeaturePython)
  n = 4
  ref = C_element
FEATURE [App::DocumentObjectGroupPython] N_element058  label="N_element : 030"  # scripted group (container) (typed FeaturePython)
  n = 2
  ref = N_element
FEATURE [App::DocumentObjectGroupPython] O_element119  label="O_element : 072"  # scripted group (container) (typed FeaturePython)
  n = 2
  ref = O_element
FEATURE [App::DocumentObjectGroupPython] G4_DNA_URACIL  # scripted group (container) (typed FeaturePython)
  Dunit = g/cm3
  Dvalue = 1
  Group = -> [H_element128,C_element138,N_element058,O_element119]
  conduct = 2
  density = 1
  expand = 3
  formula = G4_DNA_URACIL
  name = G4_DNA_URACIL
  specific = 4
FEATURE [App::DocumentObjectGroupPython] H_element129  label="H_element : 076"  # scripted group (container) (typed FeaturePython)
  n = 10
  ref = H_element
FEATURE [App::DocumentObjectGroupPython] C_element139  label="C_element : 084"  # scripted group (container) (typed FeaturePython)
  n = 10
  ref = C_element
FEATURE [App::DocumentObjectGroupPython] N_element059  label="N_element : 031"  # scripted group (container) (typed FeaturePython)
  n = 5
  ref = N_element
FEATURE [App::DocumentObjectGroupPython] O_element120  label="O_element : 073"  # scripted group (container) (typed FeaturePython)
  n = 4
  ref = O_element
FEATURE [App::DocumentObjectGroupPython] G4_DNA_ADENOSINE  # scripted group (container) (typed FeaturePython)
  Dunit = g/cm3
  Dvalue = 1
  Group = -> [H_element129,C_element139,N_element059,O_element120]
  conduct = 2
  density = 1
  expand = 3
  formula = G4_DNA_ADENOSINE
  name = G4_DNA_ADENOSINE
  specific = 4
FEATURE [App::DocumentObjectGroupPython] H_element130  label="H_element : 077"  # scripted group (container) (typed FeaturePython)
  n = 10
  ref = H_element
FEATURE [App::DocumentObjectGroupPython] C_element140  label="C_element : 085"  # scripted group (container) (typed FeaturePython)
  n = 10
  ref = C_element
FEATURE [App::DocumentObjectGroupPython] N_element060  label="N_element : 032"  # scripted group (container) (typed FeaturePython)
  n = 5
  ref = N_element
FEATURE [App::DocumentObjectGroupPython] O_element121  label="O_element : 074"  # scripted group (container) (typed FeaturePython)
  n = 5
  ref = O_element
FEATURE [App::DocumentObjectGroupPython] G4_DNA_GUANOSINE  # scripted group (container) (typed FeaturePython)
  Dunit = g/cm3
  Dvalue = 1
  Group = -> [H_element130,C_element140,N_element060,O_element121]
  conduct = 2
  density = 1
  expand = 3
  formula = G4_DNA_GUANOSINE
  name = G4_DNA_GUANOSINE
  specific = 4
FEATURE [App::DocumentObjectGroupPython] H_element131  label="H_element : 078"  # scripted group (container) (typed FeaturePython)
  n = 10
  ref = H_element
FEATURE [App::DocumentObjectGroupPython] C_element141  label="C_element : 086"  # scripted group (container) (typed FeaturePython)
  n = 9
  ref = C_element
FEATURE [App::DocumentObjectGroupPython] N_element061  label="N_element : 033"  # scripted group (container) (typed FeaturePython)
  n = 3
  ref = N_element
FEATURE [App::DocumentObjectGroupPython] O_element122  label="O_element : 075"  # scripted group (container) (typed FeaturePython)
  n = 5
  ref = O_element
FEATURE [App::DocumentObjectGroupPython] G4_DNA_CYTIDINE  # scripted group (container) (typed FeaturePython)
  Dunit = g/cm3
  Dvalue = 1
  Group = -> [H_element131,C_element141,N_element061,O_element122]
  conduct = 2
  density = 1
  expand = 3
  formula = G4_DNA_CYTIDINE
  name = G4_DNA_CYTIDINE
  specific = 4
FEATURE [App::DocumentObjectGroupPython] H_element132  label="H_element : 079"  # scripted group (container) (typed FeaturePython)
  n = 9
  ref = H_element
FEATURE [App::DocumentObjectGroupPython] C_element142  label="C_element : 087"  # scripted group (container) (typed FeaturePython)
  n = 9
  ref = C_element
FEATURE [App::DocumentObjectGroupPython] N_element062  label="N_element : 034"  # scripted group (container) (typed FeaturePython)
  n = 2
  ref = N_element
FEATURE [App::DocumentObjectGroupPython] O_element123  label="O_element : 076"  # scripted group (container) (typed FeaturePython)
  n = 6
  ref = O_element
FEATURE [App::DocumentObjectGroupPython] G4_DNA_URIDINE  # scripted group (container) (typed FeaturePython)
  Dunit = g/cm3
  Dvalue = 1
  Group = -> [H_element132,C_element142,N_element062,O_element123]
  conduct = 2
  density = 1
  expand = 3
  formula = G4_DNA_URIDINE
  name = G4_DNA_URIDINE
  specific = 4
FEATURE [App::DocumentObjectGroupPython] H_element133  label="H_element : 080"  # scripted group (container) (typed FeaturePython)
  n = 11
  ref = H_element
FEATURE [App::DocumentObjectGroupPython] C_element143  label="C_element : 088"  # scripted group (container) (typed FeaturePython)
  n = 10
  ref = C_element
FEATURE [App::DocumentObjectGroupPython] N_element063  label="N_element : 035"  # scripted group (container) (typed FeaturePython)
  n = 2
  ref = N_element
FEATURE [App::DocumentObjectGroupPython] O_element124  label="O_element : 077"  # scripted group (container) (typed FeaturePython)
  n = 6
  ref = O_element
FEATURE [App::DocumentObjectGroupPython] G4_DNA_METHYLURIDINE  # scripted group (container) (typed FeaturePython)
  Dunit = g/cm3
  Dvalue = 1
  Group = -> [H_element133,C_element143,N_element063,O_element124]
  conduct = 2
  density = 1
  expand = 3
  formula = G4_DNA_METHYLURIDINE
  name = G4_DNA_METHYLURIDINE
  specific = 4
FEATURE [App::DocumentObjectGroupPython] P_element014  label="P_element : 003"  # scripted group (container) (typed FeaturePython)
  n = 1
  ref = P_element
FEATURE [App::DocumentObjectGroupPython] O_element125  label="O_element : 078"  # scripted group (container) (typed FeaturePython)
  n = 3
  ref = O_element
FEATURE [App::DocumentObjectGroupPython] G4_DNA_MONOPHOSPHATE  # scripted group (container) (typed FeaturePython)
  Dunit = g/cm3
  Dvalue = 1
  Group = -> [P_element014,O_element125]
  conduct = 2
  density = 1
  expand = 3
  formula = G4_DNA_MONOPHOSPHATE
  name = G4_DNA_MONOPHOSPHATE
  specific = 4
FEATURE [App::DocumentObjectGroupPython] H_element134  label="H_element : 081"  # scripted group (container) (typed FeaturePython)
  n = 10
  ref = H_element
FEATURE [App::DocumentObjectGroupPython] C_element144  label="C_element : 089"  # scripted group (container) (typed FeaturePython)
  n = 10
  ref = C_element
FEATURE [App::DocumentObjectGroupPython] N_element064  label="N_element : 036"  # scripted group (container) (typed FeaturePython)
  n = 5
  ref = N_element
FEATURE [App::DocumentObjectGroupPython] O_element126  label="O_element : 079"  # scripted group (container) (typed FeaturePython)
  n = 7
  ref = O_element
FEATURE [App::DocumentObjectGroupPython] P_element015  label="P_element : 004"  # scripted group (container) (typed FeaturePython)
  n = 1
  ref = P_element
FEATURE [App::DocumentObjectGroupPython] G4_DNA_A  # scripted group (container) (typed FeaturePython)
  Dunit = g/cm3
  Dvalue = 1
  Group = -> [H_element134,C_element144,N_element064,O_element126,P_element015]
  conduct = 2
  density = 1
  expand = 3
  formula = G4_DNA_A
  name = G4_DNA_A
  specific = 4
FEATURE [App::DocumentObjectGroupPython] H_element135  label="H_element : 082"  # scripted group (container) (typed FeaturePython)
  n = 10
  ref = H_element
FEATURE [App::DocumentObjectGroupPython] C_element145  label="C_element : 090"  # scripted group (container) (typed FeaturePython)
  n = 10
  ref = C_element
FEATURE [App::DocumentObjectGroupPython] N_element065  label="N_element : 037"  # scripted group (container) (typed FeaturePython)
  n = 5
  ref = N_element
FEATURE [App::DocumentObjectGroupPython] O_element127  label="O_element : 8"  # scripted group (container) (typed FeaturePython)
  n = 8
  ref = O_element
FEATURE [App::DocumentObjectGroupPython] P_element016  label="P_element : 005"  # scripted group (container) (typed FeaturePython)
  n = 1
  ref = P_element
FEATURE [App::DocumentObjectGroupPython] G4_DNA_G  # scripted group (container) (typed FeaturePython)
  Dunit = g/cm3
  Dvalue = 1
  Group = -> [H_element135,C_element145,N_element065,O_element127,P_element016]
  conduct = 2
  density = 1
  expand = 3
  formula = G4_DNA_G
  name = G4_DNA_G
  specific = 4
FEATURE [App::DocumentObjectGroupPython] H_element136  label="H_element : 083"  # scripted group (container) (typed FeaturePython)
  n = 10
  ref = H_element
FEATURE [App::DocumentObjectGroupPython] C_element146  label="C_element : 091"  # scripted group (container) (typed FeaturePython)
  n = 9
  ref = C_element
FEATURE [App::DocumentObjectGroupPython] N_element066  label="N_element : 038"  # scripted group (container) (typed FeaturePython)
  n = 3
  ref = N_element
FEATURE [App::DocumentObjectGroupPython] O_element128  label="O_element : 080"  # scripted group (container) (typed FeaturePython)
  n = 8
  ref = O_element
FEATURE [App::DocumentObjectGroupPython] P_element017  label="P_element : 006"  # scripted group (container) (typed FeaturePython)
  n = 1
  ref = P_element
FEATURE [App::DocumentObjectGroupPython] G4_DNA_C  # scripted group (container) (typed FeaturePython)
  Dunit = g/cm3
  Dvalue = 1
  Group = -> [H_element136,C_element146,N_element066,O_element128,P_element017]
  conduct = 2
  density = 1
  expand = 3
  formula = G4_DNA_C
  name = G4_DNA_C
  specific = 4
FEATURE [App::DocumentObjectGroupPython] H_element137  label="H_element : 084"  # scripted group (container) (typed FeaturePython)
  n = 9
  ref = H_element
FEATURE [App::DocumentObjectGroupPython] C_element147  label="C_element : 092"  # scripted group (container) (typed FeaturePython)
  n = 9
  ref = C_element
FEATURE [App::DocumentObjectGroupPython] N_element067  label="N_element : 039"  # scripted group (container) (typed FeaturePython)
  n = 2
  ref = N_element
FEATURE [App::DocumentObjectGroupPython] O_element129  label="O_element : 9"  # scripted group (container) (typed FeaturePython)
  n = 9
  ref = O_element
FEATURE [App::DocumentObjectGroupPython] P_element018  label="P_element : 007"  # scripted group (container) (typed FeaturePython)
  n = 1
  ref = P_element
FEATURE [App::DocumentObjectGroupPython] G4_DNA_U  # scripted group (container) (typed FeaturePython)
  Dunit = g/cm3
  Dvalue = 1
  Group = -> [H_element137,C_element147,N_element067,O_element129,P_element018]
  conduct = 2
  density = 1
  expand = 3
  formula = G4_DNA_U
  name = G4_DNA_U
  specific = 4
FEATURE [App::DocumentObjectGroupPython] H_element138  label="H_element : 085"  # scripted group (container) (typed FeaturePython)
  n = 11
  ref = H_element
FEATURE [App::DocumentObjectGroupPython] C_element148  label="C_element : 093"  # scripted group (container) (typed FeaturePython)
  n = 10
  ref = C_element
FEATURE [App::DocumentObjectGroupPython] N_element068  label="N_element : 040"  # scripted group (container) (typed FeaturePython)
  n = 2
  ref = N_element
FEATURE [App::DocumentObjectGroupPython] O_element130  label="O_element : 081"  # scripted group (container) (typed FeaturePython)
  n = 9
  ref = O_element
FEATURE [App::DocumentObjectGroupPython] P_element019  label="P_element : 008"  # scripted group (container) (typed FeaturePython)
  n = 1
  ref = P_element
FEATURE [App::DocumentObjectGroupPython] G4_DNA_MU  # scripted group (container) (typed FeaturePython)
  Dunit = g/cm3
  Dvalue = 1
  Group = -> [H_element138,C_element148,N_element068,O_element130,P_element019]
  conduct = 2
  density = 1
  expand = 3
  formula = G4_DNA_MU
  name = G4_DNA_MU
  specific = 4
FEATURE [App::DocumentObjectGroupPython] BioChemical  # scripted group (container) (typed FeaturePython)
  Group = -> [G4_CYTOSINE,G4_THYMINE,G4_URACIL,G4_DNA_ADENINE,G4_DNA_GUANINE,G4_DNA_CYTOSINE,G4_DNA_THYMINE,G4_DNA_URACIL,G4_DNA_ADENOSINE,G4_DNA_GUANOSINE,G4_DNA_CYTIDINE,G4_DNA_URIDINE,G4_DNA_METHYLURIDINE,G4_DNA_MONOPHOSPHATE,G4_DNA_A,G4_DNA_G,G4_DNA_C,G4_DNA_U,G4_DNA_MU]
FEATURE [App::DocumentObjectGroupPython] G4Materials  # scripted group (container) (typed FeaturePython)
  Group = -> [NIST,Element,HEP,Space,BioChemical]
  version = 1
FEATURE [App::DocumentObjectGroupPython] Geant4  # scripted group (container) (typed FeaturePython)
  Group = -> [G4Isotopes,G4Elements,G4Materials]
FEATURE [App::DocumentObjectGroupPython] Materials  # scripted group (container) (typed FeaturePython)
  Group = -> [Geant4]
FEATURE [Part::FeaturePython] GDMLBox_WorldBox  # WARN: FeaturePython — macro-defined, semantics opaque (R4)
  lunit = 2
  material = 5
  x = 100
  y = 100
  z = 100
FEATURE [Sketcher::SketchObject] Sketch001
  FullyConstrained = false
  Placement = pos=(0,0,0) rot=(1,0,0;1.5708rad)
  sketch-geometry (5):
    g0: Ellipse CenterX=30.6351 CenterY=6.78706 CenterZ=0 NormalX=0 NormalY=0 NormalZ=1 MajorRadius=17.5631 MinorRadius=6.80538 AngleXU=0.511231
    g1: LineSegment StartX=45.9527 StartY=15.3798 StartZ=0 EndX=15.3176 EndY=-1.80572 EndZ=0
    g2: LineSegment StartX=27.3056 StartY=12.7223 StartZ=0 EndX=33.9647 EndY=0.85179 EndZ=0
    g3: GeomPoint X=44.756 Y=14.7085 Z=0
    g4: GeomPoint X=16.5142 Y=-1.13443 Z=0
  constraints (1):
    c: InternalAlignment(g1-g4 -> g0) x4
FEATURE [Part::Revolution] Revolve
  Angle = 360
  Axis = (0,0,1)
  Base = (0,0,0)
  FaceMakerClass = Part::FaceMakerBullseye
  Solid = true
  Source = -> Sketch001
  Symmetric = false
  material = 5
FEATURE [App::Part] Part
  Group = -> [Sketch001,Revolve]
  Origin = -> Origin001
FEATURE [App::Part] worldVOL
  Group = -> [GDMLBox_WorldBox,Part]
  Origin = -> Origin
